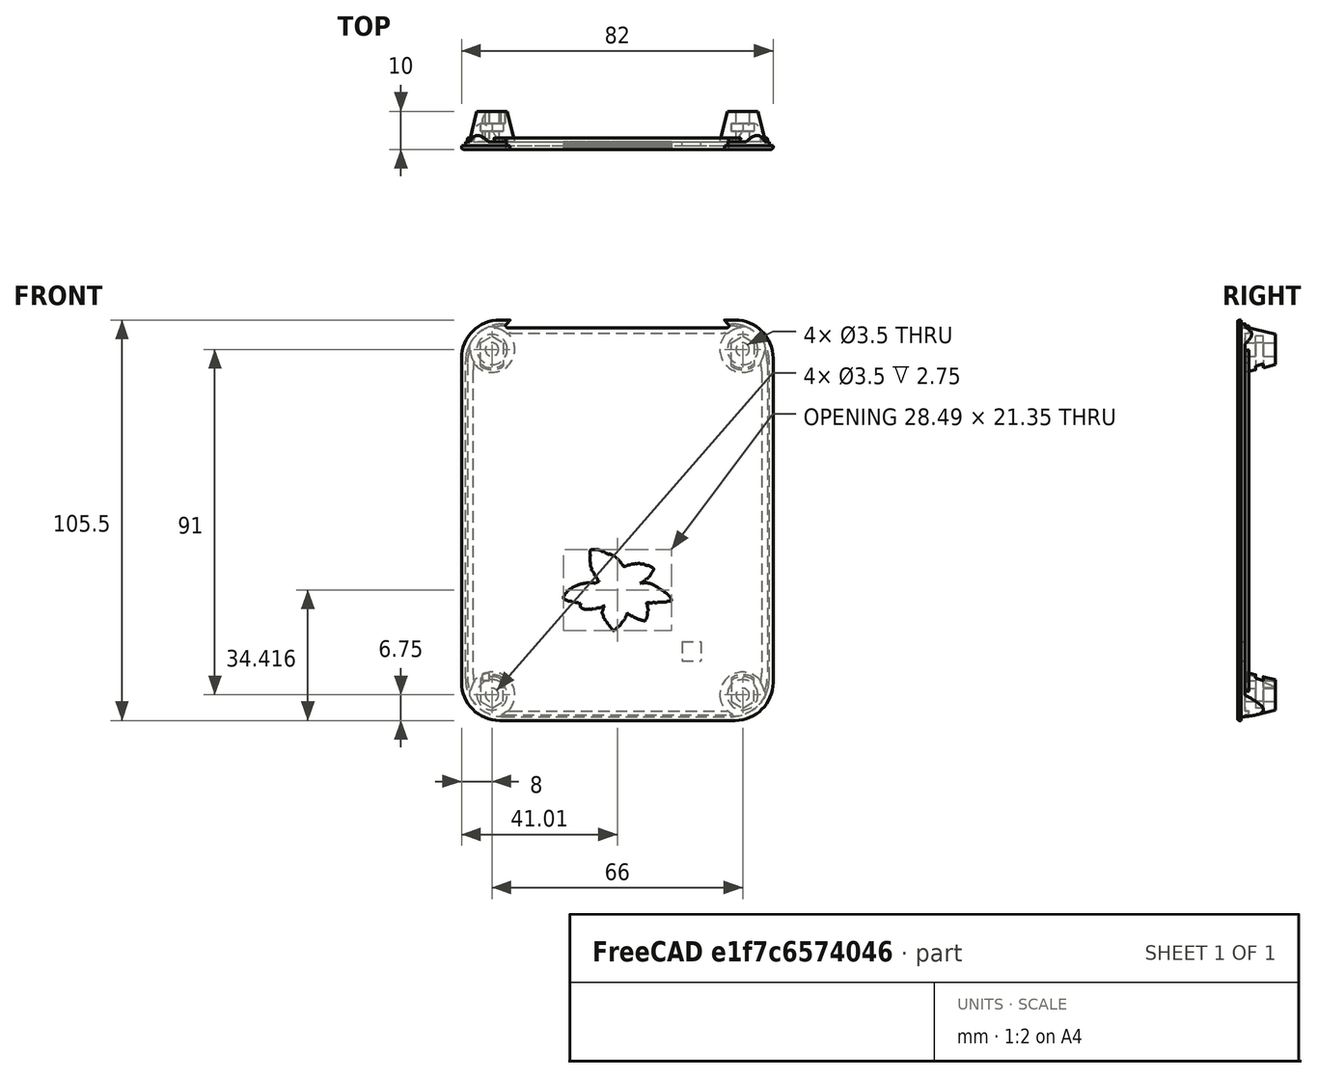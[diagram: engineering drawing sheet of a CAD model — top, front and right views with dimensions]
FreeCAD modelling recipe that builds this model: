
FCSTD DOCUMENT  (FreeCAD 0.20R29410 (Git))
Label: wearableV2_01_16_2023
License: All rights reserved
LicenseURL: http://en.wikipedia.org/wiki/All_rights_reserved
objects: Part::Box×75, Part::MultiFuse×69, Part::Cylinder×59, Part::Fillet×34, Part::Feature×26, Part::Cut×20, Sketcher::SketchObject×18, Part::Extrusion×14, Part::Mirroring×11, Part::Cone×5, PartDesign::Pad×4, PartDesign::Body×4, Part::FeaturePython×4, App::Part×2, Mesh::Feature×1
note: 347 computed .brp shape members not serialized (recipe doc carries the construction recipe); baked Part::Feature solids carry a one-line shape summary decoded from their .brp

FEATURE [Part::Feature] Part__Feature  label="2_BAT_1_1"
  shape: bbox 14.52 x 64.97 x 15.41 mm, 79 faces (baked)
FEATURE [Part::Feature] Part__Feature001  label="2_C_1_1"
  shape: bbox 73.62 x 34.12 x 73.84 mm, 562 faces (baked)
FEATURE [Part::Feature] Part__Feature002  label="2_A_1_1"
  shape: bbox 73.61 x 58.23 x 73.83 mm, 215 faces (baked)
FEATURE [Part::Feature] Part__Feature003  label="2_B_2_1"
  shape: bbox 78.1 x 64.8 x 77.53 mm, 719 faces (baked)
FEATURE [Part::MultiFuse] Fusion
  Shapes = -> [Part__Feature003,Part__Feature002]
FEATURE [Part::MultiFuse] Fusion001
  Shapes = -> [Part__Feature001,Part__Feature]
FEATURE [Part::Feature] Part__Feature004  label="Open CASCADE STEP translator 7.4 2.1.1"
  shape: bbox 8.3 x 1.9 x 1 mm, 10 faces, 0 solids (baked)
FEATURE [Part::Feature] Part__Feature005  label="Open CASCADE STEP translator 7.4 2.1.2"
  shape: bbox 12.5 x 10 x 1.5 mm, 6 faces, 0 solids (baked)
FEATURE [Part::Feature] Part__Feature006  label="Open CASCADE STEP translator 7.4 2.1.3"
  shape: bbox 12.5 x 10 x 1.5 mm, 6 faces, 0 solids (baked)
FEATURE [Part::Feature] Part__Feature007  label="Open CASCADE STEP translator 7.4 2.1.4"
  shape: bbox 12.5 x 10 x 1.5 mm, 6 faces, 0 solids (baked)
FEATURE [Part::Feature] Part__Feature008  label="Open CASCADE STEP translator 7.4 2.1.5"
  shape: bbox 12.5 x 10 x 1.5 mm, 6 faces, 0 solids (baked)
FEATURE [Part::Feature] Part__Feature009  label="Open CASCADE STEP translator 7.4 2.1.6"
  shape: bbox 89.5 x 57.1 x 20.65 mm, 2741 faces, 0 solids (baked)
FEATURE [App::Part] Open_CASCADE_STEP_translator_7_4_2_1  label="Open CASCADE STEP translator 7.4 2.1"
  Group = -> [Part__Feature004,Part__Feature005,Part__Feature006,Part__Feature007,Part__Feature008,Part__Feature009]
  Origin = -> Origin
FEATURE [Part::Box] Box  label="Cube"
  AttacherType = Attacher::AttachEngine3D
  Height = 77
  Length = 78
  Width = 10
FEATURE [Part::Feature] Part__Feature010  label="m312mm"
  Placement = pos=(63.5,-7,61.5) rot=(0,0.707107,0.707107;3.14159rad)
  shape: bbox 6.201 x 15.54 x 6.201 mm, 70 faces (baked)
FEATURE [Part::Feature] Part__Feature011  label="m312mm001"
  Placement = pos=(14.5,-7,61.5) rot=(-1,0,0;1.5708rad)
  shape: bbox 6.201 x 15.54 x 6.201 mm, 70 faces (baked)
FEATURE [Part::MultiFuse] Fusion003
  Shapes = -> [Part__Feature011,Part__Feature010]
FEATURE [Part::Feature] Part__Feature012  label="m312mm002"
  Placement = pos=(14.5,-7,61.5) rot=(-1,0,0;1.5708rad)
  shape: bbox 6.201 x 15.54 x 6.201 mm, 70 faces (baked)
FEATURE [Part::Feature] Part__Feature013  label="m312mm003"
  Placement = pos=(63.5,-7,61.5) rot=(0,0.707107,0.707107;3.14159rad)
  shape: bbox 6.201 x 15.54 x 6.201 mm, 70 faces (baked)
FEATURE [Part::MultiFuse] Fusion004
  Placement = pos=(0,0,-58) rot=(0,0,1;0rad)
  Shapes = -> [Part__Feature012,Part__Feature013]
FEATURE [Part::MultiFuse] Fusion005  label="m3s"
  Placement = pos=(0.1,-1,0) rot=(0,0,1;0rad)
  Shapes = -> [Fusion004,Fusion003]
FEATURE [App::Part] Open_CASCADE_STEP_translator_7_4_2  label="C4"
  Group = -> [Open_CASCADE_STEP_translator_7_4_2_1,Part__Feature010,Part__Feature011,Fusion003,Part__Feature012,Part__Feature013,Fusion004,Fusion005]
  Origin = -> Origin001
  Placement = pos=(67,-7,0) rot=(0.57735,-0.57735,0.57735;2.0944rad)
FEATURE [Part::Box] Box001  label="Cube001"
  AttacherType = Attacher::AttachEngine3D
  Height = 40
  Length = 25
  Placement = pos=(27,-3,12) rot=(0,0,1;0rad)
  Width = 3
FEATURE [Part::Cylinder] Cylinder
  Angle = 360
  AttacherType = Attacher::AttachEngine3D
  FirstAngle = 0
  Height = 3
  Placement = pos=(14.5,-7,3.5) rot=(-1,0,0;1.5708rad)
  Radius = 3.25
  SecondAngle = 0
FEATURE [Part::Cylinder] Cylinder001
  Angle = 360
  AttacherType = Attacher::AttachEngine3D
  FirstAngle = 0
  Height = 3
  Placement = pos=(63.5,-7,3.5) rot=(-1,0,0;1.5708rad)
  Radius = 3.25
  SecondAngle = 0
FEATURE [Part::Cylinder] Cylinder002
  Angle = 360
  AttacherType = Attacher::AttachEngine3D
  FirstAngle = 0
  Height = 3
  Placement = pos=(14.5,-7,3.5) rot=(-1,0,0;1.5708rad)
  Radius = 3.25
  SecondAngle = 0
FEATURE [Part::Cylinder] Cylinder003
  Angle = 360
  AttacherType = Attacher::AttachEngine3D
  FirstAngle = 0
  Height = 3
  Placement = pos=(63.5,-7,3.5) rot=(-1,0,0;1.5708rad)
  Radius = 3.25
  SecondAngle = 0
FEATURE [Part::MultiFuse] Fusion007
  Placement = pos=(0,0,58) rot=(0,0,1;0rad)
  Shapes = -> [Cylinder002,Cylinder003]
FEATURE [Part::Box] Box002  label="Cube002"
  AttacherType = Attacher::AttachEngine3D
  Height = 25
  Length = 5.8
  Placement = pos=(12.12,-7,5.12) rot=(-0.300549,0.945607,0.124491;0.825727rad)
  Width = 3
FEATURE [Part::Mirroring] Part__Mirroring  label="Cube002 (Mirror #1)"
  Base = (0,0,0)
  Normal = (0,0,1)
  Placement = pos=(0,0,65) rot=(0,0,1;0rad)
  Source = -> Box002
FEATURE [Part::MultiFuse] Fusion009
  Shapes = -> [Part__Mirroring,Box002]
FEATURE [Part::Mirroring] Part__Mirroring001  label="Fusion009 (Mirror #2)"
  Base = (0,0,0)
  Normal = (1,0,0)
  Placement = pos=(78,0,0) rot=(0,0,1;0rad)
  Source = -> Fusion009
FEATURE [Part::MultiFuse] Fusion010
  Shapes = -> [Fusion009,Part__Mirroring001]
FEATURE [Part::Box] Box003  label="Cube003"
  AttacherType = Attacher::AttachEngine3D
  Height = 17.78
  Length = 25.4
  Width = 3
FEATURE [Part::Cylinder] Cylinder004
  Angle = 360
  AttacherType = Attacher::AttachEngine3D
  FirstAngle = 0
  Height = 10
  Placement = pos=(2.54,0,2.54) rot=(1,0,0;1.5708rad)
  Radius = 1
  SecondAngle = 0
FEATURE [Part::Cylinder] Cylinder005
  Angle = 360
  AttacherType = Attacher::AttachEngine3D
  FirstAngle = 0
  Height = 10
  Placement = pos=(2.54,0,15.24) rot=(1,0,0;1.5708rad)
  Radius = 1
  SecondAngle = 0
FEATURE [Part::MultiFuse] Fusion011
  Shapes = -> [Cylinder005,Cylinder004]
FEATURE [Part::Cylinder] Cylinder006
  Angle = 360
  AttacherType = Attacher::AttachEngine3D
  FirstAngle = 0
  Height = 10
  Placement = pos=(2.54,0,2.54) rot=(1,0,0;1.5708rad)
  Radius = 1
  SecondAngle = 0
FEATURE [Part::Cylinder] Cylinder007
  Angle = 360
  AttacherType = Attacher::AttachEngine3D
  FirstAngle = 0
  Height = 10
  Placement = pos=(2.54,0,15.24) rot=(1,0,0;1.5708rad)
  Radius = 1
  SecondAngle = 0
FEATURE [Part::MultiFuse] Fusion012
  Placement = pos=(20.32,0,0) rot=(0,0,1;0rad)
  Shapes = -> [Cylinder007,Cylinder006]
FEATURE [Part::MultiFuse] Fusion013
  Placement = pos=(0,3,0) rot=(0,0,1;0rad)
  Shapes = -> [Fusion012,Fusion011]
FEATURE [Part::Cut] Cut
  Base = -> Box003
  Tool = -> Fusion013
FEATURE [Part::Fillet] Fillet
  Base = -> Cut
  Edges = 1 edges r=2: [Edge2]
FEATURE [Part::Fillet] Fillet001
  Base = -> Fillet
  Edges = 1 edges r=2: [Edge2]
FEATURE [Part::Fillet] Fillet002
  Base = -> Fillet001
  Edges = 1 edges r=2: [Edge25]
FEATURE [Part::Fillet] Fillet003  label="bme280AdaFruit"
  Base = -> Fillet002
  Edges = 1 edges r=2: [Edge14]
  Placement = pos=(71,-17.75,-5) rot=(0.57735,0.57735,0.57735;4.18879rad)
FEATURE [Part::Feature] Part__Feature014  label="scd30"
  Placement = pos=(2,-8.5,11) rot=(0.57735,0.57735,0.57735;4.18879rad)
  shape: bbox 7.027 x 23.02 x 35.11 mm, 2292 faces, 25 solids (baked)
FEATURE [Part::Feature] Part__Feature033  label="ips7100"
  Placement = pos=(39,202,-9e-14) rot=(0,-0.707107,0.707107;3.14159rad)
  shape: bbox 48.14 x 44.14 x 13.72 mm, 1935 faces (baked)
FEATURE [Part::Box] Box004  label="Cube004"
  AttacherType = Attacher::AttachEngine3D
  Height = 17.78
  Length = 25.4
  Width = 3
FEATURE [Part::Cylinder] Cylinder008
  Angle = 360
  AttacherType = Attacher::AttachEngine3D
  FirstAngle = 0
  Height = 10
  Placement = pos=(2.54,0,2.54) rot=(1,0,0;1.5708rad)
  Radius = 1
  SecondAngle = 0
FEATURE [Part::Cylinder] Cylinder009
  Angle = 360
  AttacherType = Attacher::AttachEngine3D
  FirstAngle = 0
  Height = 10
  Placement = pos=(2.54,-27.63,15.24) rot=(1,0,0;1.5708rad)
  Radius = 1
  SecondAngle = 0
FEATURE [Part::Cylinder] Cylinder010
  Angle = 360
  AttacherType = Attacher::AttachEngine3D
  FirstAngle = 0
  Height = 10
  Placement = pos=(2.54,0,2.54) rot=(1,0,0;1.5708rad)
  Radius = 1
  SecondAngle = 0
FEATURE [Part::Cylinder] Cylinder011
  Angle = 360
  AttacherType = Attacher::AttachEngine3D
  FirstAngle = 0
  Height = 10
  Placement = pos=(2.54,0,15.24) rot=(1,0,0;1.5708rad)
  Radius = 1
  SecondAngle = 0
FEATURE [Part::MultiFuse] Fusion014
  Shapes = -> [Cylinder009,Cylinder008]
FEATURE [Part::MultiFuse] Fusion015
  Placement = pos=(20.32,0,0) rot=(0,0,1;0rad)
  Shapes = -> [Cylinder011,Cylinder010]
FEATURE [Part::MultiFuse] Fusion016
  Placement = pos=(0,3,0) rot=(0,0,1;0rad)
  Shapes = -> [Fusion015,Fusion014]
FEATURE [Part::Cut] Cut001
  Base = -> Box004
  Placement = pos=(71,-17.7,20.4) rot=(0.57735,-0.57735,-0.57735;4.18879rad)
  Tool = -> Fusion016
FEATURE [Part::Box] Box005  label="Cube005"
  AttacherType = Attacher::AttachEngine3D
  Height = 35
  Length = 3
  Placement = pos=(8,-19,-5) rot=(0,0,1;0rad)
  Width = 19
FEATURE [Part::Box] Box006  label="Cube006"
  AttacherType = Attacher::AttachEngine3D
  Height = 35
  Length = 3
  Placement = pos=(8,-22,-2) rot=(0,0,1;0rad)
  Width = 19
FEATURE [Part::Cut] Cut002
  Base = -> Box005
  Placement = pos=(0.5,0,0) rot=(0,0,1;0rad)
  Tool = -> Box006
FEATURE [Part::Box] Box007  label="Cube007"
  AttacherType = Attacher::AttachEngine3D
  Height = 17
  Length = 36.5
  Width = 3
FEATURE [Part::Cylinder] Cylinder012  label="m2s"
  Angle = 360
  AttacherType = Attacher::AttachEngine3D
  FirstAngle = 0
  Height = 10
  Placement = pos=(0,0,0) rot=(1,0,0;1.5708rad)
  Radius = 1.2
  SecondAngle = 0
FEATURE [Part::Cylinder] Cylinder014  label="m2s001"
  Angle = 360
  AttacherType = Attacher::AttachEngine3D
  FirstAngle = 0
  Height = 10
  Placement = pos=(30,0,0) rot=(1,0,0;1.5708rad)
  Radius = 1.2
  SecondAngle = 0
FEATURE [Part::MultiFuse] Fusion017
  Placement = pos=(3.25,0,0) rot=(0,0,1;0rad)
  Shapes = -> [Cylinder014,Cylinder012]
FEATURE [Part::Cylinder] Cylinder015  label="m2s002"
  Angle = 360
  AttacherType = Attacher::AttachEngine3D
  FirstAngle = 0
  Height = 10
  Placement = pos=(0,0,0) rot=(1,0,0;1.5708rad)
  Radius = 1.2
  SecondAngle = 0
FEATURE [Part::Cylinder] Cylinder016  label="m2s003"
  Angle = 360
  AttacherType = Attacher::AttachEngine3D
  FirstAngle = 0
  Height = 10
  Placement = pos=(30,0,0) rot=(1,0,0;1.5708rad)
  Radius = 1.2
  SecondAngle = 0
FEATURE [Part::MultiFuse] Fusion018
  Placement = pos=(3.25,0,7) rot=(0,0,1;0rad)
  Shapes = -> [Cylinder016,Cylinder015]
FEATURE [Part::MultiFuse] Fusion019
  Placement = pos=(0,3,5) rot=(0,0,1;0rad)
  Shapes = -> [Fusion017,Fusion018]
FEATURE [Part::Cut] Cut003
  Base = -> Box007
  Tool = -> Fusion019
FEATURE [Part::Fillet] Fillet008  label="converterSupport"
  Base = -> Cut003
  Edges = 4 edges r=2: [Edge2,Edge4,Edge13,Edge20]
  Placement = pos=(68,-17,23) rot=(0.57735,0.57735,0.57735;4.18879rad)
FEATURE [Part::Box] Box008  label="Cube008"
  AttacherType = Attacher::AttachEngine3D
  Height = 6
  Length = 30
  Placement = pos=(11,-3,16) rot=(0,0,1;0rad)
  Width = 3
FEATURE [Part::Box] Box009  label="Cube009"
  AttacherType = Attacher::AttachEngine3D
  Height = 6
  Length = 30
  Placement = pos=(41,-3,32) rot=(0,0,1;0rad)
  Width = 3
FEATURE [Part::Box] Box010  label="Cube010"
  AttacherType = Attacher::AttachEngine3D
  Height = 6
  Length = 27
  Placement = pos=(44,-3,12) rot=(0,0,1;0rad)
  Width = 3
  expr: .Placement.Base.z = 12
FEATURE [Part::Box] Box011  label="Cube011"
  AttacherType = Attacher::AttachEngine3D
  Height = 6.25
  Length = 8
  Placement = pos=(63,-7,0.3) rot=(0,0,1;0rad)
  Width = 3
FEATURE [Part::Box] Box012  label="Cube012"
  AttacherType = Attacher::AttachEngine3D
  Height = 6.25
  Length = 3
  Placement = pos=(11.5,-4,6.3) rot=(0,1,0;3.14159rad)
  Width = 3
FEATURE [Part::Box] Box013  label="Cube013"
  AttacherType = Attacher::AttachEngine3D
  Height = 6.25
  Length = 6
  Placement = pos=(14.5,-7,6.3) rot=(0,1,0;3.14159rad)
  Width = 3
FEATURE [Part::Cylinder] Cylinder017
  Angle = 360
  AttacherType = Attacher::AttachEngine3D
  FirstAngle = 0
  Height = 3
  Placement = pos=(11.5,-1.7,28.45) rot=(0.57735,0.57735,-0.57735;4.18879rad)
  Radius = 3.25
  SecondAngle = 0
FEATURE [Part::Cylinder] Cylinder018
  Angle = 360
  AttacherType = Attacher::AttachEngine3D
  FirstAngle = 0
  Height = 3
  Placement = pos=(11.5,-17.9,-3.55) rot=(0.57735,0.57735,-0.57735;4.18879rad)
  Radius = 3.25
  SecondAngle = 0
FEATURE [Part::MultiFuse] Fusion020
  Shapes = -> [Cylinder,Cylinder001]
FEATURE [Part::MultiFuse] Fusion021  label="m3Legs"
  Shapes = -> [Fusion020,Fusion007]
FEATURE [Part::MultiFuse] Fusion022  label="scdM2Supports"
  Shapes = -> [Cylinder018,Cylinder017]
FEATURE [Part::MultiFuse] Fusion023  label="base"
  Shapes = -> [Fusion010,Box001]
FEATURE [Part::MultiFuse] Fusion025  label="baseSuports"
  Shapes = -> [Box013,Box008,Box009,Box010,Box011,Box012]
FEATURE [Part::Cylinder] Cylinder019
  Angle = 360
  AttacherType = Attacher::AttachEngine3D
  FirstAngle = 0
  Height = 6
  Placement = pos=(14.5,-7,3.5) rot=(-1,0,0;1.5708rad)
  Radius = 1.6
  SecondAngle = 0
FEATURE [Part::Cylinder] Cylinder020
  Angle = 360
  AttacherType = Attacher::AttachEngine3D
  FirstAngle = 0
  Height = 6
  Placement = pos=(63.5,-7,3.5) rot=(-1,0,0;1.5708rad)
  Radius = 1.6
  SecondAngle = 0
FEATURE [Part::Cylinder] Cylinder021
  Angle = 360
  AttacherType = Attacher::AttachEngine3D
  FirstAngle = 0
  Height = 6
  Placement = pos=(14.5,-7,3.5) rot=(-1,0,0;1.5708rad)
  Radius = 1.6
  SecondAngle = 0
FEATURE [Part::Cylinder] Cylinder022
  Angle = 360
  AttacherType = Attacher::AttachEngine3D
  FirstAngle = 0
  Height = 6
  Placement = pos=(63.5,-7,3.5) rot=(-1,0,0;1.5708rad)
  Radius = 1.6
  SecondAngle = 0
FEATURE [Part::MultiFuse] Fusion027
  Placement = pos=(0,0,58) rot=(0,0,1;0rad)
  Shapes = -> [Cylinder021,Cylinder022]
FEATURE [Part::MultiFuse] Fusion028
  Shapes = -> [Cylinder019,Cylinder020]
FEATURE [Part::MultiFuse] Fusion029  label="m3Cuts"
  Shapes = -> [Fusion028,Fusion027]
FEATURE [Part::Cylinder] Cylinder023
  Angle = 360
  AttacherType = Attacher::AttachEngine3D
  FirstAngle = 0
  Height = 7
  Placement = pos=(14.5,-7,3.5) rot=(-1,0,0;1.5708rad)
  Radius = 3.25
  SecondAngle = 0
FEATURE [Part::Cylinder] Cylinder024
  Angle = 360
  AttacherType = Attacher::AttachEngine3D
  FirstAngle = 0
  Height = 3
  Placement = pos=(63.5,-7,3.5) rot=(-1,0,0;1.5708rad)
  Radius = 3.25
  SecondAngle = 0
FEATURE [Part::Cylinder] Cylinder025
  Angle = 360
  AttacherType = Attacher::AttachEngine3D
  FirstAngle = 0
  Height = 3
  Placement = pos=(14.5,-7,3.5) rot=(-1,0,0;1.5708rad)
  Radius = 3.25
  SecondAngle = 0
FEATURE [Part::Cylinder] Cylinder026
  Angle = 360
  AttacherType = Attacher::AttachEngine3D
  FirstAngle = 0
  Height = 3
  Placement = pos=(63.5,-7,3.5) rot=(-1,0,0;1.5708rad)
  Radius = 3.25
  SecondAngle = 0
FEATURE [Part::MultiFuse] Fusion030
  Placement = pos=(0,0,58) rot=(0,0,1;0rad)
  Shapes = -> [Cylinder025,Cylinder026]
FEATURE [Part::MultiFuse] Fusion031
  Shapes = -> [Cylinder023,Cylinder024]
FEATURE [Part::MultiFuse] Fusion032  label="m3Cuts001"
  Placement = pos=(0,3.05,0) rot=(0,0,1;0rad)
  Shapes = -> [Fusion031,Fusion030]
FEATURE [Part::Box] Box014  label="baseCut"
  AttacherType = Attacher::AttachEngine3D
  Height = 47
  Length = 46
  Placement = pos=(16,0,9) rot=(0,0,1;0rad)
  Width = 3
FEATURE [Part::Cylinder] Cylinder027
  Angle = 360
  AttacherType = Attacher::AttachEngine3D
  FirstAngle = 0
  Height = 6
  Placement = pos=(11.5,-1.7,28.45) rot=(0.57735,0.57735,-0.57735;4.18879rad)
  Radius = 1.2
  SecondAngle = 0
FEATURE [Part::Cylinder] Cylinder028
  Angle = 360
  AttacherType = Attacher::AttachEngine3D
  FirstAngle = 0
  Height = 6
  Placement = pos=(11.5,-17.9,-3.55) rot=(0.57735,0.57735,-0.57735;4.18879rad)
  Radius = 1.2
  SecondAngle = 0
FEATURE [Part::MultiFuse] Fusion033  label="scdM2Cuts"
  Shapes = -> [Cylinder028,Cylinder027]
FEATURE [Part::Cylinder] Cylinder029
  Angle = 360
  AttacherType = Attacher::AttachEngine3D
  FirstAngle = 0
  Height = 6
  Placement = pos=(9.09,-4.25,29) rot=(0.57735,0.57735,-0.57735;4.18879rad)
  Radius = 1.1
  SecondAngle = 0
FEATURE [Part::Fillet] Fillet009  label="scdCut"
  Base = -> Cylinder029
  Edges = 1 edges r=0.5: [Edge2]
FEATURE [Part::MultiFuse] Fusion034  label="baseCuts"
  Shapes = -> [Fusion029,Fusion032,Box014,Fusion033,Fillet009]
FEATURE [Part::Fillet] Fillet010
  Base = -> Cut001
  Edges = 1 edges r=2: [Edge4]
  Placement = pos=(0,-0.08,0) rot=(0,0,1;0rad)
FEATURE [Part::MultiFuse] Fusion035  label="base001"
  Shapes = -> [Fillet010,Fusion025,Fusion023,Fusion022,Fusion021,Fillet008,Cut002]
FEATURE [Part::Cut] Cut004  label="base002"
  Base = -> Fusion035
  Tool = -> Fusion034
FEATURE [Part::Fillet] Fillet011
  Base = -> Cut004
  Edges = 13 edges r=0.9: [Edge25,Edge26,Edge27,Edge31,Edge32,Edge33,Edge34,Edge146,Edge205,Edge206,Edge275,Edge281,Edge486]
FEATURE [Part::Fillet] Fillet012
  Base = -> Fillet011
  Edges = 18 edges r=0.2: [Edge67,Edge76,Edge111,Edge140,Edge195,Edge199,Edge200,Edge203,Edge204,Edge207,Edge208,Edge249,Edge292,Edge327,Edge332,Edge335,Edge386,Edge459]
FEATURE [Part::Cut] Cut005  label="base003"
  Base = -> Fillet012
  Tool = -> Box
FEATURE [Part::Fillet] Fillet013  label="base004"
  Base = -> Cut005
  Edges = 2 edges r=1: [Edge497,Edge518]
FEATURE [Part::Fillet] Fillet014  label="c4Support"
  Base = -> Fillet013
  Edges = 3 edges: [Edge571 r=1,Edge596 r=2,Edge599 r=2]
FEATURE [Part::Box] Box015  label="Cube014"
  AttacherType = Attacher::AttachEngine3D
  Height = 105.5
  Length = 82
  Placement = pos=(80,26,-15.75) rot=(0,0,1;3.14159rad)
  Width = 50.5
FEATURE [Part::Fillet] Fillet015  label="outerBox"
  Base = -> Box015
  Edges = 4 edges r=10: [Edge2,Edge4,Edge6,Edge8]
FEATURE [Part::Box] Box016  label="Cube015"
  AttacherType = Attacher::AttachEngine3D
  Height = 101.5
  Length = 78
  Placement = pos=(78,24,-13.75) rot=(0,0,1;3.14159rad)
  Width = 50.5
FEATURE [Part::Fillet] Fillet018  label="innerBoxCut001"
  Base = -> Box016
  Edges = 4 edges r=10: [Edge2,Edge4,Edge6,Edge8]
FEATURE [Part::Cut] Cut006  label="outerShellBottom"
  Base = -> Fillet015
  Tool = -> Fillet018
FEATURE [Part::Feature] Part__Feature034  label="m3Nut"
  Placement = pos=(6,-13.2844,81.9658) rot=(1,0,0;1.5708rad)
  shape: bbox 6.352 x 2.188 x 6.352 mm, 35 faces (baked)
FEATURE [Part::Feature] Part__Feature039  label="m3s45s"
  Placement = pos=(72,4,-9) rot=(0,0.707107,0.707107;3.14159rad)
  shape: bbox 5.501 x 48.04 x 5.501 mm, 104 faces (baked)
FEATURE [Part::Feature] Part__Feature040  label="m3s45s001"
  Placement = pos=(6,4,-9) rot=(0,0.707107,0.707107;3.14159rad)
  shape: bbox 5.501 x 48.04 x 5.501 mm, 104 faces (baked)
FEATURE [Part::Feature] Part__Feature041  label="m3s45s002"
  Placement = pos=(6,4,82) rot=(0,0.707107,0.707107;3.14159rad)
  shape: bbox 5.501 x 48.04 x 5.501 mm, 104 faces (baked)
FEATURE [Part::Feature] Part__Feature042  label="m3s45s003"
  Placement = pos=(72,4,82) rot=(0,0.707107,0.707107;3.14159rad)
  shape: bbox 5.501 x 48.04 x 5.501 mm, 104 faces (baked)
FEATURE [Part::MultiFuse] Fusion036  label="m3s45s004"
  Placement = pos=(0,-2.5,0) rot=(0,0,1;0rad)
  Shapes = -> [Part__Feature039,Part__Feature040,Part__Feature041,Part__Feature042]
FEATURE [Sketcher::SketchObject] Sketch001
  FullyConstrained = false
  MapMode = 5
  Placement = pos=(0,0,0) rot=(1,0,0;1.5708rad)
  Support = -> [XZ_Plane002]
  sketch-geometry (5):
    g0: LineSegment StartX=0 StartY=77.5 StartZ=0 EndX=10.75 EndY=77.5 EndZ=0
    g1: LineSegment StartX=10.75 StartY=77.5 StartZ=0 EndX=10.75 EndY=74.234 EndZ=0
    g2: ArcOfCircle CenterX=15.5057 CenterY=59.9075 CenterZ=0 NormalX=0 NormalY=0 NormalZ=1 AngleXU=0 Radius=15.0952 StartAngle=1.8913 EndAngle=3.06915
    g3: LineSegment StartX=0 StartY=77.5 StartZ=0 EndX=0 EndY=61 EndZ=0
    g4: LineSegment StartX=0 StartY=61 StartZ=0 EndX=0.45 EndY=61 EndZ=0
  constraints (14):
    c: Coincident(g4,g3)
    c: Vertical(g3)
    c: Horizontal(g4)
    c: Horizontal(g0)
    c: Vertical(g1)
    c: DistanceY(g3,g0) = 16.5
    c: DistanceX(g0,g0) = 10.75
    c: DistanceX(g3,g2) = 0.45
    c: DistanceY(g-1,g3) = 61
    c: DistanceX(g3,g-1) = 0
    c: Coincident(g2,g4)
    c: Coincident(g2,g1)
    c: Coincident(g1,g0)
    c: Coincident(g0,g3)
FEATURE [PartDesign::Pad] Pad
  Direction = (0,-1,-2e-16)
  Length = 15
  Length2 = 10
  Placement = pos=(0,0,0) rot=(1,0,0;1.5708rad)
  Profile = -> Sketch001
  ReferenceAxis = -> Sketch001 [N_Axis]
  Type = 0
FEATURE [PartDesign::Body] Body  label="batteryHold"
  Group = -> [Sketch001,Pad]
  Origin = -> Origin002
  Placement = pos=(0,24,0) rot=(0,0,1;0rad)
  Tip = -> Pad
FEATURE [Part::Mirroring] Part__Mirroring002  label="batteryHold (Mirror #3)"
  Base = (7.62939e-06,8,69.25)
  Normal = (1,0,-1.19209e-07)
  Placement = pos=(78,0,0) rot=(0,0,1;0rad)
  Source = -> Body
FEATURE [Sketcher::SketchObject] Sketch002
  FullyConstrained = false
  MapMode = 5
  Placement = pos=(0,0,0) rot=(1,0,0;1.5708rad)
  Support = -> [XZ_Plane003]
  sketch-geometry (5):
    g0: LineSegment StartX=0 StartY=77.5 StartZ=0 EndX=10.75 EndY=77.5 EndZ=0
    g1: LineSegment StartX=10.75 StartY=77.5 StartZ=0 EndX=10.75 EndY=74.234 EndZ=0
    g2: ArcOfCircle CenterX=15.5057 CenterY=59.9075 CenterZ=0 NormalX=0 NormalY=0 NormalZ=1 AngleXU=0 Radius=15.0952 StartAngle=1.8913 EndAngle=3.06915
    g3: LineSegment StartX=0 StartY=77.5 StartZ=0 EndX=0 EndY=61 EndZ=0
    g4: LineSegment StartX=0 StartY=61 StartZ=0 EndX=0.45 EndY=61 EndZ=0
  constraints (14):
    c: Coincident(g4,g3)
    c: Vertical(g3)
    c: Horizontal(g4)
    c: Horizontal(g0)
    c: Vertical(g1)
    c: DistanceY(g3,g0) = 16.5
    c: DistanceX(g0,g0) = 10.75
    c: DistanceX(g3,g2) = 0.45
    c: DistanceY(g-1,g3) = 61
    c: DistanceX(g3,g-1) = 0
    c: Coincident(g2,g4)
    c: Coincident(g2,g1)
    c: Coincident(g1,g0)
    c: Coincident(g0,g3)
FEATURE [PartDesign::Pad] Pad001
  Direction = (0,-1,-2e-16)
  Length = 15
  Length2 = 10
  Placement = pos=(0,0,0) rot=(1,0,0;1.5708rad)
  Profile = -> Sketch002
  ReferenceAxis = -> Sketch002 [N_Axis]
  Type = 0
FEATURE [PartDesign::Body] Body001  label="batteryHold001"
  Group = -> [Sketch002,Pad001]
  Origin = -> Origin003
  Placement = pos=(0,24,0) rot=(0,0,1;0rad)
  Tip = -> Pad001
FEATURE [Part::Mirroring] Part__Mirroring003  label="batteryHold001 (Mirror #4)"
  Base = (0,0,0)
  Normal = (0,0,1)
  Placement = pos=(0,0,74.5) rot=(0,0,1;0rad)
  Source = -> Body001
FEATURE [Part::Mirroring] Part__Mirroring004  label="batteryHold001 (Mirror #5)"
  Base = (0,0,0)
  Normal = (1,0,0)
  Placement = pos=(78,0,0) rot=(0,0,1;0rad)
  Source = -> Part__Mirroring003
FEATURE [Sketcher::SketchObject] Sketch003
  FullyConstrained = false
  Placement = pos=(0,0,0) rot=(1,0,0;1.5708rad)
  sketch-geometry (10):
    g0: LineSegment StartX=4.54947 StartY=57.2679 StartZ=0 EndX=0.883944 EndY=66.2686 EndZ=0
    g1: LineSegment StartX=4.54947 StartY=57.2679 StartZ=0 EndX=15.7468 EndY=57.2679 EndZ=0
    g2: ArcOfCircle CenterX=15.3573 CenterY=61.5 CenterZ=0 NormalX=0 NormalY=0 NormalZ=1 AngleXU=0 Radius=4.25 StartAngle=4.80417 EndAngle=7.22437
    g3: LineSegment StartX=17.8598 StartY=64.9351 StartZ=0 EndX=10.3641 EndY=71.1208 EndZ=0
    g4: LineSegment StartX=0.883944 StartY=78.6544 StartZ=0 EndX=0.883944 EndY=66.2686 EndZ=0
    g5: LineSegment StartX=10.3641 StartY=71.1208 StartZ=0 EndX=10.3641 EndY=84.4107 EndZ=0
    g6: LineSegment StartX=10.3641 StartY=84.4107 StartZ=0 EndX=7.98639 EndY=84.4107 EndZ=0
    g7: ArcOfCircle CenterX=7.97265 CenterY=85.778 CenterZ=0 NormalX=0 NormalY=0 NormalZ=1 AngleXU=0 Radius=1.36738 StartAngle=3.03277 EndAngle=4.72244
    g8: ArcOfCircle CenterX=9.10309 CenterY=79.0296 CenterZ=0 NormalX=0 NormalY=0 NormalZ=1 AngleXU=0 Radius=8.22771 StartAngle=1.87822 EndAngle=3.18722
    g9: LineSegment StartX=6.61336 StartY=85.9265 StartZ=0 EndX=6.61336 EndY=86.8716 EndZ=0
  constraints (19):
    c: Coincident(g1,g0)
    c: Horizontal(g1)
    c: Coincident(g2,g1)
    c: Coincident(g3,g2)
    c: Coincident(g4,g0)
    c: Vertical(g4)
    c: Equal(g0,g3)
    c: DistanceY(g2) = 61.5
    c: Radius(g2) = 4.25
    c: Coincident(g5,g3)
    c: Vertical(g5)
    c: Coincident(g6,g5)
    c: Horizontal(g6)
    c: Coincident(g7,g6)
    c: Coincident(g8,g4)
    c: Angle(g8) = 1.309
    c: Coincident(g9,g7)
    c: Coincident(g9,g8)
    c: Vertical(g9)
FEATURE [Part::Extrusion] Extrude001  label="c4Holds"
  Base = -> Sketch003
  Dir = (0,-1,2e-16)
  DirMode = 2
  FaceMakerClass = Part::FaceMakerBullseye
  LengthFwd = 4
  LengthRev = 0
  Placement = pos=(0,-8,0) rot=(0,0,1;0rad)
  Solid = true
  Symmetric = false
FEATURE [Sketcher::SketchObject] Sketch004
  FullyConstrained = false
  Placement = pos=(0,0,0) rot=(1,0,0;1.5708rad)
  sketch-geometry (10):
    g0: LineSegment StartX=62.5867 StartY=65.3514 StartZ=0 EndX=65.5388 EndY=65.3514 EndZ=0
    g1: LineSegment StartX=65.5388 StartY=65.3514 StartZ=0 EndX=69.0019 EndY=79 EndZ=0
    g2: LineSegment StartX=76.9995 StartY=79 StartZ=0 EndX=76.9995 EndY=71.157 EndZ=0
    g3: LineSegment StartX=76.9995 StartY=71.157 StartZ=0 EndX=65.548 EndY=57.9699 EndZ=0
    g4: ArcOfCircle CenterX=63.667 CenterY=61.5 CenterZ=0 NormalX=0 NormalY=0 NormalZ=1 AngleXU=0 Radius=4 StartAngle=1.84425 EndAngle=5.20196
    g5: ArcOfCircle CenterX=69.0019 CenterY=79 CenterZ=0 NormalX=0 NormalY=0 NormalZ=1 AngleXU=0 Radius=7.99759 StartAngle=-9e-16 EndAngle=1.27409
    g6: ArcOfCircle CenterX=70.0211 CenterY=85.7541 CenterZ=0 NormalX=0 NormalY=0 NormalZ=1 AngleXU=0 Radius=1.31913 StartAngle=4.71239 EndAngle=6.28319
    g7: LineSegment StartX=69.0019 StartY=79 StartZ=0 EndX=69.0019 EndY=84.3966 EndZ=0
    g8: LineSegment StartX=70.0211 StartY=84.435 StartZ=0 EndX=69.0019 EndY=84.3966 EndZ=0
    g9: LineSegment StartX=71.3402 StartY=85.7541 StartZ=0 EndX=71.3402 EndY=86.6481 EndZ=0
  constraints (22):
    c: Horizontal(g0)
    c: Coincident(g1,g0)
    c: Vertical(g2)
    c: Coincident(g3,g2)
    c: Coincident(g4,g3)
    c: Radius(g4) = 4
    c: Coincident(g0,g4)
    c: DistanceX(g4) = 63.667
    c: DistanceY(g4) = 61.5
    c: DistanceY(g1) = 79
    c: DistanceX(g2) = 76.9995
    c: DistanceY(g2) = 79
    c: Coincident(g5,g1)
    c: Coincident(g5,g2)
    c: Angle(g5) = 1.27409
    c: Coincident(g7,g1)
    c: Vertical(g7)
    c: Coincident(g8,g6)
    c: Coincident(g8,g7)
    c: Coincident(g9,g6)
    c: Vertical(g9)
    c: Coincident(g5,g9)
FEATURE [Part::Extrusion] Extrude002  label="c4Holds001"
  Base = -> Sketch004
  Dir = (0,-1,2e-16)
  DirMode = 2
  FaceMakerClass = Part::FaceMakerBullseye
  LengthFwd = 4
  LengthRev = 0
  Placement = pos=(0,-8,0) rot=(0,0,1;0rad)
  Solid = true
  Symmetric = false
FEATURE [Part::Box] Box019  label="Cube018"
  AttacherType = Attacher::AttachEngine3D
  Height = 4
  Length = 5.25
  Placement = pos=(15.75,24,-13.75) rot=(0,0,-1;1.5708rad)
  Width = 4.5
FEATURE [Part::Fillet] Fillet019  label="IPS insides001"
  Base = -> Box019
  Edges = 1 edges r=1.75: [Edge7]
FEATURE [Part::Box] Box020  label="Cube019"
  AttacherType = Attacher::AttachEngine3D
  Height = 4
  Length = 4.25
  Placement = pos=(15.75,23,-13.75) rot=(0,0,-1;1.5708rad)
  Width = 4.5
FEATURE [Part::Fillet] Fillet020  label="IPS insides"
  Base = -> Box020
  Edges = 1 edges r=1.75: [Edge7]
  Placement = pos=(78,4,0) rot=(0,0,1;3.14159rad)
FEATURE [Sketcher::SketchObject] Sketch005
  FullyConstrained = true
  sketch-geometry (6):
    g0: LineSegment StartX=57.7091 StartY=-19.3468 StartZ=0 EndX=57.7091 EndY=-22.3468 EndZ=0
    g1: LineSegment StartX=57.7091 StartY=-22.3468 StartZ=0 EndX=65.7091 EndY=-22.3468 EndZ=0
    g2: LineSegment StartX=65.7091 StartY=-22.3468 StartZ=0 EndX=65.7091 EndY=-10.3468 EndZ=0
    g3: LineSegment StartX=65.7091 StartY=-10.3468 StartZ=0 EndX=62.7091 EndY=-10.3468 EndZ=0
    g4: LineSegment StartX=62.7091 StartY=-10.3468 StartZ=0 EndX=62.7091 EndY=-19.3468 EndZ=0
    g5: LineSegment StartX=62.7091 StartY=-19.3468 StartZ=0 EndX=57.7091 EndY=-19.3468 EndZ=0
  constraints (18):
    c: Coincident(g0,g1)
    c: Horizontal(g1)
    c: Coincident(g1,g2)
    c: Vertical(g2)
    c: Coincident(g2,g3)
    c: Horizontal(g3)
    c: Coincident(g3,g4)
    c: Vertical(g4)
    c: Coincident(g4,g5)
    c: Coincident(g5,g0)
    c: Horizontal(g5)
    c: DistanceX(g0,g4) = 5
    c: Vertical(g0)
    c: DistanceY(g0,g0) = 3
    c: DistanceX(g0,g1) = 8
    c: DistanceY(g1,g2) = 12
    c: DistanceX(g1) = 65.7091
    c: DistanceY(g1) = -22.3468
FEATURE [Part::Extrusion] Extrude003
  Base = -> Sketch005
  Dir = (0,0,1)
  DirMode = 2
  FaceMakerClass = Part::FaceMakerBullseye
  LengthFwd = 10
  LengthRev = 0
  Placement = pos=(0,0,-14) rot=(0,0,1;0rad)
  Solid = true
  Symmetric = false
FEATURE [Part::Fillet] Fillet021
  Base = -> Extrude003
  Edges = 11 edges r=1: [Edge1,Edge2,Edge5,Edge7,Edge8,Edge10,Edge11,Edge13,Edge14,Edge16,Edge18]
  Placement = pos=(0,0,0.4) rot=(0,0,1;0rad)
FEATURE [Part::Mirroring] Part__Mirroring005  label="Fillet021 (Mirror #6)"
  Base = (0,0,0)
  Normal = (1,0,0)
  Placement = pos=(78,0,0.4) rot=(0,0,1;0rad)
  Source = -> Fillet021
FEATURE [Sketcher::SketchObject] Sketch006
  FullyConstrained = false
  Placement = pos=(0,0,0) rot=(1,0,0;1.5708rad)
  sketch-geometry (7):
    g0: ArcOfCircle CenterX=14.5039 CenterY=3.47044 CenterZ=0 NormalX=0 NormalY=0 NormalZ=1 AngleXU=0 Radius=3.3271 StartAngle=4.79301 EndAngle=7.86685
    g1: LineSegment StartX=14.4611 StartY=6.79726 StartZ=0 EndX=12.2529 EndY=6.79726 EndZ=0
    g2: ArcOfCircle CenterX=5.98953 CenterY=-9.01028 CenterZ=0 NormalX=0 NormalY=0 NormalZ=1 AngleXU=0 Radius=3.23718 StartAngle=1.74677 EndAngle=4.88836
    g3: LineSegment StartX=5.4228 StartY=-5.82309 StartZ=0 EndX=12.2529 EndY=-5.26761 EndZ=0
    g4: LineSegment StartX=12.2529 StartY=-5.26761 StartZ=0 EndX=12.2529 EndY=6.79726 EndZ=0
    g5: LineSegment StartX=6.55625 StartY=-12.1975 StartZ=0 EndX=14.7718 EndY=-12.1975 EndZ=0
    g6: LineSegment StartX=14.7718 StartY=-12.1975 StartZ=0 EndX=14.7718 EndY=0.154152 EndZ=0
  constraints (16):
    c: Coincident(g1,g0)
    c: Horizontal(g1)
    c: Angle(g2) = 3.14159
    c: DistanceX(g0) = 14.5039
    c: DistanceY(g0) = 3.47044
    c: Coincident(g3,g2)
    c: Coincident(g4,g3)
    c: Coincident(g4,g1)
    c: Vertical(g4)
    c: Coincident(g5,g2)
    c: Horizontal(g5)
    c: Coincident(g6,g5)
    c: Coincident(g6,g0)
    c: Vertical(g6)
    c: DistanceX(g2) = 5.98953
    c: DistanceY(g2) = -9.01028
FEATURE [Part::Extrusion] Extrude004
  Base = -> Sketch006
  Dir = (0,-1,-3e-16)
  DirMode = 2
  FaceMakerClass = Part::FaceMakerBullseye
  LengthFwd = 5
  LengthRev = 0
  Placement = pos=(0,-8,0) rot=(0,0,1;0rad)
  Solid = true
  Symmetric = false
FEATURE [Part::Mirroring] Part__Mirroring006  label="Extrude004 (Mirror #7)"
  Base = (0,0,0)
  Normal = (0,0,1)
  Placement = pos=(78,0,2e-15) rot=(0,1,0;3.14159rad)
  Source = -> Extrude004
FEATURE [Part::Cylinder] Cylinder031  label="m3Hold"
  Angle = 90
  AttacherType = Attacher::AttachEngine3D
  FirstAngle = 0
  Height = 32.5
  Placement = pos=(9,24.5,-6) rot=(0,0.707107,-0.707107;3.14159rad)
  Radius = 9
  SecondAngle = 0
FEATURE [Part::Cone] Cone
  Angle = 360
  AttacherType = Attacher::AttachEngine3D
  Height = 11
  Placement = pos=(6,24,-9) rot=(1,0,0;1.5708rad)
  Radius1 = 6
  Radius2 = 2.8
FEATURE [Part::MultiFuse] Fusion037  label="m3Hold001"
  Shapes = -> [Cone,Cylinder031]
FEATURE [Part::Mirroring] Part__Mirroring007  label="m3Hold001 (Mirror #8)"
  Base = (0,0,0)
  Normal = (1,0,0)
  Placement = pos=(78,0,0) rot=(0,0,1;0rad)
  Source = -> Fusion037
FEATURE [Part::MultiFuse] Fusion038
  Shapes = -> [Part__Mirroring007,Fusion037]
FEATURE [Part::Mirroring] Part__Mirroring008  label="Fusion038 (Mirror #9)"
  Base = (0,0,0)
  Normal = (0,0,1)
  Placement = pos=(0,0,73) rot=(0,0,1;0rad)
  Source = -> Fusion038
FEATURE [Part::MultiFuse] Fusion039  label="Stands"
  Shapes = -> [Part__Mirroring008,Fusion038]
FEATURE [Part::MultiFuse] Fusion041  label="c4Holds003"
  Shapes = -> [Part__Mirroring006,Fillet021]
FEATURE [Part::Box] Box021  label="Cube020"
  AttacherType = Attacher::AttachEngine3D
  Height = 4.5
  Length = 8
  Placement = pos=(62.75,24,-4.5) rot=(0,0,-1;1.5708rad)
  Width = 16
FEATURE [Part::Box] Box022  label="Cube021"
  AttacherType = Attacher::AttachEngine3D
  Height = 4.5
  Length = 8
  Placement = pos=(-0.75,24,-4.5) rot=(0,0,-1;1.5708rad)
  Width = 16
FEATURE [Part::MultiFuse] Fusion042  label="ipsHoldsBottomIn"
  Shapes = -> [Box021,Box022]
FEATURE [Part::Box] Box023  label="Cube022"
  AttacherType = Attacher::AttachEngine3D
  Height = 105.5
  Length = 82
  Placement = pos=(-2,-27,-15.75) rot=(0,0,1;0rad)
  Width = 2
FEATURE [Part::Fillet] Fillet024  label="top"
  Base = -> Box023
  Edges = 4 edges r=10: [Edge2,Edge4,Edge6,Edge8]
  Placement = pos=(0,0.5,0) rot=(0,0,1;0rad)
FEATURE [Part::Box] Box024  label="Cube023"
  AttacherType = Attacher::AttachEngine3D
  Height = 105.5
  Length = 82
  Placement = pos=(80,26,-15.75) rot=(0,0,1;3.14159rad)
  Width = 50.5
FEATURE [Part::Box] Box025  label="Cube024"
  AttacherType = Attacher::AttachEngine3D
  Height = 101.5
  Length = 78
  Placement = pos=(78,24,-13.75) rot=(0,0,1;3.14159rad)
  Width = 50.5
FEATURE [Part::Fillet] Fillet027  label="outerBox001"
  Base = -> Box024
  Edges = 4 edges r=10: [Edge2,Edge4,Edge6,Edge8]
FEATURE [Part::Fillet] Fillet028  label="innerBoxCut002"
  Base = -> Box025
  Edges = 4 edges r=10: [Edge2,Edge4,Edge6,Edge8]
FEATURE [Part::Cut] Cut007  label="bottom"
  Base = -> Fillet027
  Tool = -> Fillet028
FEATURE [Part::Feature] Part__Feature043  label="m3Nut001"
  Placement = pos=(6,-20.7844,81.9658) rot=(1,0,0;1.5708rad)
  shape: bbox 6.352 x 2.188 x 6.352 mm, 35 faces (baked)
FEATURE [Part::Cone] Cone001
  Angle = 360
  AttacherType = Attacher::AttachEngine3D
  Height = 8
  Placement = pos=(6,-24.5,-9) rot=(0,0.707107,0.707107;3.14159rad)
  Radius1 = 6
  Radius2 = 4
FEATURE [Part::Cone] Cone002
  Angle = 360
  AttacherType = Attacher::AttachEngine3D
  Height = 8
  Placement = pos=(6,-24.5,82) rot=(0,0.707107,0.707107;3.14159rad)
  Radius1 = 6
  Radius2 = 4
FEATURE [Part::Cone] Cone003
  Angle = 360
  AttacherType = Attacher::AttachEngine3D
  Height = 8
  Placement = pos=(72,-24.5,-9) rot=(0,0.707107,0.707107;3.14159rad)
  Radius1 = 6
  Radius2 = 4
FEATURE [Part::Cone] Cone004
  Angle = 360
  AttacherType = Attacher::AttachEngine3D
  Height = 8
  Placement = pos=(72,-24.5,82) rot=(0,0.707107,0.707107;3.14159rad)
  Radius1 = 6
  Radius2 = 4
FEATURE [Part::MultiFuse] Fusion043  label="m3NutsHolds"
  Shapes = -> [Cone001,Cone002,Cone003,Cone004]
FEATURE [Part::Feature] Part__Feature044  label="m3Nut002"
  Placement = pos=(72,-20.7844,81.9658) rot=(1,0,0;1.5708rad)
  shape: bbox 6.352 x 2.188 x 6.352 mm, 35 faces (baked)
FEATURE [Part::Feature] Part__Feature045  label="m3Nut003"
  Placement = pos=(72,-20.7844,-9.03425) rot=(1,0,0;1.5708rad)
  shape: bbox 6.352 x 2.188 x 6.352 mm, 35 faces (baked)
FEATURE [Part::Feature] Part__Feature046  label="m3Nut004"
  Placement = pos=(6,-20.7844,-9.03425) rot=(1,0,0;1.5708rad)
  shape: bbox 6.352 x 2.188 x 6.352 mm, 35 faces (baked)
FEATURE [Sketcher::SketchObject] Sketch009
  FullyConstrained = true
  sketch-geometry (10):
    g0: LineSegment StartX=71 StartY=-3 StartZ=0 EndX=71 EndY=-22 EndZ=0
    g1: LineSegment StartX=71 StartY=-22 StartZ=0 EndX=66 EndY=-22 EndZ=0
    g2: LineSegment StartX=66 StartY=-22 StartZ=0 EndX=66 EndY=-3 EndZ=0
    g3: LineSegment StartX=66 StartY=-3 StartZ=0 EndX=12 EndY=-3 EndZ=0
    g4: LineSegment StartX=12 StartY=-3 StartZ=0 EndX=12 EndY=-22 EndZ=0
    g5: LineSegment StartX=12 StartY=-22 StartZ=0 EndX=7 EndY=-22 EndZ=0
    g6: LineSegment StartX=7 StartY=-3 StartZ=0 EndX=7 EndY=-22 EndZ=0
    g7: ArcOfCircle CenterX=12 CenterY=-3 CenterZ=0 NormalX=0 NormalY=0 NormalZ=1 AngleXU=0 Radius=5 StartAngle=1.5708 EndAngle=3.14159
    g8: ArcOfCircle CenterX=66 CenterY=-3 CenterZ=0 NormalX=0 NormalY=0 NormalZ=1 AngleXU=0 Radius=5 StartAngle=-2.7e-15 EndAngle=1.5708
    g9: LineSegment StartX=12 StartY=2 StartZ=0 EndX=66 EndY=2 EndZ=0
  constraints (30):
    c: Vertical(g0)
    c: Coincident(g1,g0)
    c: Horizontal(g1)
    c: Coincident(g2,g1)
    c: Vertical(g2)
    c: Horizontal(g3)
    c: Vertical(g4)
    c: Horizontal(g5)
    c: Coincident(g6,g5)
    c: Vertical(g6)
    c: Coincident(g5,g4)
    c: DistanceX(g-1,g6) = 7
    c: DistanceX(g6,g3) = 5
    c: Coincident(g4,g3)
    c: Coincident(g3,g2)
    c: DistanceY(g5,g6) = 19
    c: DistanceY(g1,g2) = 19
    c: Coincident(g7,g3)
    c: Coincident(g7,g6)
    c: Coincident(g8,g2)
    c: Angle(g7) = 1.5708
    c: Angle(g8) = 1.5708
    c: Coincident(g9,g7)
    c: Coincident(g9,g8)
    c: Horizontal(g9)
    c: DistanceX(g3,g2) = 54
    c: DistanceX(g8,g2) = 0
    c: DistanceY(g3) = -3
    c: DistanceY(g6,g3) = 0
    c: Coincident(g0,g8)
FEATURE [Part::Extrusion] Extrude007
  Base = -> Sketch009
  Dir = (0,0,1)
  DirMode = 2
  FaceMakerClass = Part::FaceMakerBullseye
  LengthFwd = 3
  LengthRev = 0
  Placement = pos=(0,0,84.75) rot=(0,0,1;0rad)
  Solid = true
  Symmetric = false
FEATURE [Part::Fillet] Fillet029  label="capHoldBottom"
  Base = -> Extrude007
  Edges = 19 edges r=1: [Edge2,Edge3,Edge5,Edge6,Edge8,Edge9,Edge10,Edge11,Edge12,Edge13,Edge14,Edge15,Edge16,Edge17,Edge18,Edge21,Edge24,Edge27,Edge29]
FEATURE [Part::Feature] Part__Feature047  label="m3Nut005"
  Placement = pos=(72,-13.2844,81.9658) rot=(1,0,0;1.5708rad)
  shape: bbox 6.352 x 2.188 x 6.352 mm, 35 faces (baked)
FEATURE [Part::FeaturePython] Clone  label="m3NutCuts"  # Draft clone (typed FeaturePython)
  AttacherType = Attacher::AttachEngine3D
  Fuse = false
  Objects = -> [Part__Feature047]
  Placement = pos=(72,-13.2844,81.9658) rot=(1,0,0;1.5708rad)
  Scale = (1.05,1.05,1.05)
FEATURE [Part::Cylinder] Cylinder032  label="laceHold"
  Angle = 90
  AttacherType = Attacher::AttachEngine3D
  FirstAngle = 0
  Height = 72
  Placement = pos=(3,24,87.75) rot=(0.57735,-0.57735,0.57735;4.18879rad)
  Radius = 6
  SecondAngle = 0
FEATURE [Part::FeaturePython] Tube  # WARN: FeaturePython — macro-defined, semantics opaque (R4)
  AttacherType = Attacher::AttachEngine3D
  Height = 10
  InnerRadius = 6
  OuterRadius = 7.5
  Placement = pos=(34,24,87.75) rot=(0.57735,-0.57735,0.57735;4.18879rad)
FEATURE [Part::FeaturePython] Tube001  # WARN: FeaturePython — macro-defined, semantics opaque (R4)
  AttacherType = Attacher::AttachEngine3D
  Height = 10
  InnerRadius = 6
  OuterRadius = 7.5
  Placement = pos=(56,24,87.75) rot=(0.57735,-0.57735,0.57735;4.18879rad)
FEATURE [Part::FeaturePython] Tube002  # WARN: FeaturePython — macro-defined, semantics opaque (R4)
  AttacherType = Attacher::AttachEngine3D
  Height = 10
  InnerRadius = 6
  OuterRadius = 7.5
  Placement = pos=(12,24,87.75) rot=(0.57735,-0.57735,0.57735;4.18879rad)
FEATURE [Part::MultiFuse] Fusion044  label="laceCuts"
  Shapes = -> [Tube,Tube001,Tube002]
FEATURE [Part::Box] Box026  label="Cube025"
  AttacherType = Attacher::AttachEngine3D
  Height = 102.5
  Length = 79
  Placement = pos=(-0.5,-26,-14.25) rot=(0,0,1;0rad)
  Width = 2
FEATURE [Part::Fillet] Fillet030  label="topRidge"
  Base = -> Box026
  Edges = 4 edges r=10: [Edge2,Edge4,Edge6,Edge8]
  Placement = pos=(0,0.5,0) rot=(0,0,1;0rad)
FEATURE [Part::Box] Box027  label="Cube026"
  AttacherType = Attacher::AttachEngine3D
  Height = 99.5
  Length = 76
  Placement = pos=(1,-26,-13.25) rot=(0,0,1;0rad)
  Width = 2
FEATURE [Part::Fillet] Fillet031  label="topRidge001"
  Base = -> Box027
  Edges = 4 edges r=10: [Edge2,Edge4,Edge6,Edge8]
  Placement = pos=(0,0.5,0) rot=(0,0,1;0rad)
FEATURE [Part::Cut] Cut008
  Base = -> Fillet030
  Tool = -> Fillet031
FEATURE [Part::Fillet] Fillet032  label="ridge"
  Base = -> Cut008
  Edges = 16 edges r=0.25: [Edge3,Edge21,Edge22,Edge23,Edge24,Edge25,Edge26,Edge27,Edge28,Edge29,Edge30,Edge31,Edge32,Edge33,Edge34,Edge35]
FEATURE [Sketcher::SketchObject] Sketch010
  FullyConstrained = false
  Placement = pos=(0,0,0) rot=(1,0,0;1.5708rad)
  sketch-geometry (5):
    g0: LineSegment StartX=3 StartY=-10.7679 StartZ=0 EndX=6 EndY=-12.5 EndZ=0
    g1: LineSegment StartX=6 StartY=-12.5 StartZ=0 EndX=9 EndY=-10.7679 EndZ=0
    g2: LineSegment StartX=9 StartY=-10.7679 StartZ=0 EndX=9 EndY=-0.98215 EndZ=0
    g3: LineSegment StartX=3 StartY=-0.98215 StartZ=0 EndX=3 EndY=-10.7679 EndZ=0
    g4: LineSegment StartX=3 StartY=-0.98215 StartZ=0 EndX=9 EndY=-0.98215 EndZ=0
  constraints (14):
    c: Coincident(g1,g0)
    c: Coincident(g2,g1)
    c: Vertical(g2)
    c: Vertical(g3)
    c: Coincident(g3,g0)
    c: DistanceX(g0,g0) = 3
    c: DistanceX(g0,g1) = 3
    c: Angle(g1,g0) = 2.0944
    c: DistanceX(g0) = 6
    c: DistanceY(g0) = -12.5
    c: DistanceY(g0,g1) = 0
    c: Coincident(g4,g3)
    c: Coincident(g4,g2)
    c: Horizontal(g4)
FEATURE [Part::Extrusion] Extrude008  label="m3NutCut"
  Base = -> Sketch010
  Dir = (0,-1,-3e-16)
  DirMode = 2
  FaceMakerClass = Part::FaceMakerBullseye
  LengthFwd = 2
  LengthRev = 0
  Placement = pos=(0,-19.75,0) rot=(0,0,1;0rad)
  Solid = true
  Symmetric = false
FEATURE [Sketcher::SketchObject] Sketch011
  FullyConstrained = false
  Placement = pos=(0,0,0) rot=(1,0,0;1.5708rad)
  sketch-geometry (5):
    g0: LineSegment StartX=3 StartY=-10.7679 StartZ=0 EndX=6 EndY=-12.5 EndZ=0
    g1: LineSegment StartX=6 StartY=-12.5 StartZ=0 EndX=9 EndY=-10.7679 EndZ=0
    g2: LineSegment StartX=9 StartY=-10.7679 StartZ=0 EndX=9 EndY=-0.98215 EndZ=0
    g3: LineSegment StartX=3 StartY=-0.98215 StartZ=0 EndX=3 EndY=-10.7679 EndZ=0
    g4: LineSegment StartX=3 StartY=-0.98215 StartZ=0 EndX=9 EndY=-0.98215 EndZ=0
  constraints (14):
    c: Coincident(g1,g0)
    c: Coincident(g2,g1)
    c: Vertical(g2)
    c: Vertical(g3)
    c: Coincident(g3,g0)
    c: DistanceX(g0,g0) = 3
    c: DistanceX(g0,g1) = 3
    c: Angle(g1,g0) = 2.0944
    c: DistanceX(g0) = 6
    c: DistanceY(g0) = -12.5
    c: DistanceY(g0,g1) = 0
    c: Coincident(g4,g3)
    c: Coincident(g4,g2)
    c: Horizontal(g4)
FEATURE [Part::Extrusion] Extrude009  label="m3NutCut001"
  Base = -> Sketch011
  Dir = (0,-1,-3e-16)
  DirMode = 2
  FaceMakerClass = Part::FaceMakerBullseye
  LengthFwd = 2
  LengthRev = 0
  Placement = pos=(66,-19.75,0) rot=(0,0,1;0rad)
  Solid = true
  Symmetric = false
FEATURE [Part::MultiFuse] Fusion045
  Shapes = -> [Extrude009,Extrude008]
FEATURE [Part::Mirroring] Part__Mirroring009  label="Fusion045 (Mirror #10)"
  Base = (0,0,0)
  Normal = (0,0,1)
  Placement = pos=(0,0,73) rot=(0,0,1;0rad)
  Source = -> Fusion045
FEATURE [Part::MultiFuse] Fusion046  label="m3NutCutsBottom"
  Shapes = -> [Part__Mirroring009,Fusion045]
FEATURE [Part::Box] Box030  label="Cube029"
  AttacherType = Attacher::AttachEngine3D
  Height = 1.25
  Length = 3
  Placement = pos=(9.5,-19.75,-7) rot=(0,-1,0;1.5708rad)
  Width = 10
FEATURE [Part::Box] Box031  label="Cube030"
  AttacherType = Attacher::AttachEngine3D
  Height = 1.75
  Length = 3
  Placement = pos=(5.25,-23.75,-5.25) rot=(0,-1,0;1.5708rad)
  Width = 10
FEATURE [Part::MultiFuse] Fusion047  label="topCuts"
  Shapes = -> [Box031,Box030]
FEATURE [Mesh::Feature] tinker  label="Mints"
  Placement = pos=(42,-23.14,20) rot=(1,0,0;1.5708rad)
FEATURE [Sketcher::SketchObject] Sketch013
  FullyConstrained = false
  Placement = pos=(0,0,0) rot=(1,0,0;1.5708rad)
  sketch-geometry (884):
    g0: LineSegment StartX=35.7189 StartY=14.4677 StartZ=0 EndX=35.5415 EndY=14.2824 EndZ=0
    g1: LineSegment StartX=35.5415 StartY=14.2079 StartZ=0 EndX=35.4533 EndY=14.1342 EndZ=0
    g2: LineSegment StartX=35.4533 StartY=14.1342 StartZ=0 EndX=35.4583 EndY=14.0618 EndZ=0
    g3: LineSegment StartX=35.4583 StartY=14.0618 StartZ=0 EndX=35.3195 EndY=13.9216 EndZ=0
    g4: LineSegment StartX=35.3195 StartY=13.9216 StartZ=0 EndX=35.3195 EndY=13.853 EndZ=0
    g5: LineSegment StartX=35.3195 StartY=13.853 StartZ=0 EndX=35.248 EndY=13.7975 EndZ=0
    g6: LineSegment StartX=35.248 StartY=13.7975 StartZ=0 EndX=35.248 EndY=13.6573 EndZ=0
    g7: LineSegment StartX=35.248 StartY=13.6573 StartZ=0 EndX=35.1825 EndY=13.5912 EndZ=0
    g8: LineSegment StartX=35.1825 StartY=13.5912 StartZ=0 EndX=35.1825 EndY=13.2647 EndZ=0
    g9: LineSegment StartX=35.1825 StartY=13.2647 StartZ=0 EndX=35.0994 EndY=13.159 EndZ=0
    g10: LineSegment StartX=35.0994 StartY=13.159 StartZ=0 EndX=35.0994 EndY=13.0459 EndZ=0
    g11: LineSegment StartX=35.0994 StartY=13.0459 StartZ=0 EndX=35.0336 EndY=12.9565 EndZ=0
    g12: LineSegment StartX=35.0336 StartY=12.9565 StartZ=0 EndX=35.0336 EndY=12.3489 EndZ=0
    g13: LineSegment StartX=35.0336 StartY=12.3489 StartZ=0 EndX=35.1008 EndY=12.3489 EndZ=0
    g14: LineSegment StartX=35.1008 StartY=12.3489 StartZ=0 EndX=35.1008 EndY=12.2102 EndZ=0
    g15: LineSegment StartX=35.1008 StartY=12.2102 StartZ=0 EndX=35.1709 EndY=12.2072 EndZ=0
    g16: LineSegment StartX=35.1709 StartY=12.2072 StartZ=0 EndX=35.1709 EndY=11.9948 EndZ=0
    g17: LineSegment StartX=35.1709 StartY=11.9948 StartZ=0 EndX=35.2359 EndY=11.9948 EndZ=0
    g18: LineSegment StartX=35.2359 StartY=11.9948 StartZ=0 EndX=35.2359 EndY=11.9181 EndZ=0
    g19: LineSegment StartX=35.2359 StartY=11.9181 StartZ=0 EndX=35.3001 EndY=11.9181 EndZ=0
    g20: LineSegment StartX=35.3001 StartY=11.9181 StartZ=0 EndX=35.3001 EndY=11.8402 EndZ=0
    g21: LineSegment StartX=35.3001 StartY=11.8402 StartZ=0 EndX=35.3675 EndY=11.8402 EndZ=0
    g22: LineSegment StartX=35.3675 StartY=11.8402 StartZ=0 EndX=35.3675 EndY=11.2433 EndZ=0
    g23: LineSegment StartX=35.3675 StartY=11.2433 StartZ=0 EndX=35.435 EndY=11.2433 EndZ=0
    g24: LineSegment StartX=35.435 StartY=11.2433 StartZ=0 EndX=35.435 EndY=11.1727 EndZ=0
    g25: LineSegment StartX=35.435 StartY=11.1727 StartZ=0 EndX=35.5098 EndY=11.1727 EndZ=0
    g26: LineSegment StartX=35.5098 StartY=11.1727 StartZ=0 EndX=35.5098 EndY=11.1026 EndZ=0
    g27: LineSegment StartX=35.5098 StartY=11.1026 StartZ=0 EndX=35.6558 EndY=11.1026 EndZ=0
    g28: LineSegment StartX=35.6558 StartY=11.1026 StartZ=0 EndX=35.6558 EndY=11.0252 EndZ=0
    g29: LineSegment StartX=35.6558 StartY=11.0252 StartZ=0 EndX=35.7128 EndY=11.0252 EndZ=0
    g30: LineSegment StartX=35.7128 StartY=11.0252 StartZ=0 EndX=35.7128 EndY=10.7682 EndZ=0
    g31: LineSegment StartX=35.7128 StartY=10.7682 StartZ=0 EndX=35.7756 EndY=10.7681 EndZ=0
    g32: LineSegment StartX=35.7756 StartY=10.7681 StartZ=0 EndX=35.7756 EndY=10.5644 EndZ=0
    g33: LineSegment StartX=35.7756 StartY=10.5644 StartZ=0 EndX=35.846 EndY=10.5644 EndZ=0
    g34: LineSegment StartX=35.846 StartY=10.5644 StartZ=0 EndX=35.846 EndY=10.4767 EndZ=0
    g35: LineSegment StartX=35.846 StartY=10.4767 StartZ=0 EndX=35.988 EndY=10.4767 EndZ=0
    g36: LineSegment StartX=35.988 StartY=10.4767 StartZ=0 EndX=35.988 EndY=10.4228 EndZ=0
    g37: LineSegment StartX=35.988 StartY=10.4228 StartZ=0 EndX=36.1201 EndY=10.4228 EndZ=0
    g38: LineSegment StartX=36.1201 StartY=10.4228 StartZ=0 EndX=36.1201 EndY=10.2907 EndZ=0
    g39: LineSegment StartX=36.1201 StartY=10.2907 StartZ=0 EndX=36.1926 EndY=10.2907 EndZ=0
    g40: LineSegment StartX=36.1926 StartY=10.2907 StartZ=0 EndX=36.1926 EndY=10.1585 EndZ=0
    g41: LineSegment StartX=36.1926 StartY=10.1585 StartZ=0 EndX=36.2533 EndY=10.1585 EndZ=0
    g42: LineSegment StartX=36.2533 StartY=10.1585 StartZ=0 EndX=36.2533 EndY=10.0897 EndZ=0
    g43: LineSegment StartX=36.2533 StartY=10.0897 StartZ=0 EndX=36.3179 EndY=10.0897 EndZ=0
    g44: LineSegment StartX=36.3179 StartY=10.0897 StartZ=0 EndX=36.3179 EndY=9.8871 EndZ=0
    g45: LineSegment StartX=36.3179 StartY=9.8871 StartZ=0 EndX=36.3888 EndY=9.8871 EndZ=0
    g46: LineSegment StartX=36.3888 StartY=9.8871 StartZ=0 EndX=36.3888 EndY=9.73503 EndZ=0
    g47: LineSegment StartX=36.3888 StartY=9.73503 StartZ=0 EndX=36.4516 EndY=9.73503 EndZ=0
    g48: LineSegment StartX=36.4516 StartY=9.73503 StartZ=0 EndX=36.4516 EndY=9.65617 EndZ=0
    g49: LineSegment StartX=36.4516 StartY=9.65617 StartZ=0 EndX=36.6707 EndY=9.65617 EndZ=0
    g50: LineSegment StartX=36.6707 StartY=9.65617 StartZ=0 EndX=36.6707 EndY=9.58899 EndZ=0
    g51: LineSegment StartX=36.6707 StartY=9.58899 StartZ=0 EndX=36.7335 EndY=9.58899 EndZ=0
    g52: LineSegment StartX=36.7335 StartY=9.58899 StartZ=0 EndX=36.7335 EndY=9.51158 EndZ=0
    g53: LineSegment StartX=36.7335 StartY=9.51158 StartZ=0 EndX=36.7948 EndY=9.51158 EndZ=0
    g54: LineSegment StartX=36.7948 StartY=9.51158 StartZ=0 EndX=36.7948 EndY=9.40351 EndZ=0
    g55: LineSegment StartX=36.7948 StartY=9.40351 StartZ=0 EndX=36.8664 EndY=9.40351 EndZ=0
    g56: LineSegment StartX=36.8664 StartY=9.40351 StartZ=0 EndX=36.8664 EndY=9.2487 EndZ=0
    g57: LineSegment StartX=36.8664 StartY=9.2487 StartZ=0 EndX=36.9292 EndY=9.2487 EndZ=0
    g58: LineSegment StartX=36.9292 StartY=9.2487 StartZ=0 EndX=36.9292 EndY=9.18298 EndZ=0
    g59: LineSegment StartX=36.9292 StartY=9.18298 StartZ=0 EndX=37.0036 EndY=9.18298 EndZ=0
    g60: LineSegment StartX=37.0036 StartY=9.18298 StartZ=0 EndX=37.0036 EndY=9.12121 EndZ=0
    g61: LineSegment StartX=37.0036 StartY=9.12121 StartZ=0 EndX=37.066 EndY=9.12121 EndZ=0
    g62: LineSegment StartX=37.066 StartY=9.12121 StartZ=0 EndX=37.066 EndY=8.98122 EndZ=0
    g63: LineSegment StartX=37.066 StartY=8.98122 StartZ=0 EndX=37.1365 EndY=8.98122 EndZ=0
    g64: LineSegment StartX=37.1365 StartY=8.98122 StartZ=0 EndX=37.1365 EndY=8.85617 EndZ=0
    g65: LineSegment StartX=37.1365 StartY=8.85617 StartZ=0 EndX=37.2117 EndY=8.85617 EndZ=0
    g66: LineSegment StartX=37.2117 StartY=8.85617 StartZ=0 EndX=37.2117 EndY=8.77808 EndZ=0
    g67: LineSegment StartX=37.2117 StartY=8.77808 StartZ=0 EndX=37.276 EndY=8.7779 EndZ=0
    g68: LineSegment StartX=37.276 StartY=8.7779 StartZ=0 EndX=37.276 EndY=8.70839 EndZ=0
    g69: LineSegment StartX=37.276 StartY=8.70839 StartZ=0 EndX=37.3475 EndY=8.70839 EndZ=0
    g70: LineSegment StartX=37.3475 StartY=8.70839 StartZ=0 EndX=37.3475 EndY=8.58602 EndZ=0
    g71: LineSegment StartX=37.3475 StartY=8.58602 StartZ=0 EndX=37.4111 EndY=8.58602 EndZ=0
    g72: LineSegment StartX=37.4111 StartY=8.58602 StartZ=0 EndX=37.4111 EndY=8.50272 EndZ=0
    g73: LineSegment StartX=37.4111 StartY=8.50272 StartZ=0 EndX=37.4778 EndY=8.50272 EndZ=0
    g74: LineSegment StartX=37.4778 StartY=8.50272 StartZ=0 EndX=37.4778 EndY=8.37852 EndZ=0
    g75: LineSegment StartX=37.4778 StartY=8.37852 StartZ=0 EndX=37.55 EndY=8.37852 EndZ=0
    g76: LineSegment StartX=37.55 StartY=8.37852 StartZ=0 EndX=37.55 EndY=8.29594 EndZ=0
    g77: LineSegment StartX=37.55 StartY=8.29594 StartZ=0 EndX=37.6238 EndY=8.29594 EndZ=0
    g78: LineSegment StartX=37.6238 StartY=8.29594 StartZ=0 EndX=37.6238 EndY=8.20831 EndZ=0
    g79: LineSegment StartX=37.6238 StartY=8.20831 StartZ=0 EndX=37.6953 EndY=8.21123 EndZ=0
    g80: LineSegment StartX=37.6953 StartY=8.21123 StartZ=0 EndX=37.6953 EndY=8.14022 EndZ=0
    g81: LineSegment StartX=37.6953 StartY=8.14022 StartZ=0 EndX=37.7536 EndY=8.14414 EndZ=0
    g82: LineSegment StartX=37.7536 StartY=8.14414 StartZ=0 EndX=37.7574 EndY=8.06459 EndZ=0
    g83: LineSegment StartX=37.7574 StartY=8.06459 StartZ=0 EndX=37.8181 EndY=8.06459 EndZ=0
    g84: LineSegment StartX=37.8181 StartY=8.06459 StartZ=0 EndX=37.8216 EndY=7.98967 EndZ=0
    g85: LineSegment StartX=37.8216 StartY=7.98967 StartZ=0 EndX=38.1025 EndY=7.98967 EndZ=0
    g86: LineSegment StartX=38.1025 StartY=7.98967 StartZ=0 EndX=38.1917 EndY=8.08042 EndZ=0
    g87: LineSegment StartX=38.1917 StartY=8.08042 StartZ=0 EndX=38.2417 EndY=8.08577 EndZ=0
    g88: LineSegment StartX=38.2417 StartY=8.08577 StartZ=0 EndX=38.4557 EndY=8.32302 EndZ=0
    g89: LineSegment StartX=38.4557 StartY=8.32302 StartZ=0 EndX=38.5235 EndY=8.32302 EndZ=0
    g90: LineSegment StartX=38.5235 StartY=8.32302 StartZ=0 EndX=38.5887 EndY=8.40314 EndZ=0
    g91: LineSegment StartX=38.5887 StartY=8.40314 StartZ=0 EndX=38.6773 EndY=8.40314 EndZ=0
    g92: LineSegment StartX=38.6773 StartY=8.40314 StartZ=0 EndX=39.0643 EndY=8.80818 EndZ=0
    g93: LineSegment StartX=39.0643 StartY=8.80818 StartZ=0 EndX=39.152 EndY=8.80818 EndZ=0
    g94: LineSegment StartX=39.152 StartY=8.80818 StartZ=0 EndX=39.5355 EndY=9.19803 EndZ=0
    g95: LineSegment StartX=39.5355 StartY=9.19803 StartZ=0 EndX=39.6318 EndY=9.19803 EndZ=0
    g96: LineSegment StartX=39.6318 StartY=9.19803 StartZ=0 EndX=39.792 EndY=9.38195 EndZ=0
    g97: LineSegment StartX=39.792 StartY=9.38195 StartZ=0 EndX=39.7884 EndY=9.45608 EndZ=0
    g98: LineSegment StartX=39.7884 StartY=9.45608 StartZ=0 EndX=39.9772 EndY=9.63446 EndZ=0
    g99: LineSegment StartX=39.9772 StartY=9.63446 StartZ=0 EndX=39.9772 EndY=9.72533 EndZ=0
    g100: LineSegment StartX=39.9772 StartY=9.72533 StartZ=0 EndX=40.1697 EndY=9.91904 EndZ=0
    g101: LineSegment StartX=40.1697 StartY=9.91904 StartZ=0 EndX=40.1746 EndY=9.99558 EndZ=0
    g102: LineSegment StartX=40.1746 StartY=9.99558 StartZ=0 EndX=40.2388 EndY=10.0603 EndZ=0
    g103: LineSegment StartX=40.2388 StartY=10.0603 StartZ=0 EndX=40.2423 EndY=10.1261 EndZ=0
    g104: LineSegment StartX=40.2423 StartY=10.1261 StartZ=0 EndX=40.5948 EndY=10.4793 EndZ=0
    g105: LineSegment StartX=40.5948 StartY=10.4793 StartZ=0 EndX=40.5948 EndY=10.5499 EndZ=0
    g106: LineSegment StartX=40.5948 StartY=10.5499 StartZ=0 EndX=40.6701 EndY=10.618 EndZ=0
    g107: LineSegment StartX=40.6701 StartY=10.618 StartZ=0 EndX=40.6581 EndY=10.6527 EndZ=0
    g108: LineSegment StartX=40.6581 StartY=10.6527 StartZ=0 EndX=40.6988 EndY=10.6527 EndZ=0
    g109: LineSegment StartX=40.6988 StartY=10.6527 StartZ=0 EndX=40.9317 EndY=10.8877 EndZ=0
    g110: LineSegment StartX=40.9317 StartY=10.8877 StartZ=0 EndX=40.9317 EndY=10.9592 EndZ=0
    g111: LineSegment StartX=40.9317 StartY=10.9592 StartZ=0 EndX=41.0136 EndY=11.0405 EndZ=0
    g112: LineSegment StartX=41.0136 StartY=11.0405 StartZ=0 EndX=41.0068 EndY=11.1648 EndZ=0
    g113: LineSegment StartX=41.0068 StartY=11.1648 StartZ=0 EndX=41.0763 EndY=11.2275 EndZ=0
    g114: LineSegment StartX=41.0763 StartY=11.2275 StartZ=0 EndX=41.0723 EndY=11.2979 EndZ=0
    g115: LineSegment StartX=41.0723 StartY=11.2979 StartZ=0 EndX=41.15 EndY=11.3821 EndZ=0
    g116: LineSegment StartX=41.15 StartY=11.3821 StartZ=0 EndX=41.15 EndY=11.5724 EndZ=0
    g117: LineSegment StartX=41.15 StartY=11.5724 StartZ=0 EndX=41.2317 EndY=11.6351 EndZ=0
    g118: LineSegment StartX=41.2317 StartY=11.6351 StartZ=0 EndX=41.2155 EndY=11.7717 EndZ=0
    g119: LineSegment StartX=41.2155 StartY=11.7717 StartZ=0 EndX=41.2837 EndY=11.8432 EndZ=0
    g120: LineSegment StartX=41.2837 StartY=11.8432 StartZ=0 EndX=41.2786 EndY=11.8698 EndZ=0
    g121: LineSegment StartX=41.2786 StartY=11.8698 StartZ=0 EndX=41.3138 EndY=11.8698 EndZ=0
    g122: LineSegment StartX=41.3138 StartY=11.8698 StartZ=0 EndX=41.5455 EndY=12.1045 EndZ=0
    g123: LineSegment StartX=41.5455 StartY=12.1045 StartZ=0 EndX=41.5618 EndY=12.4305 EndZ=0
    g124: LineSegment StartX=41.5618 StartY=12.4305 StartZ=0 EndX=41.6277 EndY=12.505 EndZ=0
    g125: LineSegment StartX=41.6277 StartY=12.505 StartZ=0 EndX=41.6277 EndY=12.6108 EndZ=0
    g126: LineSegment StartX=41.6277 StartY=12.6108 StartZ=0 EndX=41.692 EndY=12.5393 EndZ=0
    g127: LineSegment StartX=41.692 StartY=12.5393 StartZ=0 EndX=41.7679 EndY=12.5393 EndZ=0
    g128: LineSegment StartX=41.7679 StartY=12.5393 StartZ=0 EndX=41.7679 EndY=12.4516 EndZ=0
    g129: LineSegment StartX=41.7679 StartY=12.4516 StartZ=0 EndX=41.8336 EndY=12.4546 EndZ=0
    g130: LineSegment StartX=41.8336 StartY=12.4546 StartZ=0 EndX=41.8336 EndY=12.3903 EndZ=0
    g131: LineSegment StartX=41.8336 StartY=12.3903 StartZ=0 EndX=41.8935 EndY=12.3903 EndZ=0
    g132: LineSegment StartX=41.8935 StartY=12.3903 StartZ=0 EndX=41.8935 EndY=12.3173 EndZ=0
    g133: LineSegment StartX=41.8935 StartY=12.3173 StartZ=0 EndX=41.9592 EndY=12.3217 EndZ=0
    g134: LineSegment StartX=41.9592 StartY=12.3217 StartZ=0 EndX=41.9651 EndY=12.2501 EndZ=0
    g135: LineSegment StartX=41.9651 StartY=12.2501 StartZ=0 EndX=42.0235 EndY=12.2559 EndZ=0
    g136: LineSegment StartX=42.0235 StartY=12.2559 StartZ=0 EndX=42.0264 EndY=12.1829 EndZ=0
    g137: LineSegment StartX=42.0264 StartY=12.1829 StartZ=0 EndX=42.1067 EndY=12.1888 EndZ=0
    g138: LineSegment StartX=42.1067 StartY=12.1888 StartZ=0 EndX=42.1067 EndY=12.1143 EndZ=0
    g139: LineSegment StartX=42.1067 StartY=12.1143 StartZ=0 EndX=42.2426 EndY=12.1216 EndZ=0
    g140: LineSegment StartX=42.2426 StartY=12.1216 StartZ=0 EndX=42.2426 EndY=12.0413 EndZ=0
    g141: LineSegment StartX=42.2426 StartY=12.0413 StartZ=0 EndX=42.4427 EndY=12.0413 EndZ=0
    g142: LineSegment StartX=42.4427 StartY=12.0413 StartZ=0 EndX=42.45 EndY=11.9566 EndZ=0
    g143: LineSegment StartX=42.45 StartY=11.9566 StartZ=0 EndX=42.523 EndY=11.9639 EndZ=0
    g144: LineSegment StartX=42.523 StartY=11.9639 StartZ=0 EndX=42.5274 EndY=11.8952 EndZ=0
    g145: LineSegment StartX=42.5274 StartY=11.8952 StartZ=0 EndX=42.5931 EndY=11.9011 EndZ=0
    g146: LineSegment StartX=42.5931 StartY=11.9011 StartZ=0 EndX=42.5931 EndY=11.847 EndZ=0
    g147: LineSegment StartX=42.5931 StartY=11.847 StartZ=0 EndX=42.6457 EndY=11.8499 EndZ=0
    g148: LineSegment StartX=42.6457 StartY=11.8499 StartZ=0 EndX=42.6457 EndY=11.7886 EndZ=0
    g149: LineSegment StartX=42.6457 StartY=11.7886 StartZ=0 EndX=42.7844 EndY=11.7886 EndZ=0
    g150: LineSegment StartX=42.7844 StartY=11.7886 StartZ=0 EndX=42.7844 EndY=11.7131 EndZ=0
    g151: LineSegment StartX=42.7844 StartY=11.7131 StartZ=0 EndX=43.0642 EndY=11.7131 EndZ=0
    g152: LineSegment StartX=43.0642 StartY=11.7131 StartZ=0 EndX=43.0642 EndY=11.6357 EndZ=0
    g153: LineSegment StartX=43.0642 StartY=11.6357 StartZ=0 EndX=43.1985 EndY=11.6357 EndZ=0
    g154: LineSegment StartX=43.1985 StartY=11.6357 StartZ=0 EndX=43.1985 EndY=11.5714 EndZ=0
    g155: LineSegment StartX=43.1985 StartY=11.5714 StartZ=0 EndX=43.2613 EndY=11.5714 EndZ=0
    g156: LineSegment StartX=43.2613 StartY=11.5714 StartZ=0 EndX=43.2613 EndY=11.5086 EndZ=0
    g157: LineSegment StartX=43.2613 StartY=11.5086 StartZ=0 EndX=43.3285 EndY=11.5086 EndZ=0
    g158: LineSegment StartX=43.3285 StartY=11.5086 StartZ=0 EndX=43.3285 EndY=11.4327 EndZ=0
    g159: LineSegment StartX=43.3285 StartY=11.4327 StartZ=0 EndX=43.3913 EndY=11.4371 EndZ=0
    g160: LineSegment StartX=43.3913 StartY=11.4371 StartZ=0 EndX=43.3932 EndY=11.3717 EndZ=0
    g161: LineSegment StartX=43.3932 StartY=11.3717 StartZ=0 EndX=43.7436 EndY=11.3717 EndZ=0
    g162: LineSegment StartX=43.7436 StartY=11.3717 StartZ=0 EndX=43.7436 EndY=11.3021 EndZ=0
    g163: LineSegment StartX=43.7436 StartY=11.3021 StartZ=0 EndX=43.8098 EndY=11.3021 EndZ=0
    g164: LineSegment StartX=43.8098 StartY=11.3021 StartZ=0 EndX=43.8134 EndY=11.2285 EndZ=0
    g165: LineSegment StartX=43.8134 StartY=11.2285 StartZ=0 EndX=44.0238 EndY=11.2285 EndZ=0
    g166: LineSegment StartX=44.0238 StartY=11.2285 StartZ=0 EndX=44.0238 EndY=11.1603 EndZ=0
    g167: LineSegment StartX=44.0238 StartY=11.1603 StartZ=0 EndX=44.1542 EndY=11.1603 EndZ=0
    g168: LineSegment StartX=44.1542 StartY=11.1603 StartZ=0 EndX=44.1506 EndY=11.0922 EndZ=0
    g169: LineSegment StartX=44.1506 StartY=11.0922 StartZ=0 EndX=44.2845 EndY=11.1005 EndZ=0
    g170: LineSegment StartX=44.2845 StartY=11.1005 StartZ=0 EndX=44.2845 EndY=11.0276 EndZ=0
    g171: LineSegment StartX=44.2845 StartY=11.0276 StartZ=0 EndX=44.3538 EndY=11.0312 EndZ=0
    g172: LineSegment StartX=44.3538 StartY=11.0312 StartZ=0 EndX=44.3538 EndY=10.9534 EndZ=0
    g173: LineSegment StartX=44.3538 StartY=10.9534 StartZ=0 EndX=44.4925 EndY=10.9534 EndZ=0
    g174: LineSegment StartX=44.4925 StartY=10.9534 StartZ=0 EndX=44.4925 EndY=10.9066 EndZ=0
    g175: LineSegment StartX=44.4925 StartY=10.9066 StartZ=0 EndX=44.8405 EndY=10.9066 EndZ=0
    g176: LineSegment StartX=44.8405 StartY=10.9066 StartZ=0 EndX=44.8405 EndY=10.8227 EndZ=0
    g177: LineSegment StartX=44.8405 StartY=10.8227 StartZ=0 EndX=44.9671 EndY=10.8245 EndZ=0
    g178: LineSegment StartX=44.9671 StartY=10.8245 StartZ=0 EndX=44.9671 EndY=10.7496 EndZ=0
    g179: LineSegment StartX=44.9671 StartY=10.7496 StartZ=0 EndX=45.2382 EndY=10.7496 EndZ=0
    g180: LineSegment StartX=45.2382 StartY=10.7496 StartZ=0 EndX=45.2382 EndY=10.6783 EndZ=0
    g181: LineSegment StartX=45.2382 StartY=10.6783 StartZ=0 EndX=45.438 EndY=10.6783 EndZ=0
    g182: LineSegment StartX=45.438 StartY=10.6783 StartZ=0 EndX=45.438 EndY=10.6176 EndZ=0
    g183: LineSegment StartX=45.438 StartY=10.6176 StartZ=0 EndX=45.8572 EndY=10.6176 EndZ=0
    g184: LineSegment StartX=45.8572 StartY=10.6176 StartZ=0 EndX=45.8572 EndY=10.548 EndZ=0
    g185: LineSegment StartX=45.8572 StartY=10.548 StartZ=0 EndX=46.2711 EndY=10.548 EndZ=0
    g186: LineSegment StartX=46.2711 StartY=10.548 StartZ=0 EndX=46.5712 EndY=10.876 EndZ=0
    g187: LineSegment StartX=46.5712 StartY=10.876 StartZ=0 EndX=46.568 EndY=10.9537 EndZ=0
    g188: LineSegment StartX=46.568 StartY=10.9537 StartZ=0 EndX=46.6513 EndY=11.0387 EndZ=0
    g189: LineSegment StartX=46.6513 StartY=11.0387 StartZ=0 EndX=46.6513 EndY=11.2162 EndZ=0
    g190: LineSegment StartX=46.6513 StartY=11.2162 StartZ=0 EndX=46.7535 EndY=11.317 EndZ=0
    g191: LineSegment StartX=46.7535 StartY=11.317 StartZ=0 EndX=46.7462 EndY=11.4353 EndZ=0
    g192: LineSegment StartX=46.7462 StartY=11.4353 StartZ=0 EndX=46.8178 EndY=11.5141 EndZ=0
    g193: LineSegment StartX=46.8178 StartY=11.5141 StartZ=0 EndX=46.8081 EndY=11.636 EndZ=0
    g194: LineSegment StartX=46.8081 StartY=11.636 StartZ=0 EndX=46.8919 EndY=11.7287 EndZ=0
    g195: LineSegment StartX=46.8919 StartY=11.7287 StartZ=0 EndX=46.8919 EndY=11.9142 EndZ=0
    g196: LineSegment StartX=46.8919 StartY=11.9142 StartZ=0 EndX=46.9704 EndY=12.0106 EndZ=0
    g197: LineSegment StartX=46.9704 StartY=12.0106 StartZ=0 EndX=46.9704 EndY=13.0147 EndZ=0
    g198: LineSegment StartX=46.9704 StartY=13.0147 StartZ=0 EndX=47.1435 EndY=13.1957 EndZ=0
    g199: LineSegment StartX=47.1435 StartY=13.1957 StartZ=0 EndX=47.1435 EndY=13.5812 EndZ=0
    g200: LineSegment StartX=47.1435 StartY=13.5812 StartZ=0 EndX=47.0232 EndY=13.5812 EndZ=0
    g201: LineSegment StartX=47.0232 StartY=13.5812 StartZ=0 EndX=47.0232 EndY=13.968 EndZ=0
    g202: LineSegment StartX=47.0232 StartY=13.968 StartZ=0 EndX=46.9387 EndY=13.981 EndZ=0
    g203: LineSegment StartX=46.9387 StartY=13.981 StartZ=0 EndX=46.9387 EndY=14.1923 EndZ=0
    g204: LineSegment StartX=46.9387 StartY=14.1923 StartZ=0 EndX=46.8607 EndY=14.189 EndZ=0
    g205: LineSegment StartX=46.8607 StartY=14.189 StartZ=0 EndX=46.8607 EndY=14.2768 EndZ=0
    g206: LineSegment StartX=46.8607 StartY=14.2768 StartZ=0 EndX=46.9745 EndY=14.4003 EndZ=0
    g207: LineSegment StartX=46.9745 StartY=14.4003 StartZ=0 EndX=46.9842 EndY=14.6473 EndZ=0
    g208: LineSegment StartX=46.9842 StartY=14.6473 StartZ=0 EndX=46.8672 EndY=14.6603 EndZ=0
    g209: LineSegment StartX=46.8672 StartY=14.6603 StartZ=0 EndX=46.8672 EndY=14.8066 EndZ=0
    g210: LineSegment StartX=46.8672 StartY=14.8066 StartZ=0 EndX=46.799 EndY=14.8131 EndZ=0
    g211: LineSegment StartX=46.799 StartY=14.8131 StartZ=0 EndX=46.7957 EndY=14.8846 EndZ=0
    g212: LineSegment StartX=46.7957 StartY=14.8846 StartZ=0 EndX=46.7372 EndY=14.8911 EndZ=0
    g213: LineSegment StartX=46.7372 StartY=14.8911 StartZ=0 EndX=46.7502 EndY=15.0699 EndZ=0
    g214: LineSegment StartX=46.7502 StartY=15.0699 StartZ=0 EndX=46.6592 EndY=15.0764 EndZ=0
    g215: LineSegment StartX=46.6592 StartY=15.0764 StartZ=0 EndX=46.6592 EndY=15.2096 EndZ=0
    g216: LineSegment StartX=46.6592 StartY=15.2096 StartZ=0 EndX=46.7535 EndY=15.2811 EndZ=0
    g217: LineSegment StartX=46.7535 StartY=15.2811 StartZ=0 EndX=47.5498 EndY=15.2811 EndZ=0
    g218: LineSegment StartX=47.5498 StartY=15.2811 StartZ=0 EndX=47.5498 EndY=15.2015 EndZ=0
    g219: LineSegment StartX=47.5498 StartY=15.2015 StartZ=0 EndX=48.1326 EndY=15.2015 EndZ=0
    g220: LineSegment StartX=48.1326 StartY=15.2015 StartZ=0 EndX=48.1915 EndY=15.2887 EndZ=0
    g221: LineSegment StartX=48.1915 StartY=15.2887 StartZ=0 EndX=48.2811 EndY=15.2887 EndZ=0
    g222: LineSegment StartX=48.2811 StartY=15.2887 StartZ=0 EndX=48.4046 EndY=15.4194 EndZ=0
    g223: LineSegment StartX=48.4046 StartY=15.4194 StartZ=0 EndX=48.6512 EndY=15.4194 EndZ=0
    g224: LineSegment StartX=48.6512 StartY=15.4194 StartZ=0 EndX=48.6512 EndY=15.3322 EndZ=0
    g225: LineSegment StartX=48.6512 StartY=15.3322 StartZ=0 EndX=48.9084 EndY=15.3322 EndZ=0
    g226: LineSegment StartX=48.9084 StartY=15.3322 StartZ=0 EndX=48.9084 EndY=15.2647 EndZ=0
    g227: LineSegment StartX=48.9084 StartY=15.2647 StartZ=0 EndX=49.1131 EndY=15.2647 EndZ=0
    g228: LineSegment StartX=49.1131 StartY=15.2647 StartZ=0 EndX=49.1131 EndY=15.171 EndZ=0
    g229: LineSegment StartX=49.1131 StartY=15.171 StartZ=0 EndX=49.344 EndY=15.171 EndZ=0
    g230: LineSegment StartX=49.344 StartY=15.171 StartZ=0 EndX=49.4317 EndY=15.2779 EndZ=0
    g231: LineSegment StartX=49.4317 StartY=15.2779 StartZ=0 EndX=49.513 EndY=15.2714 EndZ=0
    g232: LineSegment StartX=49.513 StartY=15.2714 StartZ=0 EndX=49.6365 EndY=15.4177 EndZ=0
    g233: LineSegment StartX=49.6365 StartY=15.4177 StartZ=0 EndX=51.1609 EndY=15.4177 EndZ=0
    g234: LineSegment StartX=51.1609 StartY=15.4177 StartZ=0 EndX=51.2713 EndY=15.4747 EndZ=0
    g235: LineSegment StartX=51.2713 StartY=15.4747 StartZ=0 EndX=51.8707 EndY=15.4747 EndZ=0
    g236: LineSegment StartX=51.8707 StartY=15.4747 StartZ=0 EndX=51.9501 EndY=15.5501 EndZ=0
    g237: LineSegment StartX=51.9501 StartY=15.5501 StartZ=0 EndX=52.0613 EndY=15.5501 EndZ=0
    g238: LineSegment StartX=52.0613 StartY=15.5501 StartZ=0 EndX=52.1566 EndY=15.6335 EndZ=0
    g239: LineSegment StartX=52.1566 StartY=15.6335 StartZ=0 EndX=53.0776 EndY=15.6335 EndZ=0
    g240: LineSegment StartX=53.0776 StartY=15.6335 StartZ=0 EndX=53.2557 EndY=15.8082 EndZ=0
    g241: LineSegment StartX=53.2557 StartY=15.8082 StartZ=0 EndX=53.2557 EndY=16.103 EndZ=0
    g242: LineSegment StartX=53.2557 StartY=16.103 StartZ=0 EndX=53.1958 EndY=16.103 EndZ=0
    g243: LineSegment StartX=53.1958 StartY=16.103 StartZ=0 EndX=53.1958 EndY=16.3046 EndZ=0
    g244: LineSegment StartX=53.1958 StartY=16.3046 StartZ=0 EndX=53.1301 EndY=16.3017 EndZ=0
    g245: LineSegment StartX=53.1301 StartY=16.3017 StartZ=0 EndX=53.1301 EndY=16.4404 EndZ=0
    g246: LineSegment StartX=53.1301 StartY=16.4404 StartZ=0 EndX=53.0594 EndY=16.4404 EndZ=0
    g247: LineSegment StartX=53.0594 StartY=16.4404 StartZ=0 EndX=53.0558 EndY=16.5171 EndZ=0
    g248: LineSegment StartX=53.0558 StartY=16.5171 StartZ=0 EndX=52.9773 EndY=16.5171 EndZ=0
    g249: LineSegment StartX=52.9773 StartY=16.5171 StartZ=0 EndX=52.9773 EndY=16.6455 EndZ=0
    g250: LineSegment StartX=52.9773 StartY=16.6455 StartZ=0 EndX=52.9219 EndY=16.6452 EndZ=0
    g251: LineSegment StartX=52.9219 StartY=16.6452 StartZ=0 EndX=52.9219 EndY=16.7146 EndZ=0
    g252: LineSegment StartX=52.9219 StartY=16.7146 StartZ=0 EndX=52.8549 EndY=16.7146 EndZ=0
    g253: LineSegment StartX=52.8549 StartY=16.7146 StartZ=0 EndX=52.8535 EndY=16.7863 EndZ=0
    g254: LineSegment StartX=52.8535 StartY=16.7863 StartZ=0 EndX=52.7868 EndY=16.7863 EndZ=0
    g255: LineSegment StartX=52.7868 StartY=16.7863 StartZ=0 EndX=52.7868 EndY=16.9211 EndZ=0
    g256: LineSegment StartX=52.7868 StartY=16.9211 StartZ=0 EndX=52.715 EndY=16.9211 EndZ=0
    g257: LineSegment StartX=52.715 StartY=16.9211 StartZ=0 EndX=52.715 EndY=16.98 EndZ=0
    g258: LineSegment StartX=52.715 StartY=16.98 StartZ=0 EndX=52.6457 EndY=16.98 EndZ=0
    g259: LineSegment StartX=52.6457 StartY=16.98 StartZ=0 EndX=52.6457 EndY=17.0366 EndZ=0
    g260: LineSegment StartX=52.6457 StartY=17.0366 StartZ=0 EndX=52.5763 EndY=17.0366 EndZ=0
    g261: LineSegment StartX=52.5763 StartY=17.0366 StartZ=0 EndX=52.5763 EndY=17.128 EndZ=0
    g262: LineSegment StartX=52.5763 StartY=17.128 StartZ=0 EndX=52.5147 EndY=17.128 EndZ=0
    g263: LineSegment StartX=52.5147 StartY=17.128 StartZ=0 EndX=52.5147 EndY=17.2695 EndZ=0
    g264: LineSegment StartX=52.5147 StartY=17.2695 StartZ=0 EndX=52.4502 EndY=17.2647 EndZ=0
    g265: LineSegment StartX=52.4502 StartY=17.2647 StartZ=0 EndX=52.4454 EndY=17.336 EndZ=0
    g266: LineSegment StartX=52.4454 StartY=17.336 StartZ=0 EndX=52.3797 EndY=17.3384 EndZ=0
    g267: LineSegment StartX=52.3797 StartY=17.3384 StartZ=0 EndX=52.3829 EndY=17.4058 EndZ=0
    g268: LineSegment StartX=52.3829 StartY=17.4058 StartZ=0 EndX=52.318 EndY=17.4026 EndZ=0
    g269: LineSegment StartX=52.318 StartY=17.4026 StartZ=0 EndX=52.318 EndY=17.4715 EndZ=0
    g270: LineSegment StartX=52.318 StartY=17.4715 StartZ=0 EndX=52.2451 EndY=17.4715 EndZ=0
    g271: LineSegment StartX=52.2451 StartY=17.4715 StartZ=0 EndX=52.2451 EndY=17.5364 EndZ=0
    g272: LineSegment StartX=52.2451 StartY=17.5364 StartZ=0 EndX=52.1833 EndY=17.5388 EndZ=0
    g273: LineSegment StartX=52.1833 StartY=17.5388 StartZ=0 EndX=52.1833 EndY=17.6077 EndZ=0
    g274: LineSegment StartX=52.1833 StartY=17.6077 StartZ=0 EndX=52.1144 EndY=17.6077 EndZ=0
    g275: LineSegment StartX=52.1144 StartY=17.6077 StartZ=0 EndX=52.1144 EndY=17.6741 EndZ=0
    g276: LineSegment StartX=52.1144 StartY=17.6741 StartZ=0 EndX=52.0495 EndY=17.6741 EndZ=0
    g277: LineSegment StartX=52.0495 StartY=17.6741 StartZ=0 EndX=52.0495 EndY=17.7495 EndZ=0
    g278: LineSegment StartX=52.0495 StartY=17.7495 StartZ=0 EndX=51.9017 EndY=17.7495 EndZ=0
    g279: LineSegment StartX=51.9017 StartY=17.7495 StartZ=0 EndX=51.9017 EndY=17.8092 EndZ=0
    g280: LineSegment StartX=51.9017 StartY=17.8092 StartZ=0 EndX=51.8351 EndY=17.8092 EndZ=0
    g281: LineSegment StartX=51.8351 StartY=17.8092 StartZ=0 EndX=51.8351 EndY=17.8911 EndZ=0
    g282: LineSegment StartX=51.8351 StartY=17.8911 StartZ=0 EndX=51.7639 EndY=17.8911 EndZ=0
    g283: LineSegment StartX=51.7639 StartY=17.8911 StartZ=0 EndX=51.7639 EndY=17.9626 EndZ=0
    g284: LineSegment StartX=51.7639 StartY=17.9626 StartZ=0 EndX=51.6325 EndY=17.9626 EndZ=0
    g285: LineSegment StartX=51.6325 StartY=17.9626 StartZ=0 EndX=51.6325 EndY=18.0284 EndZ=0
    g286: LineSegment StartX=51.6325 StartY=18.0284 StartZ=0 EndX=51.485 EndY=18.0284 EndZ=0
    g287: LineSegment StartX=51.485 StartY=18.0284 StartZ=0 EndX=51.485 EndY=18.0711 EndZ=0
    g288: LineSegment StartX=51.485 StartY=18.0711 StartZ=0 EndX=51.4163 EndY=18.0711 EndZ=0
    g289: LineSegment StartX=51.4163 StartY=18.0711 StartZ=0 EndX=51.4163 EndY=18.1587 EndZ=0
    g290: LineSegment StartX=51.4163 StartY=18.1587 StartZ=0 EndX=51.2878 EndY=18.1587 EndZ=0
    g291: LineSegment StartX=51.2878 StartY=18.1587 StartZ=0 EndX=51.2878 EndY=18.2275 EndZ=0
    g292: LineSegment StartX=51.2878 StartY=18.2275 StartZ=0 EndX=51.2232 EndY=18.2275 EndZ=0
    g293: LineSegment StartX=51.2232 StartY=18.2275 StartZ=0 EndX=51.2267 EndY=18.2921 EndZ=0
    g294: LineSegment StartX=51.2267 StartY=18.2921 StartZ=0 EndX=51.1526 EndY=18.2921 EndZ=0
    g295: LineSegment StartX=51.1526 StartY=18.2921 StartZ=0 EndX=51.1526 EndY=18.3662 EndZ=0
    g296: LineSegment StartX=51.1526 StartY=18.3662 StartZ=0 EndX=51.0845 EndY=18.3602 EndZ=0
    g297: LineSegment StartX=51.0845 StartY=18.3602 StartZ=0 EndX=51.0845 EndY=18.4424 EndZ=0
    g298: LineSegment StartX=51.0845 StartY=18.4424 StartZ=0 EndX=51.0222 EndY=18.4424 EndZ=0
    g299: LineSegment StartX=51.0222 StartY=18.4424 StartZ=0 EndX=51.0222 EndY=18.5138 EndZ=0
    g300: LineSegment StartX=51.0222 StartY=18.5138 StartZ=0 EndX=50.8169 EndY=18.5138 EndZ=0
    g301: LineSegment StartX=50.8169 StartY=18.5138 StartZ=0 EndX=50.7878 EndY=18.6026 EndZ=0
    g302: LineSegment StartX=50.7878 StartY=18.6026 StartZ=0 EndX=50.7494 EndY=18.6113 EndZ=0
    g303: LineSegment StartX=50.7494 StartY=18.6113 StartZ=0 EndX=50.7397 EndY=18.6731 EndZ=0
    g304: LineSegment StartX=50.7397 StartY=18.6731 StartZ=0 EndX=50.5414 EndY=18.6536 EndZ=0
    g305: LineSegment StartX=50.5414 StartY=18.6536 StartZ=0 EndX=50.5381 EndY=18.7381 EndZ=0
    g306: LineSegment StartX=50.5381 StartY=18.7381 StartZ=0 EndX=50.4114 EndY=18.7218 EndZ=0
    g307: LineSegment StartX=50.4114 StartY=18.7218 StartZ=0 EndX=50.3951 EndY=18.7934 EndZ=0
    g308: LineSegment StartX=50.3951 StartY=18.7934 StartZ=0 EndX=50.3334 EndY=18.7934 EndZ=0
    g309: LineSegment StartX=50.3334 StartY=18.7934 StartZ=0 EndX=50.3366 EndY=18.8389 EndZ=0
    g310: LineSegment StartX=50.3366 StartY=18.8389 StartZ=0 EndX=50.2066 EndY=18.8389 EndZ=0
    g311: LineSegment StartX=50.2066 StartY=18.8389 StartZ=0 EndX=50.2099 EndY=18.9201 EndZ=0
    g312: LineSegment StartX=50.2099 StartY=18.9201 StartZ=0 EndX=50.1254 EndY=18.9266 EndZ=0
    g313: LineSegment StartX=50.1254 StartY=18.9266 StartZ=0 EndX=50.1156 EndY=19.0046 EndZ=0
    g314: LineSegment StartX=50.1156 StartY=19.0046 StartZ=0 EndX=49.9986 EndY=18.9949 EndZ=0
    g315: LineSegment StartX=49.9986 StartY=18.9949 StartZ=0 EndX=49.9921 EndY=19.0859 EndZ=0
    g316: LineSegment StartX=49.9921 StartY=19.0859 StartZ=0 EndX=49.9368 EndY=19.0501 EndZ=0
    g317: LineSegment StartX=49.9368 StartY=19.0501 StartZ=0 EndX=49.9206 EndY=19.1509 EndZ=0
    g318: LineSegment StartX=49.9206 StartY=19.1509 StartZ=0 EndX=49.7971 EndY=19.1281 EndZ=0
    g319: LineSegment StartX=49.7971 StartY=19.1281 StartZ=0 EndX=49.8068 EndY=19.2029 EndZ=0
    g320: LineSegment StartX=49.8068 StartY=19.2029 StartZ=0 EndX=49.7288 EndY=19.1899 EndZ=0
    g321: LineSegment StartX=49.7288 StartY=19.1899 StartZ=0 EndX=49.7191 EndY=19.2582 EndZ=0
    g322: LineSegment StartX=49.7191 StartY=19.2582 StartZ=0 EndX=49.6606 EndY=19.2647 EndZ=0
    g323: LineSegment StartX=49.6606 StartY=19.2647 StartZ=0 EndX=49.6541 EndY=19.3329 EndZ=0
    g324: LineSegment StartX=49.6541 StartY=19.3329 StartZ=0 EndX=49.6021 EndY=19.3329 EndZ=0
    g325: LineSegment StartX=49.6021 StartY=19.3329 StartZ=0 EndX=49.5988 EndY=19.4077 EndZ=0
    g326: LineSegment StartX=49.5988 StartY=19.4077 StartZ=0 EndX=49.4623 EndY=19.3947 EndZ=0
    g327: LineSegment StartX=49.4623 StartY=19.3947 StartZ=0 EndX=49.4623 EndY=19.4727 EndZ=0
    g328: LineSegment StartX=49.4623 StartY=19.4727 StartZ=0 EndX=49.2543 EndY=19.4532 EndZ=0
    g329: LineSegment StartX=49.2543 StartY=19.4532 StartZ=0 EndX=49.2543 EndY=19.5279 EndZ=0
    g330: LineSegment StartX=49.2543 StartY=19.5279 StartZ=0 EndX=49.199 EndY=19.5279 EndZ=0
    g331: LineSegment StartX=49.199 StartY=19.5279 StartZ=0 EndX=49.199 EndY=19.6189 EndZ=0
    g332: LineSegment StartX=49.199 StartY=19.6189 StartZ=0 EndX=49.0658 EndY=19.6059 EndZ=0
    g333: LineSegment StartX=49.0658 StartY=19.6059 StartZ=0 EndX=49.0495 EndY=19.6612 EndZ=0
    g334: LineSegment StartX=49.0495 StartY=19.6612 StartZ=0 EndX=48.991 EndY=19.6547 EndZ=0
    g335: LineSegment StartX=48.991 StartY=19.6547 StartZ=0 EndX=48.9845 EndY=19.7359 EndZ=0
    g336: LineSegment StartX=48.9845 StartY=19.7359 StartZ=0 EndX=48.8577 EndY=19.7262 EndZ=0
    g337: LineSegment StartX=48.8577 StartY=19.7262 StartZ=0 EndX=48.8577 EndY=19.8149 EndZ=0
    g338: LineSegment StartX=48.8577 StartY=19.8149 StartZ=0 EndX=48.7743 EndY=19.8069 EndZ=0
    g339: LineSegment StartX=48.7743 StartY=19.8069 StartZ=0 EndX=48.7743 EndY=19.8894 EndZ=0
    g340: LineSegment StartX=48.7743 StartY=19.8894 StartZ=0 EndX=48.5854 EndY=19.8894 EndZ=0
    g341: LineSegment StartX=48.5854 StartY=19.8894 StartZ=0 EndX=48.5854 EndY=19.9533 EndZ=0
    g342: LineSegment StartX=48.5854 StartY=19.9533 StartZ=0 EndX=48.4417 EndY=19.9533 EndZ=0
    g343: LineSegment StartX=48.4417 StartY=19.9533 StartZ=0 EndX=48.4417 EndY=20.0118 EndZ=0
    g344: LineSegment StartX=48.4417 StartY=20.0118 StartZ=0 EndX=48.3751 EndY=20.0118 EndZ=0
    g345: LineSegment StartX=48.3751 StartY=20.0118 StartZ=0 EndX=48.3751 EndY=20.089 EndZ=0
    g346: LineSegment StartX=48.3751 StartY=20.089 StartZ=0 EndX=48.3033 EndY=20.089 EndZ=0
    g347: LineSegment StartX=48.3033 StartY=20.089 StartZ=0 EndX=48.3033 EndY=20.1524 EndZ=0
    g348: LineSegment StartX=48.3033 StartY=20.1524 StartZ=0 EndX=48.0916 EndY=20.1524 EndZ=0
    g349: LineSegment StartX=48.0916 StartY=20.1524 StartZ=0 EndX=48.0916 EndY=20.2331 EndZ=0
    g350: LineSegment StartX=48.0916 StartY=20.2331 StartZ=0 EndX=47.8912 EndY=20.2331 EndZ=0
    g351: LineSegment StartX=47.8912 StartY=20.2331 StartZ=0 EndX=47.8912 EndY=20.2962 EndZ=0
    g352: LineSegment StartX=47.8912 StartY=20.2962 StartZ=0 EndX=47.6864 EndY=20.2962 EndZ=0
    g353: LineSegment StartX=47.6864 StartY=20.2962 StartZ=0 EndX=47.6864 EndY=20.3681 EndZ=0
    g354: LineSegment StartX=47.6864 StartY=20.3681 StartZ=0 EndX=47.2898 EndY=20.3681 EndZ=0
    g355: LineSegment StartX=47.2898 StartY=20.3681 StartZ=0 EndX=47.2898 EndY=20.4313 EndZ=0
    g356: LineSegment StartX=47.2898 StartY=20.4313 StartZ=0 EndX=47.0094 EndY=20.4313 EndZ=0
    g357: LineSegment StartX=47.0094 StartY=20.4313 StartZ=0 EndX=47.0094 EndY=20.5033 EndZ=0
    g358: LineSegment StartX=47.0094 StartY=20.5033 StartZ=0 EndX=46.7265 EndY=20.5033 EndZ=0
    g359: LineSegment StartX=46.7265 StartY=20.5033 StartZ=0 EndX=46.7265 EndY=20.5623 EndZ=0
    g360: LineSegment StartX=46.7265 StartY=20.5623 StartZ=0 EndX=46.3195 EndY=20.5623 EndZ=0
    g361: LineSegment StartX=46.3195 StartY=20.5623 StartZ=0 EndX=46.2304 EndY=20.478 EndZ=0
    g362: LineSegment StartX=46.2304 StartY=20.478 StartZ=0 EndX=45.8403 EndY=20.478 EndZ=0
    g363: LineSegment StartX=45.8403 StartY=20.478 StartZ=0 EndX=45.7581 EndY=20.3987 EndZ=0
    g364: LineSegment StartX=45.7581 StartY=20.3987 StartZ=0 EndX=45.6847 EndY=20.3987 EndZ=0
    g365: LineSegment StartX=45.6847 StartY=20.3987 StartZ=0 EndX=45.6847 EndY=20.4757 EndZ=0
    g366: LineSegment StartX=45.6847 StartY=20.4757 StartZ=0 EndX=45.2353 EndY=20.4757 EndZ=0
    g367: LineSegment StartX=45.2353 StartY=20.4757 StartZ=0 EndX=45.1511 EndY=20.3964 EndZ=0
    g368: LineSegment StartX=45.1511 StartY=20.3964 StartZ=0 EndX=45.039 EndY=20.3905 EndZ=0
    g369: LineSegment StartX=45.1271 StartY=20.498 StartZ=0 EndX=45.039 EndY=20.3905 EndZ=0
    g370: LineSegment StartX=45.1271 StartY=20.498 StartZ=0 EndX=45.1672 EndY=20.498 EndZ=0
    g371: LineSegment StartX=45.1672 StartY=20.498 StartZ=0 EndX=45.2586 EndY=20.5605 EndZ=0
    g372: LineSegment StartX=45.2586 StartY=20.5605 StartZ=0 EndX=45.3242 EndY=20.5605 EndZ=0
    g373: LineSegment StartX=45.3242 StartY=20.5605 StartZ=0 EndX=45.4009 EndY=20.6461 EndZ=0
    g374: LineSegment StartX=45.4009 StartY=20.6461 StartZ=0 EndX=45.5221 EndY=20.6461 EndZ=0
    g375: LineSegment StartX=45.5221 StartY=20.6461 StartZ=0 EndX=45.6149 EndY=20.705 EndZ=0
    g376: LineSegment StartX=45.6149 StartY=20.705 StartZ=0 EndX=45.8042 EndY=20.705 EndZ=0
    g377: LineSegment StartX=45.8042 StartY=20.705 StartZ=0 EndX=45.9915 EndY=20.8898 EndZ=0
    g378: LineSegment StartX=45.9915 StartY=20.8898 StartZ=0 EndX=45.9915 EndY=20.959 EndZ=0
    g379: LineSegment StartX=45.9915 StartY=20.959 StartZ=0 EndX=46.0581 EndY=21.0202 EndZ=0
    g380: LineSegment StartX=46.0581 StartY=21.0202 StartZ=0 EndX=46.0527 EndY=21.0894 EndZ=0
    g381: LineSegment StartX=46.0527 StartY=21.0894 StartZ=0 EndX=46.2124 EndY=21.2464 EndZ=0
    g382: LineSegment StartX=46.2124 StartY=21.2464 StartZ=0 EndX=46.2763 EndY=21.2277 EndZ=0
    g383: LineSegment StartX=46.2763 StartY=21.2277 StartZ=0 EndX=46.5051 EndY=21.4486 EndZ=0
    g384: LineSegment StartX=46.5051 StartY=21.4486 StartZ=0 EndX=46.585 EndY=21.4539 EndZ=0
    g385: LineSegment StartX=46.585 StartY=21.4539 StartZ=0 EndX=46.6994 EndY=21.603 EndZ=0
    g386: LineSegment StartX=46.6994 StartY=21.603 StartZ=0 EndX=46.8245 EndY=21.5843 EndZ=0
    g387: LineSegment StartX=46.8245 StartY=21.5843 StartZ=0 EndX=46.9016 EndY=21.6855 EndZ=0
    g388: LineSegment StartX=46.9016 StartY=21.6855 StartZ=0 EndX=46.9655 EndY=21.6562 EndZ=0
    g389: LineSegment StartX=46.9655 StartY=21.6562 StartZ=0 EndX=47.205 EndY=21.8754 EndZ=0
    g390: LineSegment StartX=47.205 StartY=21.8754 StartZ=0 EndX=47.205 EndY=22.0711 EndZ=0
    g391: LineSegment StartX=47.205 StartY=22.0711 StartZ=0 EndX=47.2634 EndY=22.0711 EndZ=0
    g392: LineSegment StartX=47.2634 StartY=22.0711 StartZ=0 EndX=47.6208 EndY=22.4458 EndZ=0
    g393: LineSegment StartX=47.6208 StartY=22.4458 StartZ=0 EndX=47.6208 EndY=22.5177 EndZ=0
    g394: LineSegment StartX=47.6208 StartY=22.5177 StartZ=0 EndX=47.8212 EndY=22.7182 EndZ=0
    g395: LineSegment StartX=47.8212 StartY=22.7182 StartZ=0 EndX=47.8343 EndY=22.7944 EndZ=0
    g396: LineSegment StartX=47.8343 StartY=22.7944 StartZ=0 EndX=48.0478 EndY=22.997 EndZ=0
    g397: LineSegment StartX=48.0478 StartY=22.997 StartZ=0 EndX=48.0478 EndY=23.1365 EndZ=0
    g398: LineSegment StartX=48.0478 StartY=23.1365 StartZ=0 EndX=48.0998 EndY=23.2173 EndZ=0
    g399: LineSegment StartX=48.0998 StartY=23.2173 StartZ=0 EndX=48.0998 EndY=23.2802 EndZ=0
    ... +484 more geometry lines
  constraints (1492):
    c: Coincident(g3,g2)
    c: Vertical(g4)
    c: Vertical(g6)
    c: Coincident(g8,g7)
    c: Vertical(g8)
    c: Coincident(g8,g9)
    c: Coincident(g9,g10)
    c: Vertical(g10)
    c: Coincident(g10,g11)
    c: Coincident(g11,g12)
    c: Vertical(g12)
    c: Coincident(g13,g12)
    c: Horizontal(g13)
    c: Vertical(g14)
    c: Coincident(g16,g15)
    c: Vertical(g16)
    c: Horizontal(g17)
    c: Coincident(g18,g17)
    c: Vertical(g18)
    c: Horizontal(g19)
    c: Coincident(g20,g19)
    c: Vertical(g20)
    c: Horizontal(g21)
    c: Vertical(g22)
    c: Horizontal(g23)
    c: Coincident(g24,g23)
    c: Vertical(g24)
    c: Horizontal(g25)
    c: Coincident(g27,g26)
    c: Horizontal(g27)
    c: Vertical(g28)
    c: Coincident(g30,g29)
    c: Vertical(g30)
    c: Coincident(g31,g32)
    c: Vertical(g32)
    c: Coincident(g32,g33)
    c: Horizontal(g33)
    c: Coincident(g34,g33)
    c: Vertical(g34)
    c: Coincident(g35,g34)
    c: Horizontal(g35)
    c: Coincident(g36,g35)
    c: Vertical(g36)
    c: Coincident(g37,g36)
    c: Horizontal(g37)
    c: Vertical(g38)
    c: Horizontal(g39)
    c: Vertical(g40)
    c: Horizontal(g41)
    c: Coincident(g42,g41)
    c: Vertical(g42)
    c: Horizontal(g43)
    c: Coincident(g44,g43)
    c: Vertical(g44)
    c: Coincident(g45,g44)
    c: Horizontal(g45)
    c: Coincident(g46,g45)
    c: Vertical(g46)
    c: Coincident(g47,g46)
    c: Horizontal(g47)
    c: Coincident(g48,g47)
    c: Vertical(g48)
    c: Horizontal(g49)
    c: Vertical(g50)
    c: Coincident(g51,g50)
    c: Horizontal(g51)
    c: Vertical(g52)
    c: Coincident(g53,g52)
    c: Horizontal(g53)
    c: Coincident(g54,g53)
    c: Vertical(g54)
    c: Coincident(g55,g54)
    c: Horizontal(g55)
    c: Coincident(g56,g55)
    c: Vertical(g56)
    c: Coincident(g57,g56)
    c: Horizontal(g57)
    c: Coincident(g58,g57)
    c: Vertical(g58)
    c: Coincident(g60,g59)
    c: Vertical(g60)
    c: Coincident(g61,g60)
    c: Horizontal(g61)
    c: Vertical(g62)
    c: Horizontal(g63)
    c: Coincident(g64,g63)
    c: Vertical(g64)
    c: Horizontal(g65)
    c: Vertical(g66)
    c: Coincident(g68,g67)
    c: Vertical(g68)
    c: Horizontal(g69)
    c: Coincident(g70,g69)
    c: Vertical(g70)
    c: Horizontal(g71)
    c: Coincident(g72,g71)
    c: Vertical(g72)
    c: Horizontal(g73)
    c: Coincident(g74,g73)
    c: Vertical(g74)
    c: Horizontal(g75)
    c: Coincident(g76,g75)
    c: Vertical(g76)
    c: Horizontal(g77)
    c: Vertical(g78)
    c: Coincident(g79,g78)
    c: Coincident(g80,g79)
    c: Vertical(g80)
    c: Coincident(g81,g80)
    c: Coincident(g82,g81)
    c: Horizontal(g83)
    c: Coincident(g85,g84)
    c: Horizontal(g85)
    c: Coincident(g86,g85)
    c: Coincident(g89,g88)
    c: Horizontal(g89)
    c: Coincident(g90,g89)
    c: Coincident(g91,g90)
    c: Horizontal(g91)
    c: Coincident(g92,g91)
    c: Horizontal(g93)
    c: Coincident(g94,g93)
    c: Horizontal(g95)
    c: Coincident(g96,g95)
    c: Coincident(g97,g98)
    c: Coincident(g98,g99)
    c: Vertical(g99)
    c: Coincident(g99,g100)
    c: Coincident(g100,g101)
    c: Coincident(g101,g102)
    c: Coincident(g102,g103)
    c: Coincident(g103,g104)
    c: Coincident(g104,g105)
    c: Vertical(g105)
    c: Coincident(g105,g106)
    c: Coincident(g106,g107)
    c: Coincident(g107,g108)
    c: Horizontal(g108)
    c: Coincident(g108,g109)
    c: Coincident(g109,g110)
    c: Vertical(g110)
    c: Coincident(g110,g111)
    c: Coincident(g111,g112)
    c: Coincident(g112,g113)
    c: Coincident(g113,g114)
    c: Coincident(g114,g115)
    c: Coincident(g115,g116)
    c: Vertical(g116)
    c: Coincident(g116,g117)
    c: Coincident(g117,g118)
    c: Coincident(g118,g119)
    c: Coincident(g119,g120)
    c: Coincident(g120,g121)
    c: Horizontal(g121)
    c: Coincident(g121,g122)
    c: Coincident(g122,g123)
    c: Coincident(g123,g124)
    c: Coincident(g124,g125)
    c: Vertical(g125)
    c: Coincident(g125,g126)
    c: Coincident(g126,g127)
    c: Horizontal(g127)
    c: Coincident(g127,g128)
    c: Vertical(g128)
    c: Coincident(g128,g129)
    c: Coincident(g129,g130)
    c: Vertical(g130)
    c: Coincident(g130,g131)
    c: Horizontal(g131)
    c: Coincident(g131,g132)
    c: Vertical(g132)
    c: Coincident(g132,g133)
    c: Coincident(g133,g134)
    c: Coincident(g134,g135)
    c: Coincident(g135,g136)
    c: Coincident(g136,g137)
    c: Coincident(g137,g138)
    c: Vertical(g138)
    c: Coincident(g138,g139)
    c: Coincident(g139,g140)
    c: Vertical(g140)
    c: Coincident(g140,g141)
    c: Horizontal(g141)
    c: Coincident(g141,g142)
    c: Coincident(g142,g143)
    c: Coincident(g143,g144)
    c: Coincident(g144,g145)
    c: Coincident(g145,g146)
    c: Vertical(g146)
    c: Coincident(g146,g147)
    c: Coincident(g147,g148)
    c: Vertical(g148)
    c: Coincident(g148,g149)
    c: Horizontal(g149)
    c: Coincident(g149,g150)
    c: Vertical(g150)
    c: Coincident(g150,g151)
    c: Horizontal(g151)
    c: Coincident(g151,g152)
    c: Vertical(g152)
    c: Coincident(g152,g153)
    c: Horizontal(g153)
    c: Coincident(g153,g154)
    c: Vertical(g154)
    c: Coincident(g154,g155)
    c: Horizontal(g155)
    c: Coincident(g155,g156)
    c: Vertical(g156)
    c: Coincident(g156,g157)
    c: Horizontal(g157)
    c: Coincident(g157,g158)
    c: Vertical(g158)
    c: Coincident(g158,g159)
    c: Coincident(g159,g160)
    c: Coincident(g160,g161)
    c: Horizontal(g161)
    c: Coincident(g161,g162)
    c: Vertical(g162)
    c: Coincident(g162,g163)
    c: Horizontal(g163)
    c: Coincident(g163,g164)
    c: Coincident(g164,g165)
    c: Horizontal(g165)
    c: Coincident(g165,g166)
    c: Vertical(g166)
    c: Coincident(g166,g167)
    c: Horizontal(g167)
    c: Coincident(g167,g168)
    c: Coincident(g168,g169)
    c: Coincident(g169,g170)
    c: Vertical(g170)
    c: Coincident(g170,g171)
    c: Coincident(g171,g172)
    c: Vertical(g172)
    c: Coincident(g172,g173)
    c: Horizontal(g173)
    c: Coincident(g173,g174)
    c: Vertical(g174)
    c: Coincident(g174,g175)
    c: Horizontal(g175)
    c: Coincident(g175,g176)
    c: Vertical(g176)
    c: Coincident(g176,g177)
    c: Coincident(g177,g178)
    c: Vertical(g178)
    c: Coincident(g178,g179)
    c: Horizontal(g179)
    c: Coincident(g179,g180)
    c: Vertical(g180)
    c: Coincident(g180,g181)
    c: Horizontal(g181)
    c: Coincident(g181,g182)
    c: Vertical(g182)
    c: Coincident(g182,g183)
    c: Horizontal(g183)
    c: Coincident(g183,g184)
    c: Vertical(g184)
    c: Coincident(g184,g185)
    c: Horizontal(g185)
    c: Coincident(g185,g186)
    c: Coincident(g186,g187)
    c: Coincident(g187,g188)
    c: Coincident(g188,g189)
    c: Vertical(g189)
    c: Coincident(g189,g190)
    c: Coincident(g190,g191)
    c: Coincident(g191,g192)
    c: Coincident(g192,g193)
    c: Coincident(g193,g194)
    c: Coincident(g194,g195)
    c: Vertical(g195)
    c: Coincident(g195,g196)
    c: Coincident(g196,g197)
    c: Vertical(g197)
    c: Coincident(g197,g198)
    c: Coincident(g198,g199)
    c: Vertical(g199)
    c: Coincident(g199,g200)
    c: Coincident(g200,g201)
    c: Vertical(g201)
    c: Coincident(g201,g202)
    c: Coincident(g202,g203)
    c: Vertical(g203)
    c: Coincident(g203,g204)
    c: Coincident(g204,g205)
    c: Vertical(g205)
    c: Coincident(g205,g206)
    c: Coincident(g206,g207)
    c: Coincident(g207,g208)
    c: Coincident(g208,g209)
    c: Vertical(g209)
    c: Coincident(g209,g210)
    c: Coincident(g210,g211)
    c: Coincident(g211,g212)
    c: Coincident(g212,g213)
    c: Coincident(g213,g214)
    c: Coincident(g214,g215)
    c: Vertical(g215)
    c: Coincident(g215,g216)
    c: Coincident(g216,g217)
    c: Horizontal(g217)
    c: Coincident(g217,g218)
    c: Vertical(g218)
    c: Coincident(g218,g219)
    c: Horizontal(g219)
    c: Coincident(g219,g220)
    c: Coincident(g220,g221)
    c: Horizontal(g221)
    c: Coincident(g221,g222)
    c: Coincident(g222,g223)
    c: Horizontal(g223)
    c: Coincident(g223,g224)
    c: Coincident(g224,g225)
    c: Horizontal(g225)
    c: Coincident(g225,g226)
    c: Vertical(g226)
    c: Coincident(g226,g227)
    c: Horizontal(g227)
    c: Coincident(g227,g228)
    c: Vertical(g228)
    c: Coincident(g228,g229)
    c: Horizontal(g229)
    c: Coincident(g229,g230)
    c: Coincident(g230,g231)
    c: Coincident(g231,g232)
    c: Coincident(g232,g233)
    c: Horizontal(g233)
    c: Coincident(g233,g234)
    c: Coincident(g234,g235)
    c: Horizontal(g235)
    c: Coincident(g235,g236)
    c: Coincident(g236,g237)
    c: Horizontal(g237)
    c: Coincident(g237,g238)
    c: Coincident(g238,g239)
    c: Horizontal(g239)
    c: Coincident(g239,g240)
    c: Coincident(g240,g241)
    c: Vertical(g241)
    c: Coincident(g241,g242)
    c: Horizontal(g242)
    c: Coincident(g242,g243)
    c: Vertical(g243)
    c: Coincident(g243,g244)
    c: Coincident(g244,g245)
    c: Vertical(g245)
    c: Coincident(g245,g246)
    c: Horizontal(g246)
    c: Coincident(g246,g247)
    c: Coincident(g247,g248)
    c: Horizontal(g248)
    c: Coincident(g248,g249)
    c: Vertical(g249)
    c: Coincident(g249,g250)
    c: Coincident(g250,g251)
    c: Coincident(g251,g252)
    c: Horizontal(g252)
    c: Coincident(g252,g253)
    c: Coincident(g253,g254)
    c: Horizontal(g254)
    c: Coincident(g254,g255)
    c: Vertical(g255)
    c: Coincident(g255,g256)
    c: Coincident(g256,g257)
    c: Coincident(g257,g258)
    c: Coincident(g258,g259)
    c: Coincident(g259,g260)
    c: Coincident(g260,g261)
    c: Vertical(g257)
    c: Horizontal(g258)
    c: Horizontal(g256)
    c: Vertical(g259)
    c: Horizontal(g260)
    c: Vertical(g261)
    c: Coincident(g261,g262)
    c: Horizontal(g262)
    c: Coincident(g262,g263)
    c: Vertical(g263)
    c: Coincident(g263,g264)
    c: Coincident(g264,g265)
    c: Coincident(g265,g266)
    c: Coincident(g266,g267)
    c: Coincident(g267,g268)
    c: Coincident(g268,g269)
    c: Vertical(g269)
    c: Coincident(g269,g270)
    c: Horizontal(g270)
    c: Coincident(g270,g271)
    c: Vertical(g271)
    c: Coincident(g271,g272)
    c: Coincident(g272,g273)
    c: Vertical(g273)
    c: Coincident(g273,g274)
    c: Horizontal(g274)
    c: Coincident(g274,g275)
    c: Vertical(g275)
    c: Coincident(g275,g276)
    c: Horizontal(g276)
    c: Coincident(g276,g277)
    c: Coincident(g277,g278)
    c: Horizontal(g278)
    c: Coincident(g278,g279)
    c: Coincident(g279,g280)
    c: Coincident(g280,g281)
    c: Vertical(g281)
    c: Coincident(g281,g282)
    c: Coincident(g282,g283)
    c: Coincident(g283,g284)
    c: Horizontal(g284)
    c: Coincident(g284,g285)
    c: Coincident(g285,g286)
    c: Coincident(g286,g287)
    c: Coincident(g287,g288)
    c: Coincident(g288,g289)
    c: Coincident(g289,g290)
    c: Coincident(g290,g291)
    c: Vertical(g291)
    c: Coincident(g291,g292)
    c: Horizontal(g292)
    c: Coincident(g292,g293)
    c: Coincident(g293,g294)
    c: Horizontal(g294)
    c: Coincident(g294,g295)
    c: Vertical(g295)
    c: Coincident(g295,g296)
    c: Coincident(g296,g297)
    c: Vertical(g297)
    c: Coincident(g297,g298)
    c: Horizontal(g298)
    c: Coincident(g298,g299)
    c: Vertical(g299)
    c: Coincident(g299,g300)
    c: Horizontal(g300)
    c: Coincident(g300,g301)
    c: Coincident(g301,g302)
    c: Coincident(g302,g303)
    c: Coincident(g303,g304)
    c: Coincident(g304,g305)
    c: Coincident(g305,g306)
    c: Coincident(g306,g307)
    c: Coincident(g307,g308)
    c: Horizontal(g308)
    c: Coincident(g308,g309)
    c: Coincident(g309,g310)
    c: Horizontal(g310)
    c: Coincident(g310,g311)
    c: Coincident(g311,g312)
    c: Coincident(g312,g313)
    c: Coincident(g313,g314)
    c: Coincident(g314,g315)
    c: Coincident(g315,g316)
    c: Coincident(g316,g317)
    c: Coincident(g317,g318)
    c: Coincident(g318,g319)
    c: Coincident(g319,g320)
    c: Coincident(g320,g321)
    c: Coincident(g321,g322)
    c: Coincident(g322,g323)
    c: Coincident(g323,g324)
    c: Horizontal(g324)
    c: Coincident(g324,g325)
    c: Coincident(g325,g326)
    c: Coincident(g326,g327)
    c: Vertical(g327)
    c: Coincident(g327,g328)
    c: Coincident(g328,g329)
    c: Coincident(g329,g330)
    c: Coincident(g330,g331)
    c: Vertical(g331)
    c: Coincident(g331,g332)
    c: Coincident(g332,g333)
    c: Coincident(g333,g334)
    c: Coincident(g334,g335)
    c: Coincident(g335,g336)
    c: Coincident(g336,g337)
    c: Vertical(g337)
    c: Coincident(g337,g338)
    c: Coincident(g338,g339)
    c: Coincident(g339,g340)
    c: Coincident(g340,g341)
    c: Coincident(g341,g342)
    c: Coincident(g342,g343)
    c: Coincident(g343,g344)
    c: Coincident(g344,g345)
    c: Coincident(g345,g346)
    c: Coincident(g346,g347)
    c: Coincident(g347,g348)
    c: Coincident(g348,g349)
    c: Coincident(g349,g350)
    c: Coincident(g350,g351)
    c: Coincident(g351,g352)
    c: Coincident(g352,g353)
    c: Coincident(g353,g354)
    c: Coincident(g354,g355)
    c: Coincident(g355,g356)
    c: Coincident(g356,g357)
    c: Vertical(g357)
    c: Coincident(g357,g358)
    c: Horizontal(g358)
    c: Coincident(g358,g359)
    c: Coincident(g359,g360)
    c: Coincident(g360,g361)
    c: Coincident(g361,g362)
    c: Horizontal(g362)
    c: Coincident(g362,g363)
    c: Coincident(g363,g364)
    c: Coincident(g364,g365)
    c: Coincident(g365,g366)
    c: Coincident(g366,g367)
    c: Horizontal(g290)
    c: Vertical(g287)
    c: Vertical(g285)
    c: Vertical(g283)
    c: Vertical(g279)
    c: Vertical(g277)
    c: Horizontal(g286)
    c: Horizontal(g288)
    c: Vertical(g289)
    c: Horizontal(g280)
    c: Horizontal(g282)
    c: Vertical(g329)
    c: Horizontal(g330)
    c: Horizontal(g340)
    c: Horizontal(g342)
    c: Horizontal(g344)
    c: Horizontal(g346)
    c: Horizontal(g348)
    c: Horizontal(g350)
    c: Vertical(g339)
    c: Vertical(g341)
    c: Vertical(g343)
    c: Vertical(g345)
    c: Vertical(g347)
    c: Vertical(g349)
    c: Vertical(g351)
    c: Vertical(g353)
    c: Vertical(g355)
    c: Horizontal(g352)
    c: Horizontal(g354)
    c: Horizontal(g356)
    c: Vertical(g359)
    c: Horizontal(g360)
    c: Horizontal(g364)
    c: Vertical(g365)
    c: Horizontal(g366)
    c: Coincident(g368,g367)
    c: Coincident(g369,g368)
    c: Coincident(g369,g370)
    c: Coincident(g370,g371)
    c: Coincident(g371,g372)
    c: Horizontal(g372)
    c: Coincident(g372,g373)
    c: Coincident(g373,g374)
    c: Coincident(g374,g375)
    c: Coincident(g375,g376)
    c: Coincident(g376,g377)
    c: Coincident(g377,g378)
    c: Vertical(g378)
    c: Coincident(g378,g379)
    c: Coincident(g379,g380)
    c: Coincident(g380,g381)
    c: Coincident(g381,g382)
    c: Coincident(g382,g383)
    c: Coincident(g383,g384)
    c: Coincident(g384,g385)
    c: Coincident(g385,g386)
    c: Coincident(g386,g387)
    c: Coincident(g387,g388)
    c: Coincident(g388,g389)
    c: Coincident(g389,g390)
    c: Coincident(g390,g391)
    c: Horizontal(g391)
    c: Coincident(g391,g392)
    c: Coincident(g392,g393)
    c: Coincident(g393,g394)
    c: Coincident(g394,g395)
    c: Coincident(g395,g396)
    c: Coincident(g396,g397)
    c: Coincident(g397,g398)
    c: Coincident(g398,g399)
    c: Coincident(g399,g400)
    c: Coincident(g400,g401)
    c: Coincident(g401,g402)
    c: Coincident(g402,g403)
    c: Coincident(g403,g404)
    c: Coincident(g404,g405)
    c: Coincident(g405,g406)
    c: Coincident(g406,g407)
    c: Coincident(g407,g408)
    c: Coincident(g408,g409)
    c: Vertical(g409)
    c: Coincident(g409,g410)
    c: Coincident(g410,g411)
    c: Vertical(g411)
    c: Coincident(g411,g412)
    c: Horizontal(g412)
    c: Coincident(g412,g413)
    c: Coincident(g413,g414)
    c: Horizontal(g414)
    c: Coincident(g414,g415)
    c: Coincident(g415,g416)
    c: Coincident(g416,g417)
    c: Coincident(g417,g418)
    c: Coincident(g418,g419)
    c: Coincident(g419,g420)
    c: Coincident(g420,g421)
    c: Coincident(g421,g422)
    c: Coincident(g422,g423)
    c: Coincident(g423,g424)
    c: Coincident(g424,g425)
    c: Coincident(g425,g426)
    c: Horizontal(g426)
    c: Coincident(g426,g427)
    c: Coincident(g427,g428)
    c: Horizontal(g428)
    c: Coincident(g428,g429)
    c: Coincident(g429,g430)
    c: Coincident(g430,g431)
    c: Coincident(g431,g432)
    c: Horizontal(g432)
    c: Coincident(g432,g433)
    c: Coincident(g433,g434)
    c: Horizontal(g434)
    c: Coincident(g434,g435)
    c: Coincident(g435,g436)
    c: Coincident(g436,g437)
    c: Coincident(g437,g438)
    c: Coincident(g439,g440)
    c: Coincident(g440,g441)
    c: Coincident(g441,g442)
    c: Coincident(g442,g443)
    c: Coincident(g443,g444)
    c: Coincident(g444,g445)
    c: Coincident(g445,g446)
    c: Coincident(g446,g447)
    c: Coincident(g447,g448)
    c: Coincident(g448,g449)
    c: Coincident(g449,g450)
    c: Coincident(g450,g451)
    c: Coincident(g451,g452)
    c: Coincident(g452,g453)
    c: Coincident(g453,g454)
    c: Coincident(g454,g455)
    c: Coincident(g455,g456)
    c: Coincident(g456,g457)
    c: Coincident(g457,g458)
    c: Coincident(g458,g459)
    c: Coincident(g459,g460)
    c: Coincident(g460,g461)
    c: Coincident(g461,g462)
    c: Coincident(g462,g463)
    c: Coincident(g463,g464)
    c: Coincident(g464,g465)
    c: Coincident(g465,g466)
    c: Coincident(g466,g467)
    c: Coincident(g467,g468)
    c: Coincident(g468,g469)
    c: Coincident(g469,g470)
    c: Coincident(g470,g471)
    c: Coincident(g471,g472)
    c: Horizontal(g472)
    c: Coincident(g472,g473)
    c: Coincident(g473,g474)
    c: Coincident(g474,g475)
    c: Coincident(g475,g476)
    c: Coincident(g476,g477)
    c: Coincident(g477,g478)
    c: Coincident(g478,g479)
    c: Coincident(g479,g480)
    c: Coincident(g480,g481)
    c: Coincident(g481,g482)
    c: Coincident(g482,g483)
    c: Coincident(g483,g484)
    c: Coincident(g484,g485)
    c: Coincident(g485,g486)
    c: Coincident(g486,g487)
    c: Coincident(g487,g488)
    c: Vertical(g488)
    c: Coincident(g488,g489)
    c: Coincident(g489,g490)
    c: Vertical(g490)
    c: Coincident(g490,g491)
    c: Coincident(g491,g492)
    c: Coincident(g492,g493)
    c: Coincident(g493,g494)
    c: Coincident(g494,g495)
    c: Coincident(g495,g496)
    c: Coincident(g496,g497)
    c: Coincident(g497,g498)
    c: Coincident(g498,g499)
    c: Coincident(g499,g500)
    c: Coincident(g500,g501)
    c: Coincident(g501,g502)
    c: Coincident(g502,g503)
    c: Coincident(g503,g504)
    c: Horizontal(g370)
    c: Horizontal(g374)
    c: Horizontal(g376)
    c: Vertical(g390)
    c: Vertical(g397)
    c: Vertical(g399)
    c: Vertical(g401)
    c: Vertical(g403)
    c: Vertical(g407)
    c: Horizontal(g410)
    c: Vertical(g413)
    c: Vertical(g415)
    c: Horizontal(g416)
    c: Vertical(g417)
    c: Horizontal(g418)
    c: Vertical(g419)
    c: Vertical(g421)
    c: Vertical(g423)
    c: Vertical(g425)
    c: Vertical(g427)
    c: Vertical(g429)
    c: Horizontal(g420)
    c: Horizontal(g422)
    c: Horizontal(g424)
    c: Vertical(g431)
    c: Vertical(g433)
    c: Vertical(g435)
    c: Horizontal(g436)
    c: Horizontal(g438)
    c: Vertical(g437)
    c: Coincident(g439,g505)
    c: Horizontal(g505)
    c: Coincident(g505,g506)
    c: Coincident(g506,g438)
    c: Vertical(g506)
    c: Horizontal(g464)
    c: Horizontal(g462)
    c: Horizontal(g460)
    c: Horizontal(g458)
    c: Horizontal(g456)
    c: Horizontal(g454)
    c: Horizontal(g452)
    c: Horizontal(g450)
    c: Horizontal(g448)
    c: Horizontal(g446)
    c: Horizontal(g444)
    c: Horizontal(g442)
    c: Horizontal(g440)
    c: Horizontal(g468)
    c: Horizontal(g470)
    c: Horizontal(g474)
    c: Horizontal(g476)
    c: Horizontal(g478)
    c: Vertical(g465)
    c: Horizontal(g466)
    c: Vertical(g475)
    c: Vertical(g477)
    c: Horizontal(g491)
    c: Horizontal(g496)
    c: Horizontal(g494)
    c: Horizontal(g498)
    c: Vertical(g499)
    c: Vertical(g497)
    c: Vertical(g495)
    c: Vertical(g493)
    c: Horizontal(g500)
    c: Horizontal(g502)
    c: Horizontal(g504)
    c: Vertical(g501)
    c: Vertical(g503)
    c: Coincident(g504,g507)
    c: Vertical(g507)
    c: Coincident(g507,g508)
    c: Coincident(g508,g509)
    c: Coincident(g509,g510)
    c: Coincident(g510,g511)
    c: Vertical(g511)
    c: Coincident(g511,g512)
    c: Horizontal(g512)
    c: Coincident(g512,g513)
    c: Vertical(g513)
    c: Coincident(g513,g514)
    c: Coincident(g514,g515)
    c: Vertical(g515)
    c: Coincident(g515,g516)
    c: Horizontal(g516)
    c: Coincident(g516,g517)
    c: Coincident(g517,g518)
    c: Horizontal(g518)
    c: Coincident(g518,g519)
    c: Coincident(g519,g520)
    c: Coincident(g521,g522)
    c: Coincident(g522,g523)
    c: Coincident(g523,g524)
    c: Coincident(g524,g525)
    c: Coincident(g525,g526)
    c: Coincident(g526,g527)
    c: Coincident(g527,g528)
    c: Coincident(g528,g529)
    c: Coincident(g529,g530)
    c: Coincident(g531,g532)
    c: Coincident(g532,g533)
    c: Coincident(g533,g534)
    c: Coincident(g534,g535)
    c: Coincident(g535,g536)
    c: Coincident(g536,g537)
    c: Coincident(g537,g538)
    c: Coincident(g538,g539)
    c: Coincident(g539,g540)
    c: Coincident(g540,g541)
    c: Coincident(g541,g542)
    c: Coincident(g542,g543)
    c: Coincident(g543,g544)
    c: Coincident(g544,g545)
    c: Coincident(g545,g546)
    c: Coincident(g546,g547)
    c: Coincident(g547,g548)
    c: Coincident(g548,g549)
    c: Coincident(g549,g550)
    c: Horizontal(g550)
    c: Coincident(g550,g551)
    c: Coincident(g551,g552)
    c: Coincident(g552,g553)
    c: Coincident(g553,g554)
    c: Horizontal(g554)
    c: Coincident(g554,g555)
    c: Coincident(g555,g556)
    c: Coincident(g556,g557)
    c: Coincident(g557,g558)
    c: Horizontal(g558)
    c: Coincident(g558,g559)
    c: Coincident(g559,g560)
    c: Coincident(g560,g561)
    c: Coincident(g562,g563)
    c: Horizontal(g563)
    c: Coincident(g563,g564)
    c: Coincident(g564,g565)
    c: Coincident(g565,g566)
    c: Coincident(g566,g567)
    c: Horizontal(g567)
    c: Coincident(g567,g568)
    c: Coincident(g568,g569)
    c: Coincident(g569,g570)
    c: Coincident(g570,g571)
    c: Coincident(g571,g572)
    c: Coincident(g572,g573)
    c: Coincident(g573,g574)
    c: Coincident(g574,g575)
    c: Coincident(g575,g576)
    c: Coincident(g576,g577)
    c: Coincident(g577,g578)
    c: Coincident(g578,g579)
    c: Coincident(g579,g580)
    c: Vertical(g580)
    c: Coincident(g580,g581)
    c: Coincident(g581,g582)
    c: Coincident(g582,g583)
    c: Coincident(g583,g584)
    c: Coincident(g584,g585)
    c: Horizontal(g585)
    c: Coincident(g585,g586)
    c: Coincident(g586,g587)
    c: Coincident(g587,g588)
    c: Vertical(g588)
    c: Coincident(g588,g589)
    c: Coincident(g589,g590)
    c: Coincident(g590,g591)
    c: Coincident(g592,g593)
    c: Horizontal(g593)
    c: Coincident(g593,g594)
    c: Coincident(g594,g595)
    c: Coincident(g595,g596)
    c: Vertical(g596)
    c: Coincident(g596,g597)
    c: Horizontal(g597)
    c: Coincident(g597,g598)
    c: Vertical(g598)
    c: Coincident(g598,g599)
    c: Coincident(g599,g600)
    c: Coincident(g600,g601)
    c: Horizontal(g601)
    c: Coincident(g601,g602)
    c: Coincident(g602,g603)
    c: Coincident(g603,g604)
    c: Coincident(g604,g605)
    c: Coincident(g605,g606)
    c: Coincident(g606,g607)
    c: Coincident(g607,g608)
    c: Coincident(g608,g609)
    c: Horizontal(g609)
    c: Coincident(g609,g610)
    c: Coincident(g610,g611)
    c: Coincident(g611,g612)
    c: Coincident(g612,g613)
    c: Vertical(g613)
    c: Coincident(g613,g614)
    c: Coincident(g614,g615)
    c: Vertical(g615)
    c: Coincident(g615,g616)
    c: Coincident(g616,g617)
    c: Vertical(g617)
    c: Coincident(g618,g619)
    c: Vertical(g619)
    c: Coincident(g619,g620)
    c: Coincident(g620,g621)
    c: Coincident(g621,g622)
    c: Coincident(g622,g623)
    c: Coincident(g623,g624)
    c: Coincident(g624,g625)
    c: Coincident(g625,g626)
    c: Coincident(g626,g627)
    c: Vertical(g627)
    c: Coincident(g627,g628)
    c: Coincident(g628,g629)
    c: Coincident(g629,g630)
    c: Coincident(g630,g631)
    c: Coincident(g631,g632)
    c: Coincident(g632,g633)
    c: Vertical(g633)
    c: Coincident(g633,g634)
    c: Coincident(g634,g635)
    c: Vertical(g635)
    c: Coincident(g635,g636)
    c: Coincident(g636,g637)
    c: Coincident(g637,g638)
    c: Coincident(g638,g639)
    c: Coincident(g639,g640)
    c: Horizontal(g640)
    c: Coincident(g640,g641)
    c: Coincident(g641,g642)
    c: Vertical(g642)
    c: Coincident(g642,g643)
    c: Coincident(g643,g644)
    c: Vertical(g644)
    c: Coincident(g644,g645)
    c: Coincident(g645,g646)
    c: Coincident(g646,g647)
    c: Coincident(g647,g648)
    c: Coincident(g648,g649)
    c: Coincident(g649,g650)
    c: Coincident(g650,g651)
    c: Coincident(g651,g652)
    c: Vertical(g652)
    c: Coincident(g652,g653)
    c: Coincident(g653,g654)
    c: Coincident(g654,g655)
    c: Coincident(g655,g656)
    c: Coincident(g656,g657)
    c: Coincident(g657,g658)
    c: Vertical(g658)
    c: Coincident(g658,g659)
    c: Coincident(g659,g660)
    c: Vertical(g660)
    c: Coincident(g660,g661)
    c: Coincident(g661,g662)
    c: Coincident(g662,g663)
    c: Coincident(g663,g664)
    c: Coincident(g664,g665)
    c: Coincident(g665,g666)
    c: Coincident(g666,g667)
    c: Coincident(g667,g668)
    c: Coincident(g668,g669)
    c: Coincident(g669,g670)
    c: Coincident(g670,g671)
    c: Coincident(g671,g672)
    c: Coincident(g672,g673)
    c: Horizontal(g673)
    c: Coincident(g673,g674)
    c: Coincident(g674,g675)
    c: Coincident(g675,g676)
    c: Coincident(g676,g677)
    c: Coincident(g677,g678)
    c: Vertical(g678)
    c: Coincident(g678,g679)
    c: Coincident(g680,g681)
    c: Vertical(g681)
    c: Coincident(g681,g682)
    c: Horizontal(g682)
    c: Coincident(g682,g683)
    c: Coincident(g683,g684)
    c: Coincident(g684,g685)
    c: Coincident(g685,g686)
    c: Coincident(g686,g687)
    c: Vertical(g687)
    c: Coincident(g687,g688)
    c: Coincident(g688,g689)
    c: Coincident(g689,g690)
    c: Coincident(g690,g691)
    c: Coincident(g691,g692)
    c: Coincident(g692,g693)
    c: Coincident(g693,g694)
    c: Horizontal(g694)
    c: Coincident(g694,g695)
    c: Horizontal(g508)
    c: Vertical(g509)
    c: Horizontal(g510)
    c: Vertical(g519)
    c: Vertical(g517)
    c: Horizontal(g520)
    c: Coincident(g520,g696)
    c: Coincident(g696,g697)
    c: Horizontal(g697)
    c: Coincident(g697,g698)
    c: Coincident(g698,g521)
    c: Vertical(g698)
    c: Vertical(g522)
    c: Vertical(g524)
    c: Vertical(g526)
    c: Horizontal(g523)
    c: Horizontal(g525)
    c: Horizontal(g527)
    c: Horizontal(g529)
    c: Horizontal(g532)
    c: Horizontal(g521)
    c: Vertical(g528)
    c: Vertical(g530)
    c: Coincident(g530,g699)
    c: Coincident(g699,g700)
    c: Coincident(g700,g701)
    c: Coincident(g701,g531)
    c: Vertical(g700)
    c: Vertical(g531)
    c: Vertical(g533)
    c: Vertical(g535)
    c: Vertical(g537)
    c: Vertical(g539)
    c: Vertical(g541)
    c: Horizontal(g534)
    c: Horizontal(g536)
    c: Horizontal(g538)
    c: Horizontal(g540)
    c: Horizontal(g542)
    c: Horizontal(g544)
    c: Horizontal(g546)
    c: Horizontal(g699)
    c: Horizontal(g701)
    c: Vertical(g543)
    c: Vertical(g545)
    c: Vertical(g547)
    c: Vertical(g549)
    c: Horizontal(g548)
    c: Vertical(g555)
    c: Vertical(g553)
    c: Vertical(g551)
    c: Horizontal(g552)
    c: Horizontal(g556)
    c: Horizontal(g560)
    c: Vertical(g557)
    c: Vertical(g559)
    c: Vertical(g561)
    c: Coincident(g702,g562)
    c: Coincident(g702,g561)
    c: Horizontal(g565)
    c: Horizontal(g569)
    c: Horizontal(g571)
    c: Horizontal(g573)
    c: Horizontal(g575)
    c: Horizontal(g702)
    c: Vertical(g566)
    c: Vertical(g568)
    c: Vertical(g570)
    c: Vertical(g572)
    c: Vertical(g574)
    c: Vertical(g576)
    c: Vertical(g578)
    c: Vertical(g582)
    c: Vertical(g584)
    c: Horizontal(g577)
    c: Horizontal(g579)
    c: Horizontal(g581)
    c: Horizontal(g583)
    c: Horizontal(g587)
    c: Horizontal(g589)
    c: Horizontal(g591)
    c: Coincident(g591,g592)
    c: Vertical(g590)
    c: Vertical(g592)
    c: Vertical(g594)
    c: Vertical(g602)
    c: Vertical(g604)
    c: Horizontal(g595)
    c: Horizontal(g599)
    c: Horizontal(g605)
    c: Horizontal(g607)
    c: Vertical(g608)
    c: Vertical(g611)
    c: Horizontal(g612)
    c: Horizontal(g614)
    c: Horizontal(g620)
    c: Horizontal(g622)
    c: Vertical(g621)
    c: Vertical(g623)
    c: Coincident(g618,g703)
    c: Vertical(g703)
    c: Coincident(g703,g704)
    c: Horizontal(g704)
    c: Coincident(g704,g617)
    c: Horizontal(g624)
    c: Vertical(g625)
    c: Horizontal(g643)
    c: Horizontal(g645)
    c: Horizontal(g647)
    c: Horizontal(g649)
    c: Horizontal(g651)
    c: Horizontal(g653)
    c: Horizontal(g655)
    c: Horizontal(g657)
    c: Horizontal(g659)
    c: Vertical(g656)
    c: Vertical(g654)
    c: Vertical(g650)
    c: Vertical(g648)
    c: Vertical(g646)
    c: Vertical(g637)
    c: Vertical(g639)
    c: Horizontal(g661)
    c: Horizontal(g663)
    c: Horizontal(g665)
    c: Horizontal(g667)
    c: Horizontal(g669)
    c: Horizontal(g671)
    c: Horizontal(g675)
    c: Vertical(g662)
    c: Vertical(g664)
    c: Vertical(g666)
    c: Vertical(g668)
    c: Vertical(g670)
    c: Vertical(g672)
    c: Vertical(g674)
    c: Vertical(g676)
    c: Horizontal(g677)
    c: Horizontal(g679)
    c: Coincident(g679,g705)
    c: Vertical(g705)
    c: Coincident(g705,g706)
    c: Horizontal(g706)
    c: Coincident(g706,g707)
    c: Coincident(g680,g707)
    c: Horizontal(g680)
    c: Vertical(g707)
    c: Vertical(g691)
    c: Vertical(g693)
    c: Vertical(g689)
    c: Vertical(g685)
    c: Vertical(g683)
    c: Horizontal(g686)
    c: Horizontal(g688)
    c: Horizontal(g690)
    c: Horizontal(g692)
    c: Horizontal(g684)
    c: Vertical(g695)
    c: Coincident(g695,g708)
    c: Coincident(g708,g709)
    c: Coincident(g709,g710)
    c: Coincident(g710,g711)
    c: Coincident(g711,g712)
    c: Coincident(g712,g713)
    c: Horizontal(g713)
    c: Coincident(g713,g714)
    c: Coincident(g714,g715)
    c: Coincident(g715,g716)
    c: Coincident(g716,g717)
    c: Coincident(g718,g719)
    c: Horizontal(g720)
    c: Coincident(g721,g722)
    c: Coincident(g722,g723)
    c: Coincident(g723,g724)
    c: Horizontal(g724)
    c: Coincident(g724,g725)
    c: Horizontal(g726)
    c: Coincident(g726,g727)
    c: Coincident(g727,g728)
    c: Horizontal(g728)
    c: Coincident(g728,g729)
    c: Coincident(g729,g730)
    c: Coincident(g730,g731)
    c: Coincident(g731,g732)
    c: Coincident(g732,g733)
    c: Coincident(g733,g734)
    c: Coincident(g734,g735)
    c: Coincident(g735,g736)
    c: Coincident(g736,g737)
    c: Coincident(g737,g738)
    c: Coincident(g738,g739)
    c: Coincident(g739,g740)
    c: Coincident(g740,g741)
    c: Coincident(g741,g742)
    c: Coincident(g742,g743)
    c: Coincident(g743,g744)
    c: Coincident(g744,g745)
    c: Coincident(g745,g746)
    c: Coincident(g746,g747)
    c: Coincident(g747,g748)
    c: Coincident(g748,g749)
    c: Coincident(g749,g750)
    c: Coincident(g750,g751)
    c: Coincident(g751,g752)
    c: Coincident(g752,g753)
    c: Coincident(g753,g754)
    c: Coincident(g754,g755)
    c: Coincident(g755,g756)
    c: Coincident(g756,g757)
    c: Coincident(g757,g758)
    c: Coincident(g760,g761)
    c: Coincident(g761,g762)
    c: Coincident(g762,g763)
    c: Coincident(g763,g764)
    c: Coincident(g765,g766)
    c: Coincident(g766,g767)
    c: Coincident(g767,g768)
    c: Coincident(g769,g770)
    c: Coincident(g770,g771)
    c: Coincident(g772,g773)
    c: Coincident(g773,g774)
    c: Coincident(g774,g775)
    c: Coincident(g775,g776)
    c: Coincident(g776,g777)
    c: Coincident(g777,g778)
    c: Coincident(g778,g779)
    c: Coincident(g779,g780)
    c: Coincident(g780,g781)
    c: Coincident(g781,g782)
    c: Coincident(g782,g783)
    c: Coincident(g783,g784)
    c: Coincident(g784,g785)
    c: Coincident(g785,g786)
    c: Horizontal(g787)
    c: Coincident(g787,g788)
    c: Coincident(g788,g789)
    c: Coincident(g789,g790)
    c: Coincident(g790,g791)
    c: Horizontal(g791)
    c: Coincident(g791,g792)
    c: Coincident(g792,g793)
    c: Horizontal(g793)
    c: Coincident(g793,g794)
    c: Coincident(g794,g795)
    c: Coincident(g795,g796)
    c: Vertical(g796)
    c: Coincident(g796,g797)
    c: Horizontal(g797)
    c: Coincident(g797,g798)
    c: Coincident(g798,g799)
    c: Horizontal(g799)
    c: Coincident(g799,g800)
    c: Coincident(g800,g801)
    c: Coincident(g801,g802)
    c: Coincident(g802,g803)
    c: Horizontal(g803)
    c: Vertical(g804)
    c: Coincident(g804,g805)
    c: Coincident(g805,g806)
    c: Coincident(g806,g807)
    c: Coincident(g807,g808)
    c: Coincident(g808,g809)
    c: Coincident(g809,g810)
    c: Vertical(g810)
    c: Coincident(g810,g811)
    c: Coincident(g811,g812)
    c: Coincident(g812,g813)
    c: Coincident(g813,g814)
    c: Coincident(g814,g815)
    c: Horizontal(g815)
    c: Coincident(g815,g816)
    c: Coincident(g816,g817)
    c: Coincident(g817,g818)
    c: Coincident(g818,g819)
    c: Coincident(g819,g820)
    c: Coincident(g820,g821)
    c: Horizontal(g821)
    c: Coincident(g821,g822)
    c: Vertical(g822)
    c: Coincident(g822,g823)
    c: Coincident(g823,g824)
    c: Coincident(g824,g825)
    c: Horizontal(g825)
    c: Coincident(g825,g826)
    c: Coincident(g826,g827)
    c: Coincident(g827,g828)
    c: Coincident(g828,g829)
    c: Horizontal(g829)
    c: Coincident(g829,g830)
    c: Coincident(g830,g831)
    c: Coincident(g831,g832)
    c: Coincident(g832,g833)
    c: Horizontal(g834)
    c: Coincident(g834,g835)
    c: Coincident(g835,g836)
    c: Horizontal(g836)
    c: Coincident(g836,g837)
    c: Coincident(g837,g838)
    c: Horizontal(g838)
    c: Coincident(g838,g839)
    c: Coincident(g839,g840)
    c: Coincident(g840,g841)
    c: Coincident(g841,g842)
    c: Coincident(g842,g843)
    c: Coincident(g843,g844)
    c: Coincident(g844,g845)
    c: Coincident(g845,g846)
    c: Coincident(g846,g847)
    c: Coincident(g847,g848)
    c: Horizontal(g848)
    c: Coincident(g848,g849)
    c: Coincident(g849,g850)
    c: Coincident(g850,g851)
    c: Coincident(g851,g852)
    c: Coincident(g852,g853)
    c: Coincident(g853,g854)
    c: Coincident(g854,g855)
    c: Coincident(g855,g856)
    c: Coincident(g856,g857)
    c: Coincident(g857,g858)
    c: Horizontal(g858)
    c: Coincident(g858,g859)
    c: Coincident(g859,g860)
    c: Coincident(g860,g861)
    c: Coincident(g861,g862)
    c: Coincident(g862,g863)
    c: Coincident(g863,g864)
    c: Coincident(g786,g865)
    c: Coincident(g865,g866)
    c: Coincident(g866,g787)
    c: Vertical(g866)
    c: Horizontal(g709)
    c: Horizontal(g711)
    c: Horizontal(g715)
    c: Horizontal(g717)
    c: Horizontal(g719)
    c: Horizontal(g722)
    c: Coincident(g718,g867)
    c: Horizontal(g867)
    c: Coincident(g867,g868)
    c: Coincident(g868,g717)
    c: Coincident(g721,g869)
    c: Coincident(g869,g870)
    c: Coincident(g720,g870)
    c: Coincident(g871,g720)
    c: Coincident(g871,g719)
    c: Vertical(g871)
    c: Vertical(g870)
    c: Vertical(g723)
    c: Horizontal(g869)
    c: Coincident(g872,g726)
    c: Coincident(g873,g872)
    c: Coincident(g725,g873)
    c: Horizontal(g873)
    c: Horizontal(g736)
    c: Horizontal(g734)
    c: Horizontal(g732)
    c: Horizontal(g730)
    c: Horizontal(g738)
    c: Horizontal(g740)
    c: Horizontal(g742)
    c: Horizontal(g744)
    c: Horizontal(g746)
    c: Horizontal(g748)
    c: Horizontal(g750)
    c: Horizontal(g752)
    c: Horizontal(g754)
    c: Coincident(g758,g759)
    c: Horizontal(g756)
    c: Horizontal(g758)
    c: Coincident(g874,g759)
    c: Horizontal(g874)
    c: Coincident(g875,g760)
    c: Coincident(g875,g874)
    c: Horizontal(g760)
    c: Vertical(g762)
    c: Coincident(g765,g764)
    c: Vertical(g764)
    c: Vertical(g766)
    c: Vertical(g768)
    c: Coincident(g769,g768)
    c: Vertical(g770)
    c: Coincident(g876,g771)
    c: Coincident(g877,g772)
    c: Coincident(g877,g876)
    c: Vertical(g772)
    c: Vertical(g774)
    c: Vertical(g776)
    c: Vertical(g778)
    c: Vertical(g780)
    c: Vertical(g782)
    c: Vertical(g876)
    c: Horizontal(g773)
    c: Horizontal(g775)
    c: Horizontal(g777)
    c: Horizontal(g779)
    c: Horizontal(g781)
    c: Horizontal(g783)
    c: Horizontal(g785)
    c: Horizontal(g865)
    c: Vertical(g784)
    c: Vertical(g786)
    c: Vertical(g788)
    c: Vertical(g790)
    c: Horizontal(g789)
    c: Vertical(g792)
    c: Vertical(g794)
    c: Horizontal(g795)
    c: Vertical(g798)
    c: Vertical(g800)
    c: Vertical(g802)
    c: Horizontal(g801)
    c: Coincident(g804,g803)
    c: Horizontal(g805)
    c: Horizontal(g807)
    c: Horizontal(g809)
    c: Vertical(g806)
    c: Vertical(g808)
    c: Vertical(g812)
    c: Vertical(g816)
    c: Vertical(g814)
    c: Vertical(g818)
    c: Vertical(g820)
    c: Vertical(g824)
    c: Vertical(g826)
    c: Vertical(g828)
    c: Vertical(g830)
    c: Vertical(g832)
    c: Horizontal(g827)
    c: Horizontal(g823)
    c: Horizontal(g819)
    c: Horizontal(g817)
    c: Horizontal(g831)
    c: Horizontal(g833)
    c: Coincident(g878,g833)
    c: Coincident(g878,g834)
    c: Vertical(g837)
    c: Horizontal(g840)
    c: Horizontal(g842)
    c: Horizontal(g846)
    c: Horizontal(g850)
    c: Horizontal(g852)
    c: Horizontal(g854)
    c: Horizontal(g856)
    c: Horizontal(g860)
    c: Horizontal(g862)
    c: Horizontal(g864)
    c: Horizontal(g844)
    c: Coincident(g864,g879)
    c: Coincident(g879,g880)
    c: Coincident(g880,g881)
    c: Coincident(g881,g882)
    c: Horizontal(g882)
    c: Coincident(g883,g1)
    c: Coincident(g883,g0)
    c: Vertical(g883)
    c: Coincident(g0,g882)
    c: Coincident(g1,g2)
    c: Coincident(g3,g4)
    c: Coincident(g4,g5)
    c: Coincident(g5,g6)
    c: Coincident(g6,g7)
    c: Coincident(g13,g14)
    c: Coincident(g14,g15)
    c: Coincident(g16,g17)
    c: Coincident(g18,g19)
    c: Coincident(g22,g23)
    c: Coincident(g24,g25)
    c: Coincident(g27,g28)
    c: Vertical(g26)
    c: Coincident(g28,g29)
    c: Coincident(g30,g31)
    c: Horizontal(g29)
    c: Coincident(g37,g38)
    c: Coincident(g38,g39)
    c: Coincident(g39,g40)
    c: Coincident(g40,g41)
    c: Coincident(g42,g43)
    c: Coincident(g20,g21)
    c: Coincident(g21,g22)
    c: Coincident(g25,g26)
    c: Coincident(g48,g49)
    c: Coincident(g49,g50)
    c: Coincident(g58,g59)
    c: Horizontal(g59)
    c: Coincident(g61,g62)
    c: Coincident(g64,g65)
    c: Coincident(g65,g66)
    c: Coincident(g66,g67)
    c: Coincident(g68,g69)
    c: Coincident(g70,g71)
    c: Coincident(g72,g73)
    c: Coincident(g74,g75)
    c: Coincident(g86,g87)
    c: Coincident(g87,g88)
    c: Coincident(g92,g93)
    c: Coincident(g94,g95)
    c: Coincident(g96,g97)
    c: Coincident(g51,g52)
    c: Coincident(g62,g63)
    c: Coincident(g76,g77)
    c: Coincident(g77,g78)
    c: Coincident(g82,g83)
    c: Coincident(g83,g84)
FEATURE [Part::Extrusion] Extrude010  label="LogoCutTop"
  Base = -> Sketch013
  Dir = (0,-1,2e-16)
  DirMode = 2
  FaceMakerClass = Part::FaceMakerBullseye
  LengthFwd = 2
  LengthRev = 0
  Placement = pos=(0,-24.5,0) rot=(0,0,1;0rad)
  Solid = true
  Symmetric = false
FEATURE [Part::Box] Box028  label="Cube027"
  AttacherType = Attacher::AttachEngine3D
  Height = 103.5
  Length = 80
  Placement = pos=(-1,-26,-14.75) rot=(0,0,1;0rad)
  Width = 10
FEATURE [Part::Box] Box029  label="Cube028"
  AttacherType = Attacher::AttachEngine3D
  Height = 105.5
  Length = 82
  Placement = pos=(-2,-27,-15.75) rot=(0,0,1;0rad)
  Width = 10
FEATURE [Part::Fillet] Fillet033  label="topRidge002"
  Base = -> Box028
  Edges = 4 edges r=10: [Edge2,Edge4,Edge6,Edge8]
  Placement = pos=(0,0.5,0) rot=(0,0,1;0rad)
FEATURE [Part::Fillet] Fillet034  label="top001"
  Base = -> Box029
  Edges = 4 edges r=10: [Edge2,Edge4,Edge6,Edge8]
  Placement = pos=(0,1.5,0) rot=(0,0,1;0rad)
FEATURE [Part::Cut] Cut009  label="topCut"
  Base = -> Fillet034
  Tool = -> Fillet033
FEATURE [Part::MultiFuse] Fusion049  label="top002"
  Shapes = -> [Fusion043,Fillet024]
FEATURE [Part::MultiFuse] Fusion050  label="top003"
  Shapes = -> [Fusion049,Fillet032]
FEATURE [Part::Cylinder] Cylinder033  label="m3Holds"
  Angle = 360
  AttacherType = Attacher::AttachEngine3D
  FirstAngle = 0
  Height = 15
  Placement = pos=(72,24,-9) rot=(1,0,0;1.5708rad)
  Radius = 6
  SecondAngle = 0
FEATURE [Part::Cylinder] Cylinder034  label="m3Holds001"
  Angle = 360
  AttacherType = Attacher::AttachEngine3D
  FirstAngle = 0
  Height = 15
  Placement = pos=(6,24,-9) rot=(1,0,0;1.5708rad)
  Radius = 6
  SecondAngle = 0
FEATURE [Part::Cylinder] Cylinder035  label="m3Holds002"
  Angle = 360
  AttacherType = Attacher::AttachEngine3D
  FirstAngle = 0
  Height = 15
  Placement = pos=(72,24,82) rot=(1,0,0;1.5708rad)
  Radius = 6
  SecondAngle = 0
FEATURE [Part::Cylinder] Cylinder036  label="m3Holds003"
  Angle = 360
  AttacherType = Attacher::AttachEngine3D
  FirstAngle = 0
  Height = 15
  Placement = pos=(6,24,82) rot=(1,0,0;1.5708rad)
  Radius = 6
  SecondAngle = 0
FEATURE [Part::MultiFuse] Fusion051  label="m3Holds004BottomIn"
  Shapes = -> [Cylinder033,Cylinder034,Cylinder035,Cylinder036]
FEATURE [Part::Cylinder] Cylinder037  label="m3Holds005"
  Angle = 360
  AttacherType = Attacher::AttachEngine3D
  FirstAngle = 0
  Height = 15
  Placement = pos=(72,24,-9) rot=(1,0,0;1.5708rad)
  Radius = 3
  SecondAngle = 0
FEATURE [Part::Cylinder] Cylinder038  label="m3Holds006"
  Angle = 360
  AttacherType = Attacher::AttachEngine3D
  FirstAngle = 0
  Height = 15
  Placement = pos=(6,24,-9) rot=(1,0,0;1.5708rad)
  Radius = 3
  SecondAngle = 0
FEATURE [Part::Cylinder] Cylinder039  label="m3Holds007"
  Angle = 360
  AttacherType = Attacher::AttachEngine3D
  FirstAngle = 0
  Height = 15
  Placement = pos=(72,24,82) rot=(1,0,0;1.5708rad)
  Radius = 3
  SecondAngle = 0
FEATURE [Part::Cylinder] Cylinder040  label="m3Holds008"
  Angle = 360
  AttacherType = Attacher::AttachEngine3D
  FirstAngle = 0
  Height = 15
  Placement = pos=(6,24,82) rot=(1,0,0;1.5708rad)
  Radius = 3
  SecondAngle = 0
FEATURE [Part::MultiFuse] Fusion052  label="m3Cuts002"
  Placement = pos=(0,13,0) rot=(0,0,1;0rad)
  Shapes = -> [Cylinder037,Cylinder038,Cylinder039,Cylinder040]
FEATURE [Part::Cylinder] Cylinder041  label="m3Holds009"
  Angle = 360
  AttacherType = Attacher::AttachEngine3D
  FirstAngle = 0
  Height = 15
  Placement = pos=(72,24,-9) rot=(1,0,0;1.5708rad)
  Radius = 1.75
  SecondAngle = 0
FEATURE [Part::Cylinder] Cylinder042  label="m3Holds010"
  Angle = 360
  AttacherType = Attacher::AttachEngine3D
  FirstAngle = 0
  Height = 15
  Placement = pos=(6,24,-9) rot=(1,0,0;1.5708rad)
  Radius = 1.75
  SecondAngle = 0
FEATURE [Part::Cylinder] Cylinder043  label="m3Holds011"
  Angle = 360
  AttacherType = Attacher::AttachEngine3D
  FirstAngle = 0
  Height = 15
  Placement = pos=(72,24,82) rot=(1,0,0;1.5708rad)
  Radius = 1.75
  SecondAngle = 0
FEATURE [Part::Cylinder] Cylinder044  label="m3Holds012"
  Angle = 360
  AttacherType = Attacher::AttachEngine3D
  FirstAngle = 0
  Height = 15
  Placement = pos=(6,24,82) rot=(1,0,0;1.5708rad)
  Radius = 1.75
  SecondAngle = 0
FEATURE [Part::MultiFuse] Fusion053  label="m3Cuts_1_75sBottom"
  Shapes = -> [Cylinder041,Cylinder042,Cylinder043,Cylinder044]
FEATURE [Sketcher::SketchObject] Sketch014
  FullyConstrained = false
  Placement = pos=(0,0,0) rot=(1,0,0;1.5708rad)
  sketch-geometry (5):
    g0: GeomPoint X=9.59625 Y=86.1751 Z=0
    g1: LineSegment StartX=11 StartY=101.175 StartZ=0 EndX=9 EndY=98.9251 EndZ=0
    g2: LineSegment StartX=9 StartY=98.9251 StartZ=0 EndX=69 EndY=98.9251 EndZ=0
    g3: LineSegment StartX=69 StartY=98.9251 StartZ=0 EndX=67 EndY=101.175 EndZ=0
    g4: LineSegment StartX=67 StartY=101.175 StartZ=0 EndX=11 EndY=101.175 EndZ=0
  constraints (18):
    c: Coincident(g2,g1)
    c: Horizontal(g2)
    c: Coincident(g3,g2)
    c: Coincident(g4,g3)
    c: Coincident(g1,g4)
    c: DistanceX(g1,g2) = 60
    c: DistanceX(g1,g3) = 56
    c: DistanceY(g2,g3) = 2.25
    c: DistanceX(g1,g1) = 2
    c: DistanceY(g0,g4) = 15
    c: DistanceX(g1,g4) = 0
    c: DistanceY(g2,g4) = 2
    c: DistanceX(g2,g4) = -58
    c: DistanceY(g3,g4) = 2.25
    c: DistanceX(g3,g4) = -56
    c: DistanceX(g4,g4) = -56
    c: DistanceY(g4,g4) = 0
    c: DistanceX(g1) = 9
FEATURE [Part::Extrusion] Extrude011  label="cap002"
  Base = -> Sketch014
  Dir = (0,-1,2e-16)
  DirMode = 2
  FaceMakerClass = Part::FaceMakerBullseye
  LengthFwd = 25
  LengthRev = 0
  Placement = pos=(0.5,-6.5,0) rot=(0,0,1;0rad)
  Solid = true
  Symmetric = false
FEATURE [Part::Fillet] Fillet035
  Base = -> Extrude011
  Edges = 2 edges r=2: [Edge3,Edge9]
FEATURE [Part::Fillet] Fillet036  label="capCutBottom"
  Base = -> Fillet035
  Edges = 2 edges r=0.5: [Edge3,Edge14]
  Placement = pos=(-0.5,4.5,-11.18) rot=(0,0,1;0rad)
FEATURE [Part::Cylinder] Cylinder045  label="m3Holds013"
  Angle = 360
  AttacherType = Attacher::AttachEngine3D
  FirstAngle = 0
  Height = 60
  Placement = pos=(72,24,-9) rot=(1,0,0;1.5708rad)
  Radius = 1.75
  SecondAngle = 0
FEATURE [Part::Cylinder] Cylinder046  label="m3Holds014"
  Angle = 360
  AttacherType = Attacher::AttachEngine3D
  FirstAngle = 0
  Height = 60
  Placement = pos=(6,24,-9) rot=(1,0,0;1.5708rad)
  Radius = 1.75
  SecondAngle = 0
FEATURE [Part::Cylinder] Cylinder047  label="m3Holds015"
  Angle = 360
  AttacherType = Attacher::AttachEngine3D
  FirstAngle = 0
  Height = 60
  Placement = pos=(72,24,82) rot=(1,0,0;1.5708rad)
  Radius = 1.75
  SecondAngle = 0
FEATURE [Part::Cylinder] Cylinder048  label="m3Holds016"
  Angle = 360
  AttacherType = Attacher::AttachEngine3D
  FirstAngle = 0
  Height = 60
  Placement = pos=(6,24,82) rot=(1,0,0;1.5708rad)
  Radius = 1.75
  SecondAngle = 0
FEATURE [Part::MultiFuse] Fusion054  label="m3TopCuts_1_75_Bottom_001"
  Placement = pos=(0,10,0) rot=(0,0,1;0rad)
  Shapes = -> [Cylinder045,Cylinder046,Cylinder047,Cylinder048]
FEATURE [Part::Box] Box045  label="Cube036"
  AttacherType = Attacher::AttachEngine3D
  Height = 2
  Length = 30
  Placement = pos=(0,0,0) rot=(0,-1,0;0.785398rad)
  Width = 10
FEATURE [Part::Box] Box046  label="Cube037"
  AttacherType = Attacher::AttachEngine3D
  Height = 2
  Length = 20
  Placement = pos=(0,0,10) rot=(0,-1,0;0.785398rad)
  Width = 10
FEATURE [Part::Box] Box047  label="Cube038"
  AttacherType = Attacher::AttachEngine3D
  Height = 2
  Length = 20
  Placement = pos=(0,0,20) rot=(0,-1,0;0.785398rad)
  Width = 10
FEATURE [Part::Box] Box048  label="Cube039"
  AttacherType = Attacher::AttachEngine3D
  Height = 2
  Length = 20
  Placement = pos=(0,0,30) rot=(0,-1,0;0.785398rad)
  Width = 10
FEATURE [Part::Box] Box049  label="Cube040"
  AttacherType = Attacher::AttachEngine3D
  Height = 2
  Length = 10
  Placement = pos=(0,0,40) rot=(0,-1,0;0.785398rad)
  Width = 10
FEATURE [Part::Box] Box050  label="Cube041"
  AttacherType = Attacher::AttachEngine3D
  Height = 2
  Length = 20
  Placement = pos=(0,0,50) rot=(0,-1,0;0.785398rad)
  Width = 10
FEATURE [Part::Box] Box051  label="Cube042"
  AttacherType = Attacher::AttachEngine3D
  Height = 2
  Length = 20
  Placement = pos=(0,0,60) rot=(0,-1,0;0.785398rad)
  Width = 10
FEATURE [Part::Box] Box052  label="Cube043"
  AttacherType = Attacher::AttachEngine3D
  Height = 2
  Length = 20
  Placement = pos=(0,0,70) rot=(0,-1,0;0.785398rad)
  Width = 10
FEATURE [Part::Box] Box053  label="Cube044"
  AttacherType = Attacher::AttachEngine3D
  Height = 2
  Length = 20
  Placement = pos=(0,0,80) rot=(0,-1,0;0.785398rad)
  Width = 10
FEATURE [Part::Box] Box054  label="Cube045"
  AttacherType = Attacher::AttachEngine3D
  Height = 2
  Length = 20
  Placement = pos=(0,0,90) rot=(0,-1,0;0.785398rad)
  Width = 10
FEATURE [Part::Box] Box055  label="Cube046"
  AttacherType = Attacher::AttachEngine3D
  Height = 2
  Length = 20
  Placement = pos=(0,0,1000) rot=(0,-1,0;0.785398rad)
  Width = 10
FEATURE [Part::Box] Box056  label="Cube047"
  AttacherType = Attacher::AttachEngine3D
  Height = 2
  Length = 30
  Placement = pos=(0,0,0) rot=(0,-1,0;0.785398rad)
  Width = 10
FEATURE [Part::Box] Box057  label="Cube048"
  AttacherType = Attacher::AttachEngine3D
  Height = 2
  Length = 20
  Placement = pos=(0,0,10) rot=(0,-1,0;0.785398rad)
  Width = 10
FEATURE [Part::Box] Box058  label="Cube049"
  AttacherType = Attacher::AttachEngine3D
  Height = 2
  Length = 20
  Placement = pos=(0,0,20) rot=(0,-1,0;0.785398rad)
  Width = 10
FEATURE [Part::Box] Box059  label="Cube050"
  AttacherType = Attacher::AttachEngine3D
  Height = 2
  Length = 20
  Placement = pos=(0,0,30) rot=(0,-1,0;0.785398rad)
  Width = 10
FEATURE [Part::Box] Box060  label="Cube051"
  AttacherType = Attacher::AttachEngine3D
  Height = 2
  Length = 10
  Placement = pos=(0,0,40) rot=(0,-1,0;0.785398rad)
  Width = 10
FEATURE [Part::Box] Box061  label="Cube052"
  AttacherType = Attacher::AttachEngine3D
  Height = 2
  Length = 20
  Placement = pos=(0,0,50) rot=(0,-1,0;0.785398rad)
  Width = 10
FEATURE [Part::Box] Box062  label="Cube053"
  AttacherType = Attacher::AttachEngine3D
  Height = 2
  Length = 20
  Placement = pos=(0,0,60) rot=(0,-1,0;0.785398rad)
  Width = 10
FEATURE [Part::Box] Box063  label="Cube054"
  AttacherType = Attacher::AttachEngine3D
  Height = 2
  Length = 20
  Placement = pos=(0,0,70) rot=(0,-1,0;0.785398rad)
  Width = 10
FEATURE [Part::Box] Box064  label="Cube055"
  AttacherType = Attacher::AttachEngine3D
  Height = 2
  Length = 10
  Placement = pos=(0,0,80) rot=(0,-1,0;0.785398rad)
  Width = 10
FEATURE [Part::Box] Box065  label="Cube056"
  AttacherType = Attacher::AttachEngine3D
  Height = 2
  Length = 20
  Placement = pos=(0,0,90) rot=(0,-1,0;0.785398rad)
  Width = 10
FEATURE [Part::Box] Box066  label="Cube057"
  AttacherType = Attacher::AttachEngine3D
  Height = 2
  Length = 20
  Placement = pos=(0,0,1000) rot=(0,-1,0;0.785398rad)
  Width = 10
FEATURE [Part::MultiFuse] Fusion056
  Placement = pos=(82,0,15) rot=(0,0,1;3.14159rad)
  Shapes = -> [Box056,Box057,Box058,Box059,Box060,Box061,Box062,Box063,Box064,Box065,Box066,Box055]
FEATURE [Part::MultiFuse] Fusion055
  Placement = pos=(-4,-10,15) rot=(0,0,1;0rad)
  Shapes = -> [Box045,Box046,Box047,Box048,Box049,Box050,Box051,Box052,Box053,Box054]
FEATURE [Part::MultiFuse] Fusion057
  Placement = pos=(0,-5,-48) rot=(0,0,1;0rad)
  Shapes = -> [Fusion055,Fusion056]
FEATURE [Part::Box] Box067  label="Cube058"
  AttacherType = Attacher::AttachEngine3D
  Height = 2
  Length = 30
  Placement = pos=(0,0,0) rot=(0,-1,0;0.785398rad)
  Width = 10
FEATURE [Part::Box] Box068  label="Cube059"
  AttacherType = Attacher::AttachEngine3D
  Height = 2
  Length = 20
  Placement = pos=(0,0,10) rot=(0,-1,0;0.785398rad)
  Width = 10
FEATURE [Part::Box] Box069  label="Cube060"
  AttacherType = Attacher::AttachEngine3D
  Height = 2
  Length = 20
  Placement = pos=(0,0,20) rot=(0,-1,0;0.785398rad)
  Width = 10
FEATURE [Part::Box] Box070  label="Cube061"
  AttacherType = Attacher::AttachEngine3D
  Height = 2
  Length = 20
  Placement = pos=(0,0,30) rot=(0,-1,0;0.785398rad)
  Width = 10
FEATURE [Part::Box] Box071  label="Cube062"
  AttacherType = Attacher::AttachEngine3D
  Height = 2
  Length = 10
  Placement = pos=(0,0,40) rot=(0,-1,0;0.785398rad)
  Width = 10
FEATURE [Part::Box] Box072  label="Cube063"
  AttacherType = Attacher::AttachEngine3D
  Height = 2
  Length = 20
  Placement = pos=(0,0,50) rot=(0,-1,0;0.785398rad)
  Width = 10
FEATURE [Part::Box] Box073  label="Cube064"
  AttacherType = Attacher::AttachEngine3D
  Height = 2
  Length = 20
  Placement = pos=(0,0,60) rot=(0,-1,0;0.785398rad)
  Width = 10
FEATURE [Part::Box] Box074  label="Cube065"
  AttacherType = Attacher::AttachEngine3D
  Height = 2
  Length = 20
  Placement = pos=(0,0,70) rot=(0,-1,0;0.785398rad)
  Width = 10
FEATURE [Part::Box] Box075  label="Cube066"
  AttacherType = Attacher::AttachEngine3D
  Height = 2
  Length = 20
  Placement = pos=(0,0,80) rot=(0,-1,0;0.785398rad)
  Width = 10
FEATURE [Part::Box] Box076  label="Cube067"
  AttacherType = Attacher::AttachEngine3D
  Height = 2
  Length = 30
  Placement = pos=(0,0,90) rot=(0,-1,0;0.785398rad)
  Width = 20
FEATURE [Part::Box] Box077  label="Cube068"
  AttacherType = Attacher::AttachEngine3D
  Height = 2
  Length = 20
  Placement = pos=(0,0,1000) rot=(0,-1,0;0.785398rad)
  Width = 10
FEATURE [Part::Box] Box078  label="Cube069"
  AttacherType = Attacher::AttachEngine3D
  Height = 2
  Length = 30
  Placement = pos=(0,0,0) rot=(0,-1,0;0.785398rad)
  Width = 10
FEATURE [Part::Box] Box079  label="Cube070"
  AttacherType = Attacher::AttachEngine3D
  Height = 2
  Length = 20
  Placement = pos=(0,0,10) rot=(0,-1,0;0.785398rad)
  Width = 10
FEATURE [Part::Box] Box080  label="Cube071"
  AttacherType = Attacher::AttachEngine3D
  Height = 2
  Length = 20
  Placement = pos=(0,0,20) rot=(0,-1,0;0.785398rad)
  Width = 10
FEATURE [Part::Box] Box081  label="Cube072"
  AttacherType = Attacher::AttachEngine3D
  Height = 2
  Length = 20
  Placement = pos=(0,0,30) rot=(0,-1,0;0.785398rad)
  Width = 10
FEATURE [Part::Box] Box082  label="Cube073"
  AttacherType = Attacher::AttachEngine3D
  Height = 2
  Length = 10
  Placement = pos=(0,0,40) rot=(0,-1,0;0.785398rad)
  Width = 10
FEATURE [Part::Box] Box083  label="Cube074"
  AttacherType = Attacher::AttachEngine3D
  Height = 2
  Length = 20
  Placement = pos=(0,0,50) rot=(0,-1,0;0.785398rad)
  Width = 10
FEATURE [Part::Box] Box084  label="Cube075"
  AttacherType = Attacher::AttachEngine3D
  Height = 2
  Length = 20
  Placement = pos=(0,0,60) rot=(0,-1,0;0.785398rad)
  Width = 10
FEATURE [Part::Box] Box085  label="Cube076"
  AttacherType = Attacher::AttachEngine3D
  Height = 2
  Length = 20
  Placement = pos=(0,0,70) rot=(0,-1,0;0.785398rad)
  Width = 10
FEATURE [Part::Box] Box086  label="Cube077"
  AttacherType = Attacher::AttachEngine3D
  Height = 2
  Length = 10
  Placement = pos=(0,0,80) rot=(0,-1,0;0.785398rad)
  Width = 10
FEATURE [Part::Box] Box087  label="Cube078"
  AttacherType = Attacher::AttachEngine3D
  Height = 2
  Length = 30
  Placement = pos=(0,0,90) rot=(0,-1,0;0.785398rad)
  Width = 20
FEATURE [Part::Box] Box088  label="Cube079"
  AttacherType = Attacher::AttachEngine3D
  Height = 2
  Length = 20
  Placement = pos=(0,0,1000) rot=(0,-1,0;0.785398rad)
  Width = 10
FEATURE [Part::MultiFuse] Fusion058
  Placement = pos=(-4,-10,15) rot=(0,0,1;0rad)
  Shapes = -> [Box067,Box068,Box069,Box070,Box071,Box072,Box073,Box074,Box075,Box076,Box077]
FEATURE [Part::MultiFuse] Fusion059
  Placement = pos=(82,10,15) rot=(0,0,1;3.14159rad)
  Shapes = -> [Box078,Box079,Box080,Box081,Box082,Box083,Box084,Box085,Box086,Box087,Box088]
FEATURE [Part::MultiFuse] Fusion060
  Placement = pos=(0,10.25,-138) rot=(0,0,1;0rad)
  Shapes = -> [Fusion058,Fusion059]
FEATURE [Part::MultiFuse] Fusion061  label="vents"
  Shapes = -> [Fusion060,Fusion057]
FEATURE [Part::Cut] Cut010  label="bottom001"
  Base = -> Cut007
  Tool = -> Fusion061
FEATURE [Part::Cylinder] Cylinder049  label="m3Holds017"
  Angle = 360
  AttacherType = Attacher::AttachEngine3D
  FirstAngle = 0
  Height = 15
  Placement = pos=(63.6,0.25,61.5) rot=(1,0,0;1.5708rad)
  Radius = 1.75
  SecondAngle = 0
FEATURE [Part::Cylinder] Cylinder051  label="m3Holds019"
  Angle = 360
  AttacherType = Attacher::AttachEngine3D
  FirstAngle = 0
  Height = 15
  Placement = pos=(14.6,0.25,3.5) rot=(1,0,0;1.5708rad)
  Radius = 1.75
  SecondAngle = 0
FEATURE [Part::Cylinder] Cylinder052  label="m3Holds020"
  Angle = 360
  AttacherType = Attacher::AttachEngine3D
  FirstAngle = 0
  Height = 15
  Placement = pos=(63.6,0.25,3.5) rot=(1,0,0;1.5708rad)
  Radius = 1.75
  SecondAngle = 0
FEATURE [Part::Cylinder] Cylinder053  label="m3Holds021"
  Angle = 360
  AttacherType = Attacher::AttachEngine3D
  FirstAngle = 0
  Height = 15
  Placement = pos=(72,0.25,-9) rot=(1,0,0;1.5708rad)
  Radius = 1.75
  SecondAngle = 0
FEATURE [Part::Cylinder] Cylinder054  label="m3Holds022"
  Angle = 360
  AttacherType = Attacher::AttachEngine3D
  FirstAngle = 0
  Height = 15
  Placement = pos=(6,0.25,-9) rot=(1,0,0;1.5708rad)
  Radius = 1.75
  SecondAngle = 0
FEATURE [Part::Cylinder] Cylinder056  label="m3Holds024"
  Angle = 360
  AttacherType = Attacher::AttachEngine3D
  FirstAngle = 0
  Height = 15
  Placement = pos=(72,0.25,82) rot=(1,0,0;1.5708rad)
  Radius = 1.75
  SecondAngle = 0
FEATURE [Part::Cylinder] Cylinder057  label="m3Holds025"
  Angle = 360
  AttacherType = Attacher::AttachEngine3D
  FirstAngle = 0
  Height = 15
  Placement = pos=(6,0.25,82) rot=(1,0,0;1.5708rad)
  Radius = 1.75
  SecondAngle = 0
FEATURE [Part::Cylinder] Cylinder058  label="m3Holds026"
  Angle = 360
  AttacherType = Attacher::AttachEngine3D
  FirstAngle = 0
  Height = 15
  Placement = pos=(14.6,0.25,61.5) rot=(1,0,0;1.5708rad)
  Radius = 1.75
  SecondAngle = 0
FEATURE [Part::MultiFuse] Fusion062
  Shapes = -> [Cylinder049,Cylinder056]
FEATURE [Part::MultiFuse] Fusion064
  Shapes = -> [Cylinder052,Cylinder053]
FEATURE [Part::MultiFuse] Fusion065
  Shapes = -> [Cylinder051,Cylinder054]
FEATURE [Part::MultiFuse] Fusion066
  Shapes = -> [Cylinder057,Cylinder058]
FEATURE [Part::Cut] Cut011  label="c4HoldTopLeft"
  Base = -> Extrude001
  Tool = -> Fusion066
FEATURE [Part::Cut] Cut012  label="c4HoldTopRight"
  Base = -> Extrude002
  Tool = -> Fusion062
FEATURE [Part::MultiFuse] Fusion067
  Shapes = -> [Extrude004,Part__Mirroring005]
FEATURE [Part::Cut] Cut013  label="c4HoldBottomLeft"
  Base = -> Fusion067
  Tool = -> Fusion065
FEATURE [Part::Cut] Cut014  label="c4HoldBotttomRight"
  Base = -> Fusion041
  Tool = -> Fusion064
FEATURE [Part::MultiFuse] Fusion068  label="m3CutsBottom"
  Shapes = -> [Fusion052,Fusion053]
FEATURE [Sketcher::SketchObject] Sketch015
  FullyConstrained = false
  Placement = pos=(0,0,0) rot=(1,0,0;1.5708rad)
  sketch-geometry (5):
    g0: GeomPoint X=9.71668 Y=86.1751 Z=0
    g1: LineSegment StartX=11 StartY=101.175 StartZ=0 EndX=9 EndY=98.9251 EndZ=0
    g2: LineSegment StartX=9 StartY=98.9251 StartZ=0 EndX=69 EndY=98.9251 EndZ=0
    g3: LineSegment StartX=69 StartY=98.9251 StartZ=0 EndX=67 EndY=101.175 EndZ=0
    g4: LineSegment StartX=67 StartY=101.175 StartZ=0 EndX=11 EndY=101.175 EndZ=0
  constraints (18):
    c: Coincident(g2,g1)
    c: Horizontal(g2)
    c: Coincident(g3,g2)
    c: Coincident(g4,g3)
    c: Coincident(g1,g4)
    c: DistanceX(g1,g2) = 60
    c: DistanceX(g1,g3) = 56
    c: DistanceY(g2,g3) = 2.25
    c: DistanceX(g1,g1) = 2
    c: DistanceY(g0,g4) = 15
    c: DistanceX(g1,g4) = 0
    c: DistanceY(g2,g4) = 2
    c: DistanceX(g2,g4) = -58
    c: DistanceY(g3,g4) = 2.25
    c: DistanceX(g3,g4) = -56
    c: DistanceX(g4,g4) = -56
    c: DistanceY(g4,g4) = 0
    c: DistanceX(g1) = 9
FEATURE [Part::Extrusion] Extrude012  label="cap003"
  Base = -> Sketch015
  Dir = (0,-1,2e-16)
  DirMode = 2
  FaceMakerClass = Part::FaceMakerBullseye
  LengthFwd = 25
  LengthRev = 0
  Placement = pos=(0.5,-6.5,0) rot=(0,0,1;0rad)
  Solid = true
  Symmetric = false
FEATURE [Part::Fillet] Fillet037
  Base = -> Extrude012
  Edges = 2 edges r=2: [Edge3,Edge9]
FEATURE [Part::Fillet] Fillet038  label="capCutTop"
  Base = -> Fillet037
  Edges = 2 edges r=0.5: [Edge3,Edge14]
  Placement = pos=(-0.5,4.5,-11.18) rot=(0,0,1;0rad)
FEATURE [Part::MultiFuse] Fusion071  label="bottomCuts"
  Shapes = -> [Fusion068,Fillet036,Fusion044]
FEATURE [Part::MultiFuse] Fusion072  label="BatteryHold"
  Shapes = -> [Part__Mirroring004,Part__Mirroring002]
FEATURE [Sketcher::SketchObject] Sketch016
  FullyConstrained = false
  MapMode = 5
  Placement = pos=(0,0,0) rot=(1,0,0;1.5708rad)
  Support = -> [XZ_Plane004]
  sketch-geometry (5):
    g0: LineSegment StartX=0 StartY=77.5 StartZ=0 EndX=10.75 EndY=77.5 EndZ=0
    g1: LineSegment StartX=10.75 StartY=77.5 StartZ=0 EndX=10.75 EndY=74.234 EndZ=0
    g2: ArcOfCircle CenterX=15.5057 CenterY=59.9075 CenterZ=0 NormalX=0 NormalY=0 NormalZ=1 AngleXU=0 Radius=15.0952 StartAngle=1.8913 EndAngle=3.06915
    g3: LineSegment StartX=0 StartY=77.5 StartZ=0 EndX=0 EndY=61 EndZ=0
    g4: LineSegment StartX=0 StartY=61 StartZ=0 EndX=0.45 EndY=61 EndZ=0
  constraints (14):
    c: Coincident(g4,g3)
    c: Vertical(g3)
    c: Horizontal(g4)
    c: Horizontal(g0)
    c: Vertical(g1)
    c: DistanceY(g3,g0) = 16.5
    c: DistanceX(g0,g0) = 10.75
    c: DistanceX(g3,g2) = 0.45
    c: DistanceY(g-1,g3) = 61
    c: DistanceX(g3,g-1) = 0
    c: Coincident(g2,g4)
    c: Coincident(g2,g1)
    c: Coincident(g1,g0)
    c: Coincident(g0,g3)
FEATURE [PartDesign::Pad] Pad002
  Direction = (0,-1,-2e-16)
  Length = 15
  Length2 = 10
  Placement = pos=(0,0,0) rot=(1,0,0;1.5708rad)
  Profile = -> Sketch016
  ReferenceAxis = -> Sketch016 [N_Axis]
  Type = 0
FEATURE [PartDesign::Body] Body002  label="batteryHold002"
  Group = -> [Sketch016,Pad002]
  Origin = -> Origin004
  Placement = pos=(0,24,0) rot=(0,0,1;0rad)
  Tip = -> Pad002
FEATURE [Sketcher::SketchObject] Sketch017
  FullyConstrained = false
  MapMode = 5
  Placement = pos=(0,0,0) rot=(1,0,0;1.5708rad)
  Support = -> [XZ_Plane005]
  sketch-geometry (5):
    g0: LineSegment StartX=0 StartY=77.5 StartZ=0 EndX=10.75 EndY=77.5 EndZ=0
    g1: LineSegment StartX=10.75 StartY=77.5 StartZ=0 EndX=10.75 EndY=74.234 EndZ=0
    g2: ArcOfCircle CenterX=15.5057 CenterY=59.9075 CenterZ=0 NormalX=0 NormalY=0 NormalZ=1 AngleXU=0 Radius=15.0952 StartAngle=1.8913 EndAngle=3.06915
    g3: LineSegment StartX=0 StartY=77.5 StartZ=0 EndX=0 EndY=61 EndZ=0
    g4: LineSegment StartX=0 StartY=61 StartZ=0 EndX=0.45 EndY=61 EndZ=0
  constraints (14):
    c: Coincident(g4,g3)
    c: Vertical(g3)
    c: Horizontal(g4)
    c: Horizontal(g0)
    c: Vertical(g1)
    c: DistanceY(g3,g0) = 16.5
    c: DistanceX(g0,g0) = 10.75
    c: DistanceX(g3,g2) = 0.45
    c: DistanceY(g-1,g3) = 61
    c: DistanceX(g3,g-1) = 0
    c: Coincident(g2,g4)
    c: Coincident(g2,g1)
    c: Coincident(g1,g0)
    c: Coincident(g0,g3)
FEATURE [PartDesign::Pad] Pad003
  Direction = (0,-1,-2e-16)
  Length = 15
  Length2 = 10
  Placement = pos=(0,0,0) rot=(1,0,0;1.5708rad)
  Profile = -> Sketch017
  ReferenceAxis = -> Sketch017 [N_Axis]
  Type = 0
FEATURE [PartDesign::Body] Body003  label="batteryHold003"
  Group = -> [Sketch017,Pad003]
  Origin = -> Origin005
  Placement = pos=(0,24,0) rot=(0,0,1;0rad)
  Tip = -> Pad003
FEATURE [Part::Mirroring] Part__Mirroring010  label="batteryHold001 (Mirror #4)001"
  Base = (0,0,0)
  Normal = (0,0,1)
  Placement = pos=(0,0,74.5) rot=(0,0,1;0rad)
  Source = -> Body003
FEATURE [Part::MultiFuse] Fusion073  label="batteryHolds"
  Shapes = -> [Part__Mirroring010,Fusion072,Body002]
FEATURE [Part::MultiFuse] Fusion074  label="bottom002"
  Shapes = -> [Fusion073,Cut010,Fusion051,Cylinder032,Fillet029,Fusion042,Fusion039,Fillet020,Fillet019]
FEATURE [Part::Cut] Cut015  label="bottom003"
  Base = -> Fusion074
  Tool = -> Fusion071
FEATURE [Part::Cut] Cut016  label="Bottom"
  Base = -> Cut015
  Tool = -> Fusion054
FEATURE [Part::Cylinder] Cylinder059  label="m3Holds027"
  Angle = 360
  AttacherType = Attacher::AttachEngine3D
  FirstAngle = 0
  Height = 60
  Placement = pos=(72,24,-9) rot=(1,0,0;1.5708rad)
  Radius = 1.75
  SecondAngle = 0
FEATURE [Part::Cylinder] Cylinder060  label="m3Holds028"
  Angle = 360
  AttacherType = Attacher::AttachEngine3D
  FirstAngle = 0
  Height = 60
  Placement = pos=(6,24,-9) rot=(1,0,0;1.5708rad)
  Radius = 1.75
  SecondAngle = 0
FEATURE [Part::Cylinder] Cylinder061  label="m3Holds029"
  Angle = 360
  AttacherType = Attacher::AttachEngine3D
  FirstAngle = 0
  Height = 60
  Placement = pos=(72,24,82) rot=(1,0,0;1.5708rad)
  Radius = 1.75
  SecondAngle = 0
FEATURE [Part::Cylinder] Cylinder062  label="m3Holds030"
  Angle = 360
  AttacherType = Attacher::AttachEngine3D
  FirstAngle = 0
  Height = 60
  Placement = pos=(6,24,82) rot=(1,0,0;1.5708rad)
  Radius = 1.75
  SecondAngle = 0
FEATURE [Part::MultiFuse] Fusion075  label="m3TopCuts_1_75_Top"
  Placement = pos=(0,11.5,0) rot=(0,0,1;0rad)
  Shapes = -> [Cylinder059,Cylinder060,Cylinder061,Cylinder062]
FEATURE [Part::MultiFuse] Fusion076  label="m3Cuts003"
  Shapes = -> [Fusion075,Fillet038,Cut009,Extrude010,Fusion047,Fusion046]
FEATURE [Part::Cut] Cut017  label="Top"
  Base = -> Fusion050
  Placement = pos=(0,1,0) rot=(0,0,1;0rad)
  Tool = -> Fusion076
FEATURE [Sketcher::SketchObject] Sketch018
  FullyConstrained = false
  Placement = pos=(0,0,0) rot=(1,0,0;1.5708rad)
  sketch-geometry (5):
    g0: GeomPoint X=9.71668 Y=86.1751 Z=0
    g1: LineSegment StartX=11 StartY=101.175 StartZ=0 EndX=9 EndY=98.9251 EndZ=0
    g2: LineSegment StartX=9 StartY=98.9251 StartZ=0 EndX=69 EndY=98.9251 EndZ=0
    g3: LineSegment StartX=69 StartY=98.9251 StartZ=0 EndX=67 EndY=101.175 EndZ=0
    g4: LineSegment StartX=67 StartY=101.175 StartZ=0 EndX=11 EndY=101.175 EndZ=0
  constraints (18):
    c: Coincident(g2,g1)
    c: Horizontal(g2)
    c: Coincident(g3,g2)
    c: Coincident(g4,g3)
    c: Coincident(g1,g4)
    c: DistanceX(g1,g2) = 60
    c: DistanceX(g1,g3) = 56
    c: DistanceY(g2,g3) = 2.25
    c: DistanceX(g1,g1) = 2
    c: DistanceY(g0,g4) = 15
    c: DistanceX(g1,g4) = 0
    c: DistanceY(g2,g4) = 2
    c: DistanceX(g2,g4) = -58
    c: DistanceY(g3,g4) = 2.25
    c: DistanceX(g3,g4) = -56
    c: DistanceX(g4,g4) = -56
    c: DistanceY(g4,g4) = 0
    c: DistanceX(g1) = 9
FEATURE [Part::Extrusion] Extrude013  label="cap004"
  Base = -> Sketch018
  Dir = (0,-1,2e-16)
  DirMode = 2
  FaceMakerClass = Part::FaceMakerBullseye
  LengthFwd = 23.5
  LengthRev = 0
  Placement = pos=(0.5,-6.5,0) rot=(0,0,1;0rad)
  Solid = true
  Symmetric = false
FEATURE [Part::Fillet] Fillet039
  Base = -> Extrude013
  Edges = 2 edges r=2: [Edge3,Edge9]
FEATURE [Part::Fillet] Fillet040  label="Cap"
  Base = -> Fillet039
  Edges = 2 edges r=0.5: [Edge3,Edge14]
  Placement = pos=(-0.5,4.5,-11.18) rot=(0,0,1;0rad)
FEATURE [Sketcher::SketchObject] Sketch
  FullyConstrained = true
  Placement = pos=(0,0,0) rot=(0.57735,0.57735,0.57735;2.0944rad)
  sketch-geometry (4):
    g0: ArcOfCircle CenterX=12 CenterY=57.25 CenterZ=0 NormalX=0 NormalY=0 NormalZ=1 AngleXU=0 Radius=3 StartAngle=6e-16 EndAngle=3.14159
    g1: ArcOfCircle CenterX=12 CenterY=49.25 CenterZ=0 NormalX=0 NormalY=0 NormalZ=1 AngleXU=0 Radius=3 StartAngle=3.14159 EndAngle=6.28319
    g2: LineSegment StartX=9 StartY=57.25 StartZ=0 EndX=9 EndY=49.25 EndZ=0
    g3: LineSegment StartX=15 StartY=49.25 StartZ=0 EndX=15 EndY=57.25 EndZ=0
  constraints (14):
    c: Angle(g0) = 3.14159
    c: DistanceY(g0,g0) = 0
    c: Radius(g0) = 3
    c: DistanceX(g0) = 12
    c: DistanceY(g0) = 57.25
    c: Angle(g1) = 3.14159
    c: Radius(g1) = 3
    c: DistanceX(g1) = 12
    c: DistanceY(g1,g1) = 0
    c: DistanceY(g1) = 49.25
    c: Coincident(g2,g0)
    c: Coincident(g2,g1)
    c: Coincident(g3,g1)
    c: Coincident(g3,g0)
FEATURE [Part::Extrusion] Extrude  label="powerCut"
  Base = -> Sketch
  Dir = (1,0,0)
  DirMode = 2
  FaceMakerClass = Part::FaceMakerBullseye
  LengthFwd = 3
  LengthRev = 0
  Placement = pos=(78,0,0) rot=(0,0,1;0rad)
  Solid = true
  Symmetric = false
FEATURE [Sketcher::SketchObject] Sketch019
  FullyConstrained = true
  Placement = pos=(0,0,0) rot=(0.57735,0.57735,0.57735;2.0944rad)
  sketch-geometry (4):
    g0: ArcOfCircle CenterX=11 CenterY=57.5 CenterZ=0 NormalX=0 NormalY=0 NormalZ=1 AngleXU=0 Radius=3 StartAngle=-9e-16 EndAngle=3.14159
    g1: ArcOfCircle CenterX=11 CenterY=48.9929 CenterZ=0 NormalX=0 NormalY=0 NormalZ=1 AngleXU=0 Radius=3 StartAngle=3.14159 EndAngle=6.28319
    g2: LineSegment StartX=8 StartY=57.5 StartZ=0 EndX=8 EndY=48.9929 EndZ=0
    g3: LineSegment StartX=14 StartY=48.9929 StartZ=0 EndX=14 EndY=57.5 EndZ=0
  constraints (14):
    c: Angle(g0) = 3.14159
    c: DistanceY(g0,g0) = 0
    c: DistanceY(g0) = 57.5
    c: DistanceX(g0) = 11
    c: DistanceY(g1,g1) = 0
    c: Radius(g0) = 3
    c: Radius(g1) = 3
    c: DistanceX(g1,g0) = 0
    c: Coincident(g2,g0)
    c: Coincident(g2,g1)
    c: Vertical(g2)
    c: Coincident(g3,g1)
    c: Coincident(g3,g0)
    c: Vertical(g3)
FEATURE [Part::Extrusion] Extrude014  label="chargeCut"
  Base = -> Sketch019
  Dir = (1,0,0)
  DirMode = 2
  FaceMakerClass = Part::FaceMakerBullseye
  LengthFwd = 3
  LengthRev = 0
  Placement = pos=(-3,0,0) rot=(0,0,1;0rad)
  Solid = true
  Symmetric = false
FEATURE [Sketcher::SketchObject] Sketch020
  FullyConstrained = true
  Placement = pos=(0,0,0) rot=(1,0,0;1.5708rad)
  sketch-geometry (4):
    g0: ArcOfCircle CenterX=39 CenterY=64 CenterZ=0 NormalX=0 NormalY=0 NormalZ=1 AngleXU=0 Radius=1 StartAngle=2.5e-15 EndAngle=3.14159
    g1: ArcOfCircle CenterX=39 CenterY=53.5 CenterZ=0 NormalX=0 NormalY=0 NormalZ=1 AngleXU=0 Radius=1 StartAngle=3.1416 EndAngle=6.28318
    g2: LineSegment StartX=38 StartY=64 StartZ=0 EndX=38 EndY=53.5 EndZ=0
    g3: LineSegment StartX=40 StartY=53.5 StartZ=0 EndX=40 EndY=64 EndZ=0
  constraints (14):
    c: Angle(g0) = 3.14159
    c: DistanceY(g0,g0) = 0
    c: DistanceX(g0) = 39
    c: Radius(g0) = 1
    c: DistanceY(g0) = 64
    c: DistanceY(g1,g1) = 0
    c: DistanceX(g1) = 39
    c: Radius(g1) = 1
    c: DistanceY(g1) = 53.5
    c: Coincident(g2,g0)
    c: Coincident(g2,g1)
    c: Vertical(g2)
    c: Coincident(g3,g1)
    c: Coincident(g3,g0)
FEATURE [Part::MultiFuse] Fusion002  label="V25"
  Placement = pos=(39,12,38) rot=(0,0,1;3.14159rad)
  Shapes = -> [Fusion001,Fusion]
FEATURE [Part::Extrusion] Extrude015  label="indicatorCut"
  Base = -> Sketch020
  Dir = (0,-1,-6e-16)
  DirMode = 2
  FaceMakerClass = Part::FaceMakerBullseye
  LengthFwd = 3
  LengthRev = 0
  Placement = pos=(0,27,0) rot=(0,0,1;0rad)
  Solid = true
  Symmetric = false
FEATURE [Part::MultiFuse] Fusion077  label="bottomLastCuts"
  Shapes = -> [Extrude015,Extrude,Extrude014]
FEATURE [Part::Box] Box089  label="ToplightCut"
  AttacherType = Attacher::AttachEngine3D
  Height = 5
  Length = 5
  Placement = pos=(56,-24.5,0) rot=(0,0,1;0rad)
  Width = 5
FEATURE [Part::Cut] Cut018  label="top004"
  Base = -> Cut017
  Tool = -> Box089
FEATURE [Part::Cut] Cut019  label="bottom004"
  Base = -> Cut016
  Tool = -> Fusion077
FEATURE [Part::Fillet] Fillet041  label="bottom005"
  Base = -> Cut019
  Edges = 50 edges r=1: [Edge23,Edge32,Edge272,Edge276,Edge280,Edge285,Edge288,Edge290,Edge293,Edge295,Edge297,Edge300,Edge303,Edge305,Edge307,Edge308,Edge310,Edge539,Edge541,Edge543,Edge545,Edge617,Edge620,Edge622,Edge624,Edge641,Edge642,Edge643,Edge644,Edge645,Edge646,Edge647,Edge648,Edge649,Edge650,Edge651,Edge652,+13 more]
FEATURE [Part::Fillet] Fillet042  label="top005"
  Base = -> Cut018
  Edges = 9 edges r=0.5: [Edge1,Edge5,Edge6,Edge7,Edge8,Edge9,Edge15,Edge16,Edge17]
FEATURE [Part::Fillet] Fillet043  label="cap"
  Base = -> Fillet040
  Edges = 1 edges r=0.5: [Edge5]
